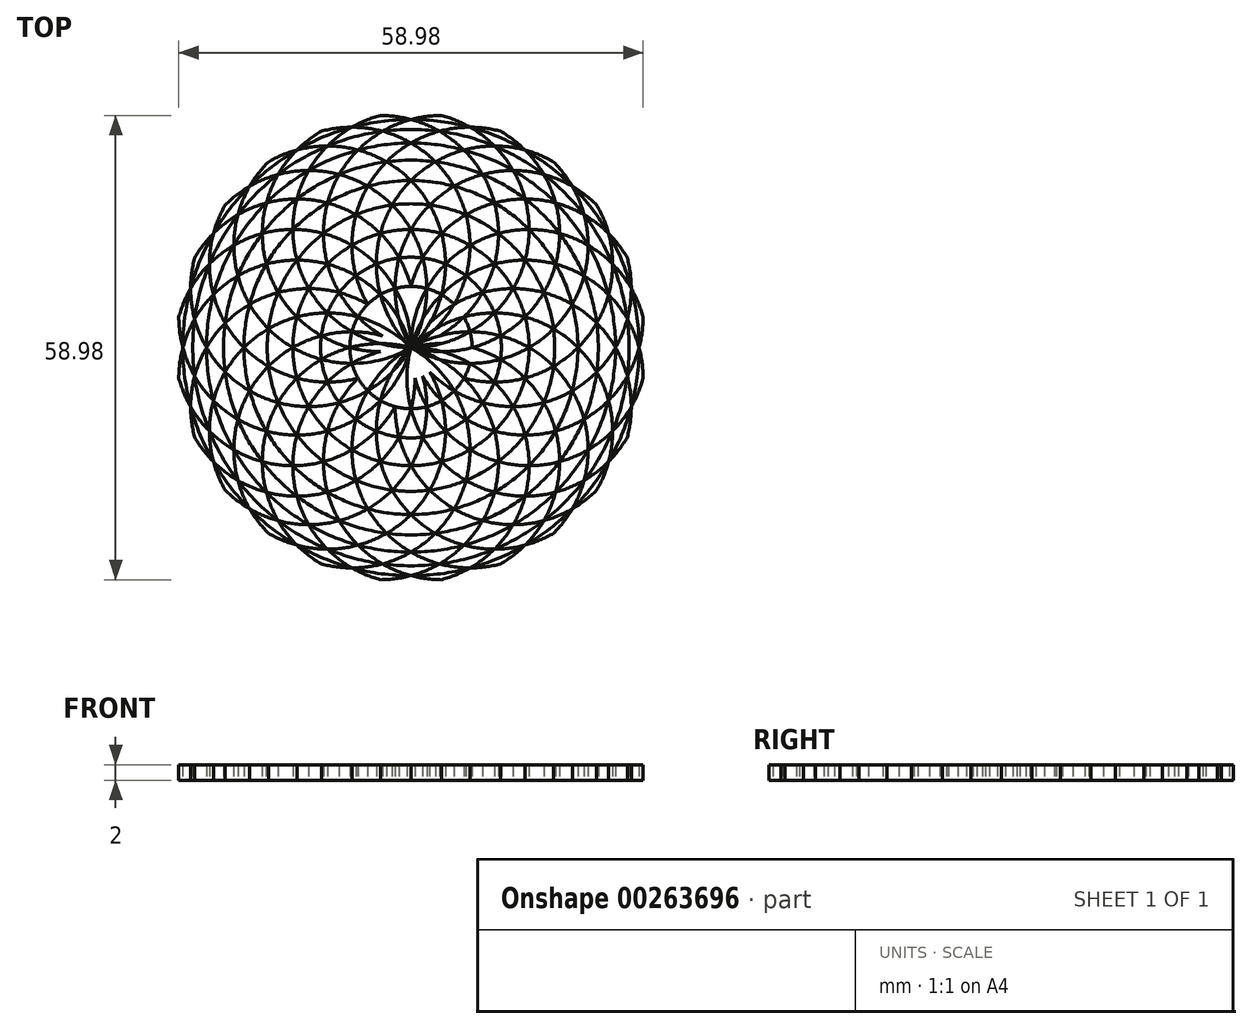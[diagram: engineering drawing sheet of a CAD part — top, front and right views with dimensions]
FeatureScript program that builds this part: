
annotation { "Feature Type Name" : "Feature", "Feature Type Description" : "" }
export const myFeature = defineFeature(function(context is Context, id is Id, definition is map)
    precondition{}
    {
        {
            var Q0;
            Q0=qCreatedBy(makeId("Top.planeOp"),FACE);
            var sketch = newSketch(context, id + "F0", { "sketchPlane" : qUnion([Q0])});
            skCircle(sketch, "E0", {"center": v(0, 0) * mm, "radius": 15 * mm});
            skLineSegment(sketch, "E1", {"start": v(-15, 0) * mm, "end": v(15, 0) * mm, "construction": true});
            skLineSegment(sketch, "E2", {"start": v(0, 15) * mm, "end": v(0, -15) * mm, "construction": true});
            skCircle(sketch, "E3", {"center": v(15, 0) * mm, "radius": 15 * mm});
            skCircle(sketch, "E4", {"center": v(7.5, 13) * mm, "radius": 15 * mm});
            skCircle(sketch, "E5", {"center": v(7.5, -13) * mm, "radius": 15 * mm});
            skCircle(sketch, "E6", {"center": v(-7.5, 13) * mm, "radius": 15 * mm});
            skCircle(sketch, "E7", {"center": v(-7.5, -13) * mm, "radius": 15 * mm});
            skCircle(sketch, "E8", {"center": v(-15, 0) * mm, "radius": 15 * mm});
            skLineSegment(sketch, "E9", {"start": v(0, 0) * mm, "end": v(22.5, 13) * mm, "construction": true});
            skCircle(sketch, "E10", {"center": v(13, 7.5) * mm, "radius": 15 * mm});
            skCircle(sketch, "E11", {"center": v(13, -7.5) * mm, "radius": 15 * mm});
            skCircle(sketch, "E12", {"center": v(0, -15) * mm, "radius": 15 * mm});
            skCircle(sketch, "E13", {"center": v(-13, -7.5) * mm, "radius": 15 * mm});
            skCircle(sketch, "E14", {"center": v(-13, 7.5) * mm, "radius": 15 * mm});
            skCircle(sketch, "E15", {"center": v(0, 15) * mm, "radius": 15 * mm});
            skLineSegment(sketch, "E16", {"start": v(7.5, 2) * mm, "end": v(20.5, 5.5) * mm, "construction": true});
            skCircle(sketch, "E17", {"center": v(14.49, 3.88) * mm, "radius": 15 * mm});
            skCircle(sketch, "E18", {"center": v(10.6, -10.6) * mm, "radius": 15 * mm});
            skCircle(sketch, "E19", {"center": v(-3.88, -14.49) * mm, "radius": 15 * mm});
            skCircle(sketch, "E20", {"center": v(-14.49, -3.88) * mm, "radius": 15 * mm});
            skCircle(sketch, "E21", {"center": v(-10.6, 10.6) * mm, "radius": 15 * mm});
            skCircle(sketch, "E22", {"center": v(3.88, 14.49) * mm, "radius": 15 * mm});
            skLineSegment(sketch, "E23", {"start": v(-2, 7.5) * mm, "end": v(-5.5, 20.5) * mm, "construction": true});
            skCircle(sketch, "E24", {"center": v(-3.88, 14.49) * mm, "radius": 15 * mm});
            skCircle(sketch, "E25", {"center": v(10.6, 10.6) * mm, "radius": 15 * mm});
            skCircle(sketch, "E26", {"center": v(14.49, -3.88) * mm, "radius": 15 * mm});
            skCircle(sketch, "E27", {"center": v(3.88, -14.49) * mm, "radius": 15 * mm});
            skCircle(sketch, "E28", {"center": v(-10.6, -10.6) * mm, "radius": 15 * mm});
            skCircle(sketch, "E29", {"center": v(-14.49, 3.88) * mm, "radius": 15 * mm});
            skCircle(sketch, "E30", {"center": v(0, 0) * mm, "radius": 18.26 * mm});
            skLineSegment(sketch, "E31", {"start": v(-6.99, 16.87) * mm, "end": v(-2.38, 18.1) * mm, "construction": true});
            skCircle(sketch, "E32", {"center": v(0, 0) * mm, "radius": 21.21 * mm});
            skLineSegment(sketch, "E33", {"start": v(0, 0) * mm, "end": v(7.5, 28) * mm, "construction": true});
            skCircle(sketch, "E34", {"center": v(0, 0) * mm, "radius": 28.98 * mm});
            skLineSegment(sketch, "E35", {"start": v(0, 0) * mm, "end": v(3.1, 23.6) * mm, "construction": true});
            skCircle(sketch, "E36", {"center": v(0, 0) * mm, "radius": 23.8 * mm});
            skLineSegment(sketch, "E37", {"start": v(0, 0) * mm, "end": v(-3.62, 27.48) * mm, "construction": true});
            skCircle(sketch, "E38", {"center": v(0, 0) * mm, "radius": 27.72 * mm});
            skLineSegment(sketch, "E39", {"start": v(0, 0) * mm, "end": v(-13, 22.5) * mm, "construction": true});
            skCircle(sketch, "E40", {"center": v(0, 0) * mm, "radius": 25.98 * mm});
            skLineSegment(sketch, "E41", {"start": v(0, 0) * mm, "end": v(-9.1, 6.99) * mm, "construction": true});
            skCircle(sketch, "E42", {"center": v(0, 0) * mm, "radius": 11.48 * mm});
            skLineSegment(sketch, "E43", {"start": v(0, 0) * mm, "end": v(-6.72, 3.88) * mm, "construction": true});
            skCircle(sketch, "E44", {"center": v(0, 0) * mm, "radius": 7.76 * mm});
            skLineSegment(sketch, "E45", {"start": v(0, 0) * mm, "end": v(-2.38, -3.1) * mm, "construction": true});
            skCircle(sketch, "E46", {"center": v(0, 0) * mm, "radius": 3.92 * mm});
            skSolve(sketch);
        }
        {
            var Q0;
            Q0=qCreatedBy(makeId("Top.planeOp"),FACE);
            cPlane(context, id + "F1", {"entities" : qUnion([Q0]), "cplaneType" : CPlaneType.OFFSET, "offset" : 0 * mm, "width" : 150 * mm, "height" : 150 * mm});
        }
        {
            var Q0;
            Q0=qCreatedBy(id+"F1.planeOp",FACE);
            var sketch = newSketch(context, id + "F2", { "sketchPlane" : qUnion([Q0])});
            skArc(sketch, "E47.0.0", {"start": v(-7.5, 2) * mm, "mid": v(-9.46, 1.88) * mm, "end": v(-11.38, 1.5) * mm});
            skArc(sketch, "E47.0.1", {"start": v(-11.38, 1.5) * mm, "mid": v(-9.62, 0.63) * mm, "end": v(-7.76, 0) * mm});
            skArc(sketch, "E48.0.1", {"start": v(-6.72, 3.88) * mm, "mid": v(-8.65, 4.27) * mm, "end": v(-10.6, 4.4) * mm});
            skArc(sketch, "E48.0.2", {"start": v(-10.6, 4.4) * mm, "mid": v(-9.13, 3.1) * mm, "end": v(-7.5, 2) * mm});
            skArc(sketch, "E49.0.1", {"start": v(-5.5, 5.5) * mm, "mid": v(-7.25, 6.36) * mm, "end": v(-9.1, 6.99) * mm});
            skArc(sketch, "E49.0.2", {"start": v(-9.1, 6.99) * mm, "mid": v(-8.02, 5.36) * mm, "end": v(-6.72, 3.88) * mm});
            skArc(sketch, "E50.0.0", {"start": v(-3.88, 6.72) * mm, "mid": v(-5.36, 8.02) * mm, "end": v(-6.99, 9.1) * mm});
            skArc(sketch, "E50.0.1", {"start": v(-6.99, 9.1) * mm, "mid": v(-6.36, 7.25) * mm, "end": v(-5.5, 5.5) * mm});
            skArc(sketch, "E51.0.1", {"start": v(-2, 7.5) * mm, "mid": v(-3.1, 9.13) * mm, "end": v(-4.4, 10.6) * mm});
            skArc(sketch, "E51.0.2", {"start": v(-4.4, 10.6) * mm, "mid": v(-4.27, 8.65) * mm, "end": v(-3.88, 6.72) * mm});
            skArc(sketch, "E52.0.1", {"start": v(0, 7.76) * mm, "mid": v(-0.63, 9.62) * mm, "end": v(-1.5, 11.38) * mm});
            skArc(sketch, "E52.0.2", {"start": v(-1.5, 11.38) * mm, "mid": v(-1.88, 9.46) * mm, "end": v(-2, 7.5) * mm});
            skArc(sketch, "E53.0.0", {"start": v(2, 7.5) * mm, "mid": v(1.88, 9.46) * mm, "end": v(1.5, 11.38) * mm});
            skArc(sketch, "E53.0.1", {"start": v(1.5, 11.38) * mm, "mid": v(0.63, 9.62) * mm, "end": v(0, 7.76) * mm});
            skArc(sketch, "E54.0.0", {"start": v(3.88, 6.72) * mm, "mid": v(4.27, 8.65) * mm, "end": v(4.4, 10.6) * mm});
            skArc(sketch, "E54.0.1", {"start": v(4.4, 10.6) * mm, "mid": v(3.1, 9.13) * mm, "end": v(2, 7.5) * mm});
            skArc(sketch, "E55.0.0", {"start": v(5.5, 5.5) * mm, "mid": v(6.36, 7.25) * mm, "end": v(6.99, 9.1) * mm});
            skArc(sketch, "E55.0.1", {"start": v(6.99, 9.1) * mm, "mid": v(5.36, 8.02) * mm, "end": v(3.88, 6.72) * mm});
            skArc(sketch, "E56.0.1", {"start": v(6.72, 3.88) * mm, "mid": v(8.02, 5.36) * mm, "end": v(9.1, 6.99) * mm});
            skArc(sketch, "E56.0.2", {"start": v(9.1, 6.99) * mm, "mid": v(7.25, 6.36) * mm, "end": v(5.5, 5.5) * mm});
            skArc(sketch, "E57.0.1", {"start": v(7.5, 2) * mm, "mid": v(9.13, 3.1) * mm, "end": v(10.6, 4.4) * mm});
            skArc(sketch, "E57.0.2", {"start": v(10.6, 4.4) * mm, "mid": v(8.65, 4.27) * mm, "end": v(6.72, 3.88) * mm});
            skArc(sketch, "E58.0.0", {"start": v(7.76, 0) * mm, "mid": v(9.62, 0.63) * mm, "end": v(11.38, 1.5) * mm});
            skArc(sketch, "E58.0.1", {"start": v(11.38, 1.5) * mm, "mid": v(9.46, 1.88) * mm, "end": v(7.5, 2) * mm});
            skArc(sketch, "E59.0.1", {"start": v(7.5, -2) * mm, "mid": v(9.46, -1.88) * mm, "end": v(11.38, -1.5) * mm});
            skArc(sketch, "E59.0.2", {"start": v(11.38, -1.5) * mm, "mid": v(9.62, -0.63) * mm, "end": v(7.76, 0) * mm});
            skArc(sketch, "E60.0.1", {"start": v(6.72, -3.88) * mm, "mid": v(8.65, -4.27) * mm, "end": v(10.6, -4.4) * mm});
            skArc(sketch, "E60.0.2", {"start": v(10.6, -4.4) * mm, "mid": v(9.13, -3.1) * mm, "end": v(7.5, -2) * mm});
            skArc(sketch, "E61.0.1", {"start": v(5.5, -5.5) * mm, "mid": v(7.25, -6.36) * mm, "end": v(9.1, -6.99) * mm});
            skArc(sketch, "E61.0.2", {"start": v(9.1, -6.99) * mm, "mid": v(8.02, -5.36) * mm, "end": v(6.72, -3.88) * mm});
            skArc(sketch, "E62.0.1", {"start": v(3.88, -6.72) * mm, "mid": v(5.36, -8.02) * mm, "end": v(6.99, -9.1) * mm});
            skArc(sketch, "E62.0.2", {"start": v(6.99, -9.1) * mm, "mid": v(6.36, -7.25) * mm, "end": v(5.5, -5.5) * mm});
            skArc(sketch, "E63.0.0", {"start": v(2, -7.5) * mm, "mid": v(3.1, -9.13) * mm, "end": v(4.4, -10.6) * mm});
            skArc(sketch, "E63.0.1", {"start": v(4.4, -10.6) * mm, "mid": v(4.27, -8.65) * mm, "end": v(3.88, -6.72) * mm});
            skArc(sketch, "E64.0.1", {"start": v(0, -7.76) * mm, "mid": v(0.63, -9.62) * mm, "end": v(1.5, -11.38) * mm});
            skArc(sketch, "E64.0.2", {"start": v(1.5, -11.38) * mm, "mid": v(1.88, -9.46) * mm, "end": v(2, -7.5) * mm});
            skArc(sketch, "E65.0.0", {"start": v(-2, -7.5) * mm, "mid": v(-1.88, -9.46) * mm, "end": v(-1.5, -11.38) * mm});
            skArc(sketch, "E65.0.1", {"start": v(-1.5, -11.38) * mm, "mid": v(-0.63, -9.62) * mm, "end": v(0, -7.76) * mm});
            skArc(sketch, "E66.0.1", {"start": v(-3.88, -6.72) * mm, "mid": v(-4.27, -8.65) * mm, "end": v(-4.4, -10.6) * mm});
            skArc(sketch, "E66.0.2", {"start": v(-4.4, -10.6) * mm, "mid": v(-3.1, -9.13) * mm, "end": v(-2, -7.5) * mm});
            skArc(sketch, "E67.0.0", {"start": v(-5.5, -5.5) * mm, "mid": v(-6.36, -7.25) * mm, "end": v(-6.99, -9.1) * mm});
            skArc(sketch, "E67.0.1", {"start": v(-6.99, -9.1) * mm, "mid": v(-5.36, -8.02) * mm, "end": v(-3.88, -6.72) * mm});
            skArc(sketch, "E68.0.1", {"start": v(-6.72, -3.88) * mm, "mid": v(-8.02, -5.36) * mm, "end": v(-9.1, -6.99) * mm});
            skArc(sketch, "E68.0.2", {"start": v(-9.1, -6.99) * mm, "mid": v(-7.25, -6.36) * mm, "end": v(-5.5, -5.5) * mm});
            skArc(sketch, "E69.0.1", {"start": v(-7.5, -2) * mm, "mid": v(-9.13, -3.1) * mm, "end": v(-10.6, -4.4) * mm});
            skArc(sketch, "E69.0.2", {"start": v(-10.6, -4.4) * mm, "mid": v(-8.65, -4.27) * mm, "end": v(-6.72, -3.88) * mm});
            skArc(sketch, "E70.0.1", {"start": v(-7.76, 0) * mm, "mid": v(-9.62, -0.63) * mm, "end": v(-11.38, -1.5) * mm});
            skArc(sketch, "E70.0.2", {"start": v(-11.38, -1.5) * mm, "mid": v(-9.46, -1.88) * mm, "end": v(-7.5, -2) * mm});
            skArc(sketch, "E71.0.1", {"start": v(-10.6, 4.4) * mm, "mid": v(-12.56, 4.27) * mm, "end": v(-14.49, 3.88) * mm});
            skArc(sketch, "E71.0.2", {"start": v(-14.49, 3.88) * mm, "mid": v(-13.01, 2.59) * mm, "end": v(-11.38, 1.5) * mm});
            skArc(sketch, "E72.0.1", {"start": v(-9.1, 6.99) * mm, "mid": v(-11.03, 7.37) * mm, "end": v(-13, 7.5) * mm});
            skArc(sketch, "E72.0.2", {"start": v(-13, 7.5) * mm, "mid": v(-11.9, 5.87) * mm, "end": v(-10.6, 4.4) * mm});
            skArc(sketch, "E73.0.1", {"start": v(-6.99, 9.1) * mm, "mid": v(-8.75, 9.98) * mm, "end": v(-10.6, 10.6) * mm});
            skArc(sketch, "E73.0.2", {"start": v(-10.6, 10.6) * mm, "mid": v(-9.98, 8.75) * mm, "end": v(-9.1, 6.99) * mm});
            skArc(sketch, "E74.0.1", {"start": v(-4.4, 10.6) * mm, "mid": v(-5.87, 11.9) * mm, "end": v(-7.5, 13) * mm});
            skArc(sketch, "E74.0.2", {"start": v(-7.5, 13) * mm, "mid": v(-7.37, 11.03) * mm, "end": v(-6.99, 9.1) * mm});
            skArc(sketch, "E75.0.1", {"start": v(-1.5, 11.38) * mm, "mid": v(-2.59, 13.01) * mm, "end": v(-3.88, 14.49) * mm});
            skArc(sketch, "E75.0.2", {"start": v(-3.88, 14.49) * mm, "mid": v(-4.27, 12.56) * mm, "end": v(-4.4, 10.6) * mm});
            skArc(sketch, "E76.0.0", {"start": v(1.5, 11.38) * mm, "mid": v(0.87, 13.24) * mm, "end": v(0, 15) * mm});
            skArc(sketch, "E76.0.1", {"start": v(0, 15) * mm, "mid": v(-0.87, 13.24) * mm, "end": v(-1.5, 11.38) * mm});
            skArc(sketch, "E77.0.1", {"start": v(4.4, 10.6) * mm, "mid": v(4.27, 12.56) * mm, "end": v(3.88, 14.49) * mm});
            skArc(sketch, "E77.0.2", {"start": v(3.88, 14.49) * mm, "mid": v(2.59, 13.01) * mm, "end": v(1.5, 11.38) * mm});
            skArc(sketch, "E78.0.1", {"start": v(6.99, 9.1) * mm, "mid": v(7.37, 11.03) * mm, "end": v(7.5, 13) * mm});
            skArc(sketch, "E78.0.2", {"start": v(7.5, 13) * mm, "mid": v(5.87, 11.9) * mm, "end": v(4.4, 10.6) * mm});
            skArc(sketch, "E79.0.1", {"start": v(9.1, 6.99) * mm, "mid": v(9.98, 8.75) * mm, "end": v(10.6, 10.6) * mm});
            skArc(sketch, "E79.0.2", {"start": v(10.6, 10.6) * mm, "mid": v(8.75, 9.98) * mm, "end": v(6.99, 9.1) * mm});
            skArc(sketch, "E80.0.0", {"start": v(10.6, 4.4) * mm, "mid": v(11.9, 5.87) * mm, "end": v(13, 7.5) * mm});
            skArc(sketch, "E80.0.1", {"start": v(13, 7.5) * mm, "mid": v(11.03, 7.37) * mm, "end": v(9.1, 6.99) * mm});
            skArc(sketch, "E81.0.1", {"start": v(11.38, 1.5) * mm, "mid": v(13.01, 2.59) * mm, "end": v(14.49, 3.88) * mm});
            skArc(sketch, "E81.0.2", {"start": v(14.49, 3.88) * mm, "mid": v(12.56, 4.27) * mm, "end": v(10.6, 4.4) * mm});
            skArc(sketch, "E82.0.0", {"start": v(11.38, -1.5) * mm, "mid": v(13.24, -0.87) * mm, "end": v(15, 0) * mm});
            skArc(sketch, "E82.0.1", {"start": v(15, 0) * mm, "mid": v(13.24, 0.87) * mm, "end": v(11.38, 1.5) * mm});
            skArc(sketch, "E83.0.1", {"start": v(10.6, -4.4) * mm, "mid": v(12.56, -4.27) * mm, "end": v(14.49, -3.88) * mm});
            skArc(sketch, "E83.0.2", {"start": v(14.49, -3.88) * mm, "mid": v(13.01, -2.59) * mm, "end": v(11.38, -1.5) * mm});
            skArc(sketch, "E84.0.1", {"start": v(9.1, -6.99) * mm, "mid": v(11.03, -7.37) * mm, "end": v(13, -7.5) * mm});
            skArc(sketch, "E84.0.2", {"start": v(13, -7.5) * mm, "mid": v(11.9, -5.87) * mm, "end": v(10.6, -4.4) * mm});
            skArc(sketch, "E85.0.1", {"start": v(6.99, -9.1) * mm, "mid": v(8.75, -9.98) * mm, "end": v(10.6, -10.6) * mm});
            skArc(sketch, "E85.0.2", {"start": v(10.6, -10.6) * mm, "mid": v(9.98, -8.75) * mm, "end": v(9.1, -6.99) * mm});
            skArc(sketch, "E86.0.0", {"start": v(4.4, -10.6) * mm, "mid": v(5.87, -11.9) * mm, "end": v(7.5, -13) * mm});
            skArc(sketch, "E86.0.1", {"start": v(7.5, -13) * mm, "mid": v(7.37, -11.03) * mm, "end": v(6.99, -9.1) * mm});
            skArc(sketch, "E87.0.1", {"start": v(1.5, -11.38) * mm, "mid": v(2.59, -13.01) * mm, "end": v(3.88, -14.49) * mm});
            skArc(sketch, "E87.0.2", {"start": v(3.88, -14.49) * mm, "mid": v(4.27, -12.56) * mm, "end": v(4.4, -10.6) * mm});
            skArc(sketch, "E88.0.1", {"start": v(-1.5, -11.38) * mm, "mid": v(-0.87, -13.24) * mm, "end": v(0, -15) * mm});
            skArc(sketch, "E88.0.2", {"start": v(0, -15) * mm, "mid": v(0.87, -13.24) * mm, "end": v(1.5, -11.38) * mm});
            skArc(sketch, "E89.0.1", {"start": v(-4.4, -10.6) * mm, "mid": v(-4.27, -12.56) * mm, "end": v(-3.88, -14.49) * mm});
            skArc(sketch, "E89.0.2", {"start": v(-3.88, -14.49) * mm, "mid": v(-2.59, -13.01) * mm, "end": v(-1.5, -11.38) * mm});
            skArc(sketch, "E90.0.1", {"start": v(-6.99, -9.1) * mm, "mid": v(-7.37, -11.03) * mm, "end": v(-7.5, -13) * mm});
            skArc(sketch, "E90.0.2", {"start": v(-7.5, -13) * mm, "mid": v(-5.87, -11.9) * mm, "end": v(-4.4, -10.6) * mm});
            skArc(sketch, "E91.0.0", {"start": v(-9.1, -6.99) * mm, "mid": v(-9.98, -8.75) * mm, "end": v(-10.6, -10.6) * mm});
            skArc(sketch, "E91.0.1", {"start": v(-10.6, -10.6) * mm, "mid": v(-8.75, -9.98) * mm, "end": v(-6.99, -9.1) * mm});
            skArc(sketch, "E92.0.1", {"start": v(-10.6, -4.4) * mm, "mid": v(-11.9, -5.87) * mm, "end": v(-13, -7.5) * mm});
            skArc(sketch, "E92.0.2", {"start": v(-13, -7.5) * mm, "mid": v(-11.03, -7.37) * mm, "end": v(-9.1, -6.99) * mm});
            skArc(sketch, "E93.0.0", {"start": v(-11.38, -1.5) * mm, "mid": v(-13.01, -2.59) * mm, "end": v(-14.49, -3.88) * mm});
            skArc(sketch, "E93.0.1", {"start": v(-14.49, -3.88) * mm, "mid": v(-12.56, -4.27) * mm, "end": v(-10.6, -4.4) * mm});
            skArc(sketch, "E94.0.1", {"start": v(-11.38, 1.5) * mm, "mid": v(-13.24, 0.87) * mm, "end": v(-15, 0) * mm});
            skArc(sketch, "E94.0.2", {"start": v(-15, 0) * mm, "mid": v(-13.24, -0.87) * mm, "end": v(-11.38, -1.5) * mm});
            skArc(sketch, "E95.0.0", {"start": v(-3.88, 6.72) * mm, "mid": v(-2.59, 5.25) * mm, "end": v(-1.5, 3.62) * mm});
            skArc(sketch, "E95.0.1", {"start": v(-1.5, 3.62) * mm, "mid": v(-1.88, 5.54) * mm, "end": v(-2, 7.5) * mm});
            skArc(sketch, "E95.0.2", {"start": v(-2, 7.5) * mm, "mid": v(-2.97, 7.17) * mm, "end": v(-3.88, 6.72) * mm});
            skArc(sketch, "E96.0.0", {"start": v(-2.38, 3.1) * mm, "mid": v(-3.25, 4.87) * mm, "end": v(-3.88, 6.72) * mm});
            skArc(sketch, "E96.0.1", {"start": v(-3.88, 6.72) * mm, "mid": v(-4.73, 6.16) * mm, "end": v(-5.5, 5.5) * mm});
            skArc(sketch, "E96.0.2", {"start": v(-5.5, 5.5) * mm, "mid": v(-3.86, 4.4) * mm, "end": v(-2.38, 3.1) * mm});
            skArc(sketch, "E97.0.0", {"start": v(-6.72, 3.88) * mm, "mid": v(-4.87, 3.25) * mm, "end": v(-3.1, 2.38) * mm});
            skArc(sketch, "E97.0.1", {"start": v(-3.1, 2.38) * mm, "mid": v(-4.4, 3.86) * mm, "end": v(-5.5, 5.5) * mm});
            skArc(sketch, "E98.0.0", {"start": v(-3.62, 1.5) * mm, "mid": v(-5.25, 2.59) * mm, "end": v(-6.72, 3.88) * mm});
            skArc(sketch, "E98.0.1", {"start": v(-6.72, 3.88) * mm, "mid": v(-7.17, 2.97) * mm, "end": v(-7.5, 2) * mm});
            skArc(sketch, "E98.0.2", {"start": v(-7.5, 2) * mm, "mid": v(-5.54, 1.88) * mm, "end": v(-3.62, 1.5) * mm});
            skArc(sketch, "E99.0.0", {"start": v(-3.88, 0.51) * mm, "mid": v(-5.74, 1.14) * mm, "end": v(-7.5, 2) * mm});
            skArc(sketch, "E99.0.1", {"start": v(-7.5, 2) * mm, "mid": v(-7.7, 1.01) * mm, "end": v(-7.76, 0) * mm});
            skArc(sketch, "E99.0.2", {"start": v(-7.76, 0) * mm, "mid": v(-5.84, 0.38) * mm, "end": v(-3.88, 0.51) * mm});
            skArc(sketch, "E100.0.0", {"start": v(-3.88, -0.51) * mm, "mid": v(-5.84, -0.38) * mm, "end": v(-7.76, 0) * mm});
            skArc(sketch, "E100.0.1", {"start": v(-7.76, 0) * mm, "mid": v(-7.7, -1.01) * mm, "end": v(-7.5, -2) * mm});
            skArc(sketch, "E100.0.2", {"start": v(-7.5, -2) * mm, "mid": v(-5.74, -1.14) * mm, "end": v(-3.88, -0.51) * mm});
            skArc(sketch, "E101.0.0", {"start": v(-3.62, -1.5) * mm, "mid": v(-5.54, -1.88) * mm, "end": v(-7.5, -2) * mm});
            skArc(sketch, "E101.0.1", {"start": v(-7.5, -2) * mm, "mid": v(-7.17, -2.97) * mm, "end": v(-6.72, -3.88) * mm});
            skArc(sketch, "E101.0.2", {"start": v(-6.72, -3.88) * mm, "mid": v(-5.25, -2.59) * mm, "end": v(-3.62, -1.5) * mm});
            skArc(sketch, "E102.0.0", {"start": v(-5.5, -5.5) * mm, "mid": v(-4.4, -3.86) * mm, "end": v(-3.1, -2.38) * mm});
            skArc(sketch, "E102.0.1", {"start": v(-3.1, -2.38) * mm, "mid": v(-4.87, -3.25) * mm, "end": v(-6.72, -3.88) * mm});
            skArc(sketch, "E102.0.2", {"start": v(-6.72, -3.88) * mm, "mid": v(-6.16, -4.73) * mm, "end": v(-5.5, -5.5) * mm});
            skArc(sketch, "E103.0.0", {"start": v(-2.38, -3.1) * mm, "mid": v(-3.86, -4.4) * mm, "end": v(-5.5, -5.5) * mm});
            skArc(sketch, "E103.0.1", {"start": v(-5.5, -5.5) * mm, "mid": v(-4.73, -6.16) * mm, "end": v(-3.88, -6.72) * mm});
            skArc(sketch, "E103.0.2", {"start": v(-3.88, -6.72) * mm, "mid": v(-3.25, -4.87) * mm, "end": v(-2.38, -3.1) * mm});
            skArc(sketch, "E104.0.0", {"start": v(-1.5, -3.62) * mm, "mid": v(-2.59, -5.25) * mm, "end": v(-3.88, -6.72) * mm});
            skArc(sketch, "E104.0.1", {"start": v(-3.88, -6.72) * mm, "mid": v(-2.97, -7.17) * mm, "end": v(-2, -7.5) * mm});
            skArc(sketch, "E104.0.2", {"start": v(-2, -7.5) * mm, "mid": v(-1.88, -5.54) * mm, "end": v(-1.5, -3.62) * mm});
            skArc(sketch, "E105.0.0", {"start": v(0, -7.76) * mm, "mid": v(-0.38, -5.84) * mm, "end": v(-0.51, -3.88) * mm});
            skArc(sketch, "E105.0.1", {"start": v(-0.51, -3.88) * mm, "mid": v(-1.14, -5.74) * mm, "end": v(-2, -7.5) * mm});
            skArc(sketch, "E105.0.2", {"start": v(-2, -7.5) * mm, "mid": v(-1.01, -7.7) * mm, "end": v(0, -7.76) * mm});
            skArc(sketch, "E106.0.0", {"start": v(0.51, -3.88) * mm, "mid": v(0.38, -5.84) * mm, "end": v(0, -7.76) * mm});
            skArc(sketch, "E106.0.1", {"start": v(0, -7.76) * mm, "mid": v(1.01, -7.7) * mm, "end": v(2, -7.5) * mm});
            skArc(sketch, "E106.0.2", {"start": v(2, -7.5) * mm, "mid": v(1.14, -5.74) * mm, "end": v(0.51, -3.88) * mm});
            skArc(sketch, "E107.0.0", {"start": v(1.5, -3.62) * mm, "mid": v(1.88, -5.54) * mm, "end": v(2, -7.5) * mm});
            skArc(sketch, "E107.0.1", {"start": v(2, -7.5) * mm, "mid": v(2.97, -7.17) * mm, "end": v(3.88, -6.72) * mm});
            skArc(sketch, "E107.0.2", {"start": v(3.88, -6.72) * mm, "mid": v(2.59, -5.25) * mm, "end": v(1.5, -3.62) * mm});
            skArc(sketch, "E108.0.0", {"start": v(2.38, -3.1) * mm, "mid": v(3.25, -4.87) * mm, "end": v(3.88, -6.72) * mm});
            skArc(sketch, "E108.0.1", {"start": v(3.88, -6.72) * mm, "mid": v(4.73, -6.16) * mm, "end": v(5.5, -5.5) * mm});
            skArc(sketch, "E108.0.2", {"start": v(5.5, -5.5) * mm, "mid": v(3.86, -4.4) * mm, "end": v(2.38, -3.1) * mm});
            skArc(sketch, "E109.0.0", {"start": v(3.1, -2.38) * mm, "mid": v(4.4, -3.86) * mm, "end": v(5.5, -5.5) * mm});
            skArc(sketch, "E109.0.1", {"start": v(5.5, -5.5) * mm, "mid": v(6.16, -4.73) * mm, "end": v(6.72, -3.88) * mm});
            skArc(sketch, "E109.0.2", {"start": v(6.72, -3.88) * mm, "mid": v(4.87, -3.25) * mm, "end": v(3.1, -2.38) * mm});
            skArc(sketch, "E110.0.0", {"start": v(7.5, -2) * mm, "mid": v(5.54, -1.88) * mm, "end": v(3.62, -1.5) * mm});
            skArc(sketch, "E110.0.1", {"start": v(3.62, -1.5) * mm, "mid": v(5.25, -2.59) * mm, "end": v(6.72, -3.88) * mm});
            skArc(sketch, "E110.0.2", {"start": v(6.72, -3.88) * mm, "mid": v(7.17, -2.97) * mm, "end": v(7.5, -2) * mm});
            skArc(sketch, "E111.0.0", {"start": v(3.88, -0.51) * mm, "mid": v(5.74, -1.14) * mm, "end": v(7.5, -2) * mm});
            skArc(sketch, "E111.0.1", {"start": v(7.5, -2) * mm, "mid": v(7.7, -1.01) * mm, "end": v(7.76, 0) * mm});
            skArc(sketch, "E111.0.2", {"start": v(7.76, 0) * mm, "mid": v(5.84, -0.38) * mm, "end": v(3.88, -0.51) * mm});
            skArc(sketch, "E112.0.0", {"start": v(7.5, 2) * mm, "mid": v(5.74, 1.14) * mm, "end": v(3.88, 0.51) * mm});
            skArc(sketch, "E112.0.1", {"start": v(3.88, 0.51) * mm, "mid": v(5.84, 0.38) * mm, "end": v(7.76, 0) * mm});
            skArc(sketch, "E112.0.2", {"start": v(7.76, 0) * mm, "mid": v(7.7, 1.01) * mm, "end": v(7.5, 2) * mm});
            skArc(sketch, "E113.0.0", {"start": v(6.72, 3.88) * mm, "mid": v(5.25, 2.59) * mm, "end": v(3.62, 1.5) * mm});
            skArc(sketch, "E113.0.1", {"start": v(3.62, 1.5) * mm, "mid": v(5.54, 1.88) * mm, "end": v(7.5, 2) * mm});
            skArc(sketch, "E113.0.2", {"start": v(7.5, 2) * mm, "mid": v(7.17, 2.97) * mm, "end": v(6.72, 3.88) * mm});
            skArc(sketch, "E114.0.0", {"start": v(3.1, 2.38) * mm, "mid": v(4.87, 3.25) * mm, "end": v(6.72, 3.88) * mm});
            skArc(sketch, "E114.0.1", {"start": v(6.72, 3.88) * mm, "mid": v(6.16, 4.73) * mm, "end": v(5.5, 5.5) * mm});
            skArc(sketch, "E114.0.2", {"start": v(5.5, 5.5) * mm, "mid": v(4.4, 3.86) * mm, "end": v(3.1, 2.38) * mm});
            skArc(sketch, "E115.0.0", {"start": v(2.38, 3.1) * mm, "mid": v(3.86, 4.4) * mm, "end": v(5.5, 5.5) * mm});
            skArc(sketch, "E115.0.1", {"start": v(5.5, 5.5) * mm, "mid": v(4.73, 6.16) * mm, "end": v(3.88, 6.72) * mm});
            skArc(sketch, "E115.0.2", {"start": v(3.88, 6.72) * mm, "mid": v(3.25, 4.87) * mm, "end": v(2.38, 3.1) * mm});
            skArc(sketch, "E116.0.0", {"start": v(1.5, 3.62) * mm, "mid": v(2.59, 5.25) * mm, "end": v(3.88, 6.72) * mm});
            skArc(sketch, "E116.0.1", {"start": v(3.88, 6.72) * mm, "mid": v(2.97, 7.17) * mm, "end": v(2, 7.5) * mm});
            skArc(sketch, "E116.0.2", {"start": v(2, 7.5) * mm, "mid": v(1.88, 5.54) * mm, "end": v(1.5, 3.62) * mm});
            skArc(sketch, "E117.0.0", {"start": v(0.51, 3.88) * mm, "mid": v(1.14, 5.74) * mm, "end": v(2, 7.5) * mm});
            skArc(sketch, "E117.0.1", {"start": v(2, 7.5) * mm, "mid": v(1.01, 7.7) * mm, "end": v(0, 7.76) * mm});
            skArc(sketch, "E117.0.2", {"start": v(0, 7.76) * mm, "mid": v(0.38, 5.84) * mm, "end": v(0.51, 3.88) * mm});
            skArc(sketch, "E118.0.0", {"start": v(-2, 7.5) * mm, "mid": v(-1.14, 5.74) * mm, "end": v(-0.51, 3.88) * mm});
            skArc(sketch, "E118.0.1", {"start": v(-0.51, 3.88) * mm, "mid": v(-0.38, 5.84) * mm, "end": v(0, 7.76) * mm});
            skArc(sketch, "E118.0.2", {"start": v(0, 7.76) * mm, "mid": v(-1.01, 7.7) * mm, "end": v(-2, 7.5) * mm});
            skArc(sketch, "E119.0.0", {"start": v(0, 0) * mm, "mid": v(0.87, 1.76) * mm, "end": v(1.5, 3.62) * mm});
            skArc(sketch, "E119.0.1", {"start": v(1.5, 3.62) * mm, "mid": v(0.63, 1.86) * mm, "end": v(0, 0) * mm});
            skArc(sketch, "E120.0.0", {"start": v(0, 0) * mm, "mid": v(1.3, 1.48) * mm, "end": v(2.38, 3.1) * mm});
            skArc(sketch, "E120.0.1", {"start": v(2.38, 3.1) * mm, "mid": v(1.1, 1.63) * mm, "end": v(0, 0) * mm});
            skArc(sketch, "E121.0.0", {"start": v(3.1, 2.38) * mm, "mid": v(1.48, 1.3) * mm, "end": v(0, 0) * mm});
            skArc(sketch, "E121.0.1", {"start": v(0, 0) * mm, "mid": v(1.63, 1.1) * mm, "end": v(3.1, 2.38) * mm});
            skArc(sketch, "E122.0.0", {"start": v(3.62, 1.5) * mm, "mid": v(1.76, 0.87) * mm, "end": v(0, 0) * mm});
            skArc(sketch, "E122.0.1", {"start": v(0, 0) * mm, "mid": v(1.86, 0.63) * mm, "end": v(3.62, 1.5) * mm});
            skArc(sketch, "E123.0.0", {"start": v(3.88, 0.51) * mm, "mid": v(1.92, 0.38) * mm, "end": v(0, 0) * mm});
            skArc(sketch, "E123.0.1", {"start": v(0, 0) * mm, "mid": v(1.96, 0.13) * mm, "end": v(3.88, 0.51) * mm});
            skArc(sketch, "E124.0.0", {"start": v(3.88, -0.51) * mm, "mid": v(1.96, -0.13) * mm, "end": v(0, 0) * mm});
            skArc(sketch, "E124.0.1", {"start": v(0, 0) * mm, "mid": v(1.92, -0.38) * mm, "end": v(3.88, -0.51) * mm});
            skArc(sketch, "E125.0.0", {"start": v(3.62, -1.5) * mm, "mid": v(1.86, -0.63) * mm, "end": v(0, 0) * mm});
            skArc(sketch, "E125.0.1", {"start": v(0, 0) * mm, "mid": v(1.76, -0.87) * mm, "end": v(3.62, -1.5) * mm});
            skArc(sketch, "E126.0.0", {"start": v(3.1, -2.38) * mm, "mid": v(1.63, -1.1) * mm, "end": v(0, 0) * mm});
            skArc(sketch, "E126.0.1", {"start": v(0, 0) * mm, "mid": v(1.48, -1.3) * mm, "end": v(3.1, -2.38) * mm});
            skArc(sketch, "E127.0.0", {"start": v(0, 0) * mm, "mid": v(1.1, -1.63) * mm, "end": v(2.38, -3.1) * mm});
            skArc(sketch, "E127.0.1", {"start": v(2.38, -3.1) * mm, "mid": v(1.3, -1.48) * mm, "end": v(0, 0) * mm});
            skArc(sketch, "E128.0.0", {"start": v(0, 0) * mm, "mid": v(0.63, -1.86) * mm, "end": v(1.5, -3.62) * mm});
            skArc(sketch, "E128.0.1", {"start": v(1.5, -3.62) * mm, "mid": v(0.87, -1.76) * mm, "end": v(0, 0) * mm});
            skArc(sketch, "E129.0.0", {"start": v(0, 0) * mm, "mid": v(0.13, -1.96) * mm, "end": v(0.51, -3.88) * mm});
            skArc(sketch, "E129.0.1", {"start": v(0.51, -3.88) * mm, "mid": v(0.38, -1.92) * mm, "end": v(0, 0) * mm});
            skArc(sketch, "E130.0.0", {"start": v(-0.51, -3.88) * mm, "mid": v(-0.13, -1.96) * mm, "end": v(0, 0) * mm});
            skArc(sketch, "E130.0.1", {"start": v(0, 0) * mm, "mid": v(-0.38, -1.92) * mm, "end": v(-0.51, -3.88) * mm});
            skArc(sketch, "E131.0.0", {"start": v(0, 0) * mm, "mid": v(-0.87, -1.76) * mm, "end": v(-1.5, -3.62) * mm});
            skArc(sketch, "E131.0.1", {"start": v(-1.5, -3.62) * mm, "mid": v(-0.63, -1.86) * mm, "end": v(0, 0) * mm});
            skArc(sketch, "E132.0.0", {"start": v(0, 0) * mm, "mid": v(-1.3, -1.48) * mm, "end": v(-2.38, -3.1) * mm});
            skArc(sketch, "E132.0.1", {"start": v(-2.38, -3.1) * mm, "mid": v(-1.1, -1.63) * mm, "end": v(0, 0) * mm});
            skArc(sketch, "E133.0.0", {"start": v(-3.1, -2.38) * mm, "mid": v(-1.48, -1.3) * mm, "end": v(0, 0) * mm});
            skArc(sketch, "E133.0.1", {"start": v(0, 0) * mm, "mid": v(-1.63, -1.1) * mm, "end": v(-3.1, -2.38) * mm});
            skArc(sketch, "E134.0.0", {"start": v(-3.62, -1.5) * mm, "mid": v(-1.76, -0.87) * mm, "end": v(0, 0) * mm});
            skArc(sketch, "E134.0.1", {"start": v(0, 0) * mm, "mid": v(-1.86, -0.63) * mm, "end": v(-3.62, -1.5) * mm});
            skArc(sketch, "E135.0.0", {"start": v(0, 0) * mm, "mid": v(-1.96, -0.13) * mm, "end": v(-3.88, -0.51) * mm});
            skArc(sketch, "E135.0.1", {"start": v(-3.88, -0.51) * mm, "mid": v(-1.92, -0.38) * mm, "end": v(0, 0) * mm});
            skArc(sketch, "E136.0.0", {"start": v(0, 0) * mm, "mid": v(-1.92, 0.38) * mm, "end": v(-3.88, 0.51) * mm});
            skArc(sketch, "E136.0.1", {"start": v(-3.88, 0.51) * mm, "mid": v(-1.96, 0.13) * mm, "end": v(0, 0) * mm});
            skArc(sketch, "E137.0.0", {"start": v(0, 0) * mm, "mid": v(-1.76, 0.87) * mm, "end": v(-3.62, 1.5) * mm});
            skArc(sketch, "E137.0.1", {"start": v(-3.62, 1.5) * mm, "mid": v(-1.86, 0.63) * mm, "end": v(0, 0) * mm});
            skArc(sketch, "E138.0.0", {"start": v(-3.1, 2.38) * mm, "mid": v(-1.63, 1.1) * mm, "end": v(0, 0) * mm});
            skArc(sketch, "E138.0.1", {"start": v(0, 0) * mm, "mid": v(-1.48, 1.3) * mm, "end": v(-3.1, 2.38) * mm});
            skArc(sketch, "E139.0.0", {"start": v(-2.38, 3.1) * mm, "mid": v(-1.3, 1.48) * mm, "end": v(0, 0) * mm});
            skArc(sketch, "E139.0.1", {"start": v(0, 0) * mm, "mid": v(-1.1, 1.63) * mm, "end": v(-2.38, 3.1) * mm});
            skArc(sketch, "E140.0.0", {"start": v(-1.5, 3.62) * mm, "mid": v(-0.87, 1.76) * mm, "end": v(0, 0) * mm});
            skArc(sketch, "E140.0.1", {"start": v(0, 0) * mm, "mid": v(-0.63, 1.86) * mm, "end": v(-1.5, 3.62) * mm});
            skArc(sketch, "E141.0.0", {"start": v(0, 0) * mm, "mid": v(-0.13, 1.96) * mm, "end": v(-0.51, 3.88) * mm});
            skArc(sketch, "E141.0.1", {"start": v(-0.51, 3.88) * mm, "mid": v(-0.38, 1.92) * mm, "end": v(0, 0) * mm});
            skArc(sketch, "E142.0.0", {"start": v(0, 0) * mm, "mid": v(0.38, 1.92) * mm, "end": v(0.51, 3.88) * mm});
            skArc(sketch, "E142.0.1", {"start": v(0.51, 3.88) * mm, "mid": v(0.13, 1.96) * mm, "end": v(0, 0) * mm});
            skCircle(sketch, "E143.0", {"center": v(0, 0) * mm, "radius": 7.76 * mm});
            skCircle(sketch, "E144.0", {"center": v(0, 0) * mm, "radius": 11.48 * mm});
            skCircle(sketch, "E145.0", {"center": v(0, 0) * mm, "radius": 15 * mm});
            skCircle(sketch, "E146.0", {"center": v(0, 0) * mm, "radius": 18.26 * mm});
            skCircle(sketch, "E147.0", {"center": v(0, 0) * mm, "radius": 21.21 * mm});
            skCircle(sketch, "E148.0", {"center": v(0, 0) * mm, "radius": 23.8 * mm});
            skCircle(sketch, "E149.0", {"center": v(0, 0) * mm, "radius": 25.98 * mm});
            skCircle(sketch, "E150.0", {"center": v(0, 0) * mm, "radius": 27.72 * mm});
            skCircle(sketch, "E151.0", {"center": v(0, 0) * mm, "radius": 28.98 * mm});
            skSolve(sketch);
        }
        {
            var Q0;
            Q0=qCreatedBy(makeId("Top.planeOp"),FACE);
            cPlane(context, id + "F3", {"entities" : qUnion([Q0]), "cplaneType" : CPlaneType.OFFSET, "offset" : 0 * mm, "width" : 150 * mm, "height" : 150 * mm});
        }
        {
            var Q0;
            Q0=qCreatedBy(id+"F3.planeOp",FACE);
            var sketch = newSketch(context, id + "F4", { "sketchPlane" : qUnion([Q0])});
            skCircle(sketch, "E152", {"center": v(0, 0) * mm, "radius": 30 * mm});
            skSolve(sketch);
        }
        {
            var Q0;
            Q0=qCreatedBy(makeId("Front.planeOp"),FACE);
            var sketch = newSketch(context, id + "F5", { "sketchPlane" : qUnion([Q0])});
            skLineSegment(sketch, "E153", {"start": v(0, 30) * mm, "end": v(0, -30) * mm, "construction": true});
            skArc(sketch, "E154", {"start": v(30, 0) * mm, "mid": v(0, 30) * mm, "end": v(-30, 0) * mm});
            skSolve(sketch);
        }
        {
            var Q0;
            {var subQ0=sQuery(id+"F0.wireOp",EDGE,"E26");var subQ1=sQuery(id+"F0.wireOp",EDGE,"E14");var subQ2=makeQuery(id+"F0.imprint","INTERSECT",VERTEX,{"derivedFrom":[subQ1,subQ0,sQuery(id+"F0.wireOp",EDGE,"E46")]});Q0=makeQuery(id+"F0.imprint","IMPRINT",FACE,{"disambiguationData":[TD([[makeQuery(id+"F0.imprint","IMPRINT",EDGE,{"disambiguationData":[TD([[subQ2,1.0]])],"derivedFrom":subQ1}),1.0]])]});}
            var Q1;
            Q1=makeQuery(id+"F2.imprint","IMPRINT",FACE,{"disambiguationData":[TD([[makeQuery(id+"F2.imprint","IMPRINT",EDGE,{"derivedFrom":sQuery(id+"F2.wireOp",EDGE,"E142.0.0")}),1.0]])]});
            var Q2;
            Q2=makeQuery(id+"F2.imprint","IMPRINT",FACE,{"disambiguationData":[TD([[makeQuery(id+"F2.imprint","IMPRINT",EDGE,{"derivedFrom":sQuery(id+"F2.wireOp",EDGE,"E141.0.0")}),1.0]])]});
            var Q3;
            {var subQ0=sQuery(id+"F0.wireOp",EDGE,"E20");var subQ1=sQuery(id+"F0.wireOp",EDGE,"E10");var subQ2=makeQuery(id+"F0.imprint","INTERSECT",VERTEX,{"derivedFrom":[subQ1,subQ0,sQuery(id+"F0.wireOp",EDGE,"E46")]});Q3=makeQuery(id+"F0.imprint","IMPRINT",FACE,{"disambiguationData":[TD([[makeQuery(id+"F0.imprint","IMPRINT",EDGE,{"disambiguationData":[TD([[subQ2,-1.0]])],"derivedFrom":subQ1}),1.0]])]});}
            var Q4;
            Q4=makeQuery(id+"F2.imprint","IMPRINT",FACE,{"disambiguationData":[TD([[makeQuery(id+"F2.imprint","IMPRINT",EDGE,{"derivedFrom":sQuery(id+"F2.wireOp",EDGE,"E139.0.0")}),1.0]])]});
            var Q5;
            Q5=makeQuery(id+"F2.imprint","IMPRINT",FACE,{"disambiguationData":[TD([[makeQuery(id+"F2.imprint","IMPRINT",EDGE,{"derivedFrom":sQuery(id+"F2.wireOp",EDGE,"E138.0.0")}),1.0]])]});
            var Q6;
            Q6=makeQuery(id+"F2.imprint","IMPRINT",FACE,{"disambiguationData":[TD([[makeQuery(id+"F2.imprint","IMPRINT",EDGE,{"derivedFrom":sQuery(id+"F2.wireOp",EDGE,"E137.0.0")}),1.0]])]});
            var Q7;
            {var subQ0=sQuery(id+"F0.wireOp",EDGE,"E19");var subQ1=sQuery(id+"F0.wireOp",EDGE,"E15");var subQ2=makeQuery(id+"F0.imprint","INTERSECT",VERTEX,{"derivedFrom":[subQ1,subQ0,sQuery(id+"F0.wireOp",EDGE,"E46")]});Q7=makeQuery(id+"F0.imprint","IMPRINT",FACE,{"disambiguationData":[TD([[makeQuery(id+"F0.imprint","IMPRINT",EDGE,{"disambiguationData":[TD([[subQ2,-1.0]])],"derivedFrom":subQ1}),1.0]])]});}
            var Q8;
            Q8=makeQuery(id+"F2.imprint","IMPRINT",FACE,{"disambiguationData":[TD([[makeQuery(id+"F2.imprint","IMPRINT",EDGE,{"derivedFrom":sQuery(id+"F2.wireOp",EDGE,"E135.0.0")}),1.0]])]});
            var Q9;
            Q9=makeQuery(id+"F2.imprint","IMPRINT",FACE,{"disambiguationData":[TD([[makeQuery(id+"F2.imprint","IMPRINT",EDGE,{"derivedFrom":sQuery(id+"F2.wireOp",EDGE,"E134.0.0")}),1.0]])]});
            var Q10;
            Q10=makeQuery(id+"F2.imprint","IMPRINT",FACE,{"disambiguationData":[TD([[makeQuery(id+"F2.imprint","IMPRINT",EDGE,{"derivedFrom":sQuery(id+"F2.wireOp",EDGE,"E133.0.0")}),1.0]])]});
            var Q11;
            {var subQ0=sQuery(id+"F0.wireOp",EDGE,"E18");var subQ1=sQuery(id+"F0.wireOp",EDGE,"E14");var subQ2=makeQuery(id+"F0.imprint","INTERSECT",VERTEX,{"derivedFrom":[subQ1,subQ0,sQuery(id+"F0.wireOp",EDGE,"E46")]});Q11=makeQuery(id+"F0.imprint","IMPRINT",FACE,{"disambiguationData":[TD([[makeQuery(id+"F0.imprint","IMPRINT",EDGE,{"disambiguationData":[TD([[subQ2,-1.0]])],"derivedFrom":subQ1}),1.0]])]});}
            var Q12;
            Q12=makeQuery(id+"F2.imprint","IMPRINT",FACE,{"disambiguationData":[TD([[makeQuery(id+"F2.imprint","IMPRINT",EDGE,{"derivedFrom":sQuery(id+"F2.wireOp",EDGE,"E131.0.0")}),1.0]])]});
            var Q13;
            Q13=makeQuery(id+"F2.imprint","IMPRINT",FACE,{"disambiguationData":[TD([[makeQuery(id+"F2.imprint","IMPRINT",EDGE,{"derivedFrom":sQuery(id+"F2.wireOp",EDGE,"E130.0.0")}),1.0]])]});
            var Q14;
            Q14=makeQuery(id+"F2.imprint","IMPRINT",FACE,{"disambiguationData":[TD([[makeQuery(id+"F2.imprint","IMPRINT",EDGE,{"derivedFrom":sQuery(id+"F2.wireOp",EDGE,"E129.0.0")}),1.0]])]});
            var Q15;
            Q15=makeQuery(id+"F2.imprint","IMPRINT",FACE,{"disambiguationData":[TD([[makeQuery(id+"F2.imprint","IMPRINT",EDGE,{"derivedFrom":sQuery(id+"F2.wireOp",EDGE,"E128.0.0")}),1.0]])]});
            var Q16;
            Q16=makeQuery(id+"F2.imprint","IMPRINT",FACE,{"disambiguationData":[TD([[makeQuery(id+"F2.imprint","IMPRINT",EDGE,{"derivedFrom":sQuery(id+"F2.wireOp",EDGE,"E127.0.0")}),1.0]])]});
            var Q17;
            Q17=makeQuery(id+"F2.imprint","IMPRINT",FACE,{"disambiguationData":[TD([[makeQuery(id+"F2.imprint","IMPRINT",EDGE,{"derivedFrom":sQuery(id+"F2.wireOp",EDGE,"E126.0.0")}),1.0]])]});
            var Q18;
            Q18=makeQuery(id+"F2.imprint","IMPRINT",FACE,{"disambiguationData":[TD([[makeQuery(id+"F2.imprint","IMPRINT",EDGE,{"derivedFrom":sQuery(id+"F2.wireOp",EDGE,"E125.0.0")}),1.0]])]});
            var Q19;
            {var subQ0=sQuery(id+"F0.wireOp",EDGE,"E22");var subQ1=sQuery(id+"F0.wireOp",EDGE,"E12");var subQ2=makeQuery(id+"F0.imprint","INTERSECT",VERTEX,{"derivedFrom":[subQ1,subQ0,sQuery(id+"F0.wireOp",EDGE,"E46")]});Q19=makeQuery(id+"F0.imprint","IMPRINT",FACE,{"disambiguationData":[TD([[makeQuery(id+"F0.imprint","IMPRINT",EDGE,{"disambiguationData":[TD([[subQ2,-1.0]])],"derivedFrom":subQ1}),1.0]])]});}
            var Q20;
            {var subQ0=sQuery(id+"F0.wireOp",EDGE,"E27");var subQ1=sQuery(id+"F0.wireOp",EDGE,"E15");var subQ2=makeQuery(id+"F0.imprint","INTERSECT",VERTEX,{"derivedFrom":[subQ1,subQ0,sQuery(id+"F0.wireOp",EDGE,"E46")]});Q20=makeQuery(id+"F0.imprint","IMPRINT",FACE,{"disambiguationData":[TD([[makeQuery(id+"F0.imprint","IMPRINT",EDGE,{"disambiguationData":[TD([[subQ2,1.0]])],"derivedFrom":subQ1}),1.0]])]});}
            var Q21;
            Q21=makeQuery(id+"F2.imprint","IMPRINT",FACE,{"disambiguationData":[TD([[makeQuery(id+"F2.imprint","IMPRINT",EDGE,{"derivedFrom":sQuery(id+"F2.wireOp",EDGE,"E122.0.0")}),1.0]])]});
            var Q22;
            Q22=makeQuery(id+"F2.imprint","IMPRINT",FACE,{"disambiguationData":[TD([[makeQuery(id+"F2.imprint","IMPRINT",EDGE,{"derivedFrom":sQuery(id+"F2.wireOp",EDGE,"E121.0.0")}),1.0]])]});
            var Q23;
            Q23=makeQuery(id+"F2.imprint","IMPRINT",FACE,{"disambiguationData":[TD([[makeQuery(id+"F2.imprint","IMPRINT",EDGE,{"derivedFrom":sQuery(id+"F2.wireOp",EDGE,"E120.0.0")}),1.0]])]});
            var Q24;
            {var subQ0=sQuery(id+"F0.wireOp",EDGE,"E21");var subQ1=sQuery(id+"F0.wireOp",EDGE,"E3");var subQ2=makeQuery(id+"F0.imprint","INTERSECT",VERTEX,{"derivedFrom":[subQ1,subQ0,sQuery(id+"F0.wireOp",EDGE,"E42")]});Q24=makeQuery(id+"F0.imprint","IMPRINT",FACE,{"disambiguationData":[TD([[makeQuery(id+"F0.imprint","IMPRINT",EDGE,{"disambiguationData":[TD([[subQ2,-1.0]])],"derivedFrom":subQ1}),1.0]])]});}
            var Q25;
            {var subQ0=sQuery(id+"F2.wireOp",EDGE,"E116.0.0");Q25=makeQuery(id+"F2.imprint","IMPRINT",FACE,{"disambiguationData":[TD([[makeQuery(id+"F2.imprint","IMPRINT",EDGE,{"derivedFrom":subQ0}),1.0]])]});}
            var Q26;
            {var subQ0=sQuery(id+"F0.wireOp",EDGE,"E44");var subQ1=sQuery(id+"F0.wireOp",EDGE,"E11");var subQ2=makeQuery(id+"F0.imprint","INTERSECT",VERTEX,{"derivedFrom":[sQuery(id+"F0.wireOp",EDGE,"E6"),subQ1,subQ0]});Q26=makeQuery(id+"F0.imprint","IMPRINT",FACE,{"disambiguationData":[TD([[makeQuery(id+"F0.imprint","IMPRINT",EDGE,{"disambiguationData":[TD([[subQ2,-1.0]])],"derivedFrom":subQ1}),-1.0]])]});}
            var Q27;
            {var subQ0=sQuery(id+"F0.wireOp",EDGE,"E44");var subQ1=sQuery(id+"F0.wireOp",EDGE,"E11");var subQ2=makeQuery(id+"F0.imprint","INTERSECT",VERTEX,{"derivedFrom":[sQuery(id+"F0.wireOp",EDGE,"E6"),subQ1,subQ0]});Q27=makeQuery(id+"F0.imprint","IMPRINT",FACE,{"disambiguationData":[TD([[makeQuery(id+"F0.imprint","IMPRINT",EDGE,{"disambiguationData":[TD([[subQ2,1.0]])],"derivedFrom":subQ1}),1.0]])]});}
            var Q28;
            {var subQ0=sQuery(id+"F0.wireOp",EDGE,"E44");var subQ1=sQuery(id+"F0.wireOp",EDGE,"E5");var subQ2=makeQuery(id+"F0.imprint","INTERSECT",VERTEX,{"derivedFrom":[subQ1,sQuery(id+"F0.wireOp",EDGE,"E15"),subQ0]});Q28=makeQuery(id+"F0.imprint","IMPRINT",FACE,{"disambiguationData":[TD([[makeQuery(id+"F0.imprint","IMPRINT",EDGE,{"disambiguationData":[TD([[subQ2,-1.0]])],"derivedFrom":subQ1}),-1.0]])]});}
            var Q29;
            {var subQ0=sQuery(id+"F2.wireOp",EDGE,"E57.0.1");Q29=makeQuery(id+"F2.imprint","IMPRINT",FACE,{"disambiguationData":[TD([[makeQuery(id+"F2.imprint","IMPRINT",EDGE,{"derivedFrom":subQ0}),1.0]])]});}
            var Q30;
            {var subQ0=sQuery(id+"F2.wireOp",EDGE,"E112.0.0");Q30=makeQuery(id+"F2.imprint","IMPRINT",FACE,{"disambiguationData":[TD([[makeQuery(id+"F2.imprint","IMPRINT",EDGE,{"derivedFrom":subQ0}),1.0]])]});}
            var Q31;
            {var subQ0=sQuery(id+"F0.wireOp",EDGE,"E22");var subQ1=sQuery(id+"F0.wireOp",EDGE,"E5");var subQ2=makeQuery(id+"F0.imprint","INTERSECT",VERTEX,{"derivedFrom":[subQ1,subQ0,sQuery(id+"F0.wireOp",EDGE,"E42")]});Q31=makeQuery(id+"F0.imprint","IMPRINT",FACE,{"disambiguationData":[TD([[makeQuery(id+"F0.imprint","IMPRINT",EDGE,{"disambiguationData":[TD([[subQ2,-1.0]])],"derivedFrom":subQ1}),1.0]])]});}
            var Q32;
            {var subQ0=sQuery(id+"F0.wireOp",EDGE,"E44");var subQ1=sQuery(id+"F0.wireOp",EDGE,"E12");var subQ2=makeQuery(id+"F0.imprint","INTERSECT",VERTEX,{"derivedFrom":[sQuery(id+"F0.wireOp",EDGE,"E4"),subQ1,subQ0]});Q32=makeQuery(id+"F0.imprint","IMPRINT",FACE,{"disambiguationData":[TD([[makeQuery(id+"F0.imprint","IMPRINT",EDGE,{"disambiguationData":[TD([[subQ2,-1.0]])],"derivedFrom":subQ1}),-1.0]])]});}
            var Q33;
            {var subQ0=sQuery(id+"F0.wireOp",EDGE,"E44");var subQ1=sQuery(id+"F0.wireOp",EDGE,"E4");var subQ2=makeQuery(id+"F0.imprint","INTERSECT",VERTEX,{"derivedFrom":[subQ1,sQuery(id+"F0.wireOp",EDGE,"E12"),subQ0]});Q33=makeQuery(id+"F0.imprint","IMPRINT",FACE,{"disambiguationData":[TD([[makeQuery(id+"F0.imprint","IMPRINT",EDGE,{"disambiguationData":[TD([[subQ2,-1.0]])],"derivedFrom":subQ1}),1.0]])]});}
            var Q34;
            {var subQ0=sQuery(id+"F0.wireOp",EDGE,"E19");var subQ1=sQuery(id+"F0.wireOp",EDGE,"E4");var subQ2=makeQuery(id+"F0.imprint","INTERSECT",VERTEX,{"derivedFrom":[subQ1,subQ0,sQuery(id+"F0.wireOp",EDGE,"E46")]});Q34=makeQuery(id+"F0.imprint","IMPRINT",FACE,{"disambiguationData":[TD([[makeQuery(id+"F0.imprint","IMPRINT",EDGE,{"disambiguationData":[TD([[subQ2,-1.0]])],"derivedFrom":subQ1}),-1.0]])]});}
            var Q35;
            {var subQ0=sQuery(id+"F2.wireOp",EDGE,"E60.0.1");Q35=makeQuery(id+"F2.imprint","IMPRINT",FACE,{"disambiguationData":[TD([[makeQuery(id+"F2.imprint","IMPRINT",EDGE,{"derivedFrom":subQ0}),1.0]])]});}
            var Q36;
            {var subQ0=sQuery(id+"F0.wireOp",EDGE,"E44");var subQ1=sQuery(id+"F0.wireOp",EDGE,"E10");var subQ2=makeQuery(id+"F0.imprint","INTERSECT",VERTEX,{"derivedFrom":[sQuery(id+"F0.wireOp",EDGE,"E7"),subQ1,subQ0]});Q36=makeQuery(id+"F0.imprint","IMPRINT",FACE,{"disambiguationData":[TD([[makeQuery(id+"F0.imprint","IMPRINT",EDGE,{"disambiguationData":[TD([[subQ2,-1.0]])],"derivedFrom":subQ1}),1.0]])]});}
            var Q37;
            {var subQ0=sQuery(id+"F2.wireOp",EDGE,"E109.0.0");Q37=makeQuery(id+"F2.imprint","IMPRINT",FACE,{"disambiguationData":[TD([[makeQuery(id+"F2.imprint","IMPRINT",EDGE,{"derivedFrom":subQ0}),1.0]])]});}
            var Q38;
            {var subQ0=sQuery(id+"F2.wireOp",EDGE,"E62.0.1");Q38=makeQuery(id+"F2.imprint","IMPRINT",FACE,{"disambiguationData":[TD([[makeQuery(id+"F2.imprint","IMPRINT",EDGE,{"derivedFrom":subQ0}),1.0]])]});}
            var Q39;
            {var subQ0=sQuery(id+"F2.wireOp",EDGE,"E108.0.0");Q39=makeQuery(id+"F2.imprint","IMPRINT",FACE,{"disambiguationData":[TD([[makeQuery(id+"F2.imprint","IMPRINT",EDGE,{"derivedFrom":subQ0}),1.0]])]});}
            var Q40;
            {var subQ0=sQuery(id+"F2.wireOp",EDGE,"E107.0.0");Q40=makeQuery(id+"F2.imprint","IMPRINT",FACE,{"disambiguationData":[TD([[makeQuery(id+"F2.imprint","IMPRINT",EDGE,{"derivedFrom":subQ0}),1.0]])]});}
            var Q41;
            {var subQ0=sQuery(id+"F2.wireOp",EDGE,"E106.0.0");Q41=makeQuery(id+"F2.imprint","IMPRINT",FACE,{"disambiguationData":[TD([[makeQuery(id+"F2.imprint","IMPRINT",EDGE,{"derivedFrom":subQ0}),1.0]])]});}
            var Q42;
            {var subQ0=sQuery(id+"F2.wireOp",EDGE,"E105.0.0");Q42=makeQuery(id+"F2.imprint","IMPRINT",FACE,{"disambiguationData":[TD([[makeQuery(id+"F2.imprint","IMPRINT",EDGE,{"derivedFrom":subQ0}),1.0]])]});}
            var Q43;
            {var subQ0=sQuery(id+"F2.wireOp",EDGE,"E65.0.0");Q43=makeQuery(id+"F2.imprint","IMPRINT",FACE,{"disambiguationData":[TD([[makeQuery(id+"F2.imprint","IMPRINT",EDGE,{"derivedFrom":subQ0}),1.0]])]});}
            var Q44;
            {var subQ0=sQuery(id+"F2.wireOp",EDGE,"E103.0.0");Q44=makeQuery(id+"F2.imprint","IMPRINT",FACE,{"disambiguationData":[TD([[makeQuery(id+"F2.imprint","IMPRINT",EDGE,{"derivedFrom":subQ0}),1.0]])]});}
            var Q45;
            {var subQ0=sQuery(id+"F2.wireOp",EDGE,"E67.0.0");Q45=makeQuery(id+"F2.imprint","IMPRINT",FACE,{"disambiguationData":[TD([[makeQuery(id+"F2.imprint","IMPRINT",EDGE,{"derivedFrom":subQ0}),1.0]])]});}
            var Q46;
            {var subQ0=sQuery(id+"F2.wireOp",EDGE,"E102.0.0");Q46=makeQuery(id+"F2.imprint","IMPRINT",FACE,{"disambiguationData":[TD([[makeQuery(id+"F2.imprint","IMPRINT",EDGE,{"derivedFrom":subQ0}),1.0]])]});}
            var Q47;
            {var subQ0=sQuery(id+"F2.wireOp",EDGE,"E68.0.1");Q47=makeQuery(id+"F2.imprint","IMPRINT",FACE,{"disambiguationData":[TD([[makeQuery(id+"F2.imprint","IMPRINT",EDGE,{"derivedFrom":subQ0}),1.0]])]});}
            var Q48;
            {var subQ0=sQuery(id+"F2.wireOp",EDGE,"E69.0.1");Q48=makeQuery(id+"F2.imprint","IMPRINT",FACE,{"disambiguationData":[TD([[makeQuery(id+"F2.imprint","IMPRINT",EDGE,{"derivedFrom":subQ0}),1.0]])]});}
            var Q49;
            {var subQ0=sQuery(id+"F2.wireOp",EDGE,"E101.0.0");Q49=makeQuery(id+"F2.imprint","IMPRINT",FACE,{"disambiguationData":[TD([[makeQuery(id+"F2.imprint","IMPRINT",EDGE,{"derivedFrom":subQ0}),1.0]])]});}
            var Q50;
            {var subQ0=sQuery(id+"F2.wireOp",EDGE,"E100.0.0");Q50=makeQuery(id+"F2.imprint","IMPRINT",FACE,{"disambiguationData":[TD([[makeQuery(id+"F2.imprint","IMPRINT",EDGE,{"derivedFrom":subQ0}),1.0]])]});}
            var Q51;
            {var subQ0=sQuery(id+"F0.wireOp",EDGE,"E19");var subQ1=sQuery(id+"F0.wireOp",EDGE,"E6");var subQ2=makeQuery(id+"F0.imprint","INTERSECT",VERTEX,{"derivedFrom":[subQ1,subQ0,sQuery(id+"F0.wireOp",EDGE,"E42")]});Q51=makeQuery(id+"F0.imprint","IMPRINT",FACE,{"disambiguationData":[TD([[makeQuery(id+"F0.imprint","IMPRINT",EDGE,{"disambiguationData":[TD([[subQ2,-1.0]])],"derivedFrom":subQ1}),1.0]])]});}
            var Q52;
            {var subQ0=sQuery(id+"F2.wireOp",EDGE,"E99.0.0");Q52=makeQuery(id+"F2.imprint","IMPRINT",FACE,{"disambiguationData":[TD([[makeQuery(id+"F2.imprint","IMPRINT",EDGE,{"derivedFrom":subQ0}),1.0]])]});}
            var Q53;
            {var subQ0=sQuery(id+"F2.wireOp",EDGE,"E48.0.1");Q53=makeQuery(id+"F2.imprint","IMPRINT",FACE,{"disambiguationData":[TD([[makeQuery(id+"F2.imprint","IMPRINT",EDGE,{"derivedFrom":subQ0}),1.0]])]});}
            var Q54;
            {var subQ0=sQuery(id+"F2.wireOp",EDGE,"E97.0.0");Q54=makeQuery(id+"F2.imprint","IMPRINT",FACE,{"disambiguationData":[TD([[makeQuery(id+"F2.imprint","IMPRINT",EDGE,{"derivedFrom":subQ0}),1.0]])]});}
            var Q55;
            {var subQ0=sQuery(id+"F2.wireOp",EDGE,"E49.0.1");Q55=makeQuery(id+"F2.imprint","IMPRINT",FACE,{"disambiguationData":[TD([[makeQuery(id+"F2.imprint","IMPRINT",EDGE,{"derivedFrom":subQ0}),1.0]])]});}
            var Q56;
            {var subQ0=sQuery(id+"F2.wireOp",EDGE,"E50.0.0");Q56=makeQuery(id+"F2.imprint","IMPRINT",FACE,{"disambiguationData":[TD([[makeQuery(id+"F2.imprint","IMPRINT",EDGE,{"derivedFrom":subQ0}),1.0]])]});}
            var Q57;
            {var subQ0=sQuery(id+"F2.wireOp",EDGE,"E96.0.0");Q57=makeQuery(id+"F2.imprint","IMPRINT",FACE,{"disambiguationData":[TD([[makeQuery(id+"F2.imprint","IMPRINT",EDGE,{"derivedFrom":subQ0}),1.0]])]});}
            var Q58;
            {var subQ0=sQuery(id+"F2.wireOp",EDGE,"E51.0.1");Q58=makeQuery(id+"F2.imprint","IMPRINT",FACE,{"disambiguationData":[TD([[makeQuery(id+"F2.imprint","IMPRINT",EDGE,{"derivedFrom":subQ0}),1.0]])]});}
            var Q59;
            {var subQ0=sQuery(id+"F2.wireOp",EDGE,"E95.0.0");Q59=makeQuery(id+"F2.imprint","IMPRINT",FACE,{"disambiguationData":[TD([[makeQuery(id+"F2.imprint","IMPRINT",EDGE,{"derivedFrom":subQ0}),1.0]])]});}
            var Q60;
            {var subQ0=sQuery(id+"F2.wireOp",EDGE,"E52.0.1");Q60=makeQuery(id+"F2.imprint","IMPRINT",FACE,{"disambiguationData":[TD([[makeQuery(id+"F2.imprint","IMPRINT",EDGE,{"derivedFrom":subQ0}),1.0]])]});}
            var Q61;
            {var subQ0=sQuery(id+"F2.wireOp",EDGE,"E118.0.0");Q61=makeQuery(id+"F2.imprint","IMPRINT",FACE,{"disambiguationData":[TD([[makeQuery(id+"F2.imprint","IMPRINT",EDGE,{"derivedFrom":subQ0}),1.0]])]});}
            var Q62;
            {var subQ0=sQuery(id+"F2.wireOp",EDGE,"E53.0.0");Q62=makeQuery(id+"F2.imprint","IMPRINT",FACE,{"disambiguationData":[TD([[makeQuery(id+"F2.imprint","IMPRINT",EDGE,{"derivedFrom":subQ0}),1.0]])]});}
            var Q63;
            {var subQ0=sQuery(id+"F2.wireOp",EDGE,"E117.0.0");Q63=makeQuery(id+"F2.imprint","IMPRINT",FACE,{"disambiguationData":[TD([[makeQuery(id+"F2.imprint","IMPRINT",EDGE,{"derivedFrom":subQ0}),1.0]])]});}
            var Q64;
            {var subQ0=sQuery(id+"F2.wireOp",EDGE,"E104.0.0");Q64=makeQuery(id+"F2.imprint","IMPRINT",FACE,{"disambiguationData":[TD([[makeQuery(id+"F2.imprint","IMPRINT",EDGE,{"derivedFrom":subQ0}),1.0]])]});}
            var Q65;
            {var subQ0=sQuery(id+"F2.wireOp",EDGE,"E66.0.1");Q65=makeQuery(id+"F2.imprint","IMPRINT",FACE,{"disambiguationData":[TD([[makeQuery(id+"F2.imprint","IMPRINT",EDGE,{"derivedFrom":subQ0}),1.0]])]});}
            var Q66;
            {var subQ0=sQuery(id+"F2.wireOp",EDGE,"E55.0.0");Q66=makeQuery(id+"F2.imprint","IMPRINT",FACE,{"disambiguationData":[TD([[makeQuery(id+"F2.imprint","IMPRINT",EDGE,{"derivedFrom":subQ0}),1.0]])]});}
            var Q67;
            {var subQ0=sQuery(id+"F2.wireOp",EDGE,"E98.0.0");Q67=makeQuery(id+"F2.imprint","IMPRINT",FACE,{"disambiguationData":[TD([[makeQuery(id+"F2.imprint","IMPRINT",EDGE,{"derivedFrom":subQ0}),1.0]])]});}
            var Q68;
            {var subQ0=sQuery(id+"F0.wireOp",EDGE,"E44");var subQ1=sQuery(id+"F0.wireOp",EDGE,"E7");var subQ2=makeQuery(id+"F0.imprint","INTERSECT",VERTEX,{"derivedFrom":[subQ1,sQuery(id+"F0.wireOp",EDGE,"E15"),subQ0]});Q68=makeQuery(id+"F0.imprint","IMPRINT",FACE,{"disambiguationData":[TD([[makeQuery(id+"F0.imprint","IMPRINT",EDGE,{"disambiguationData":[TD([[subQ2,-1.0]])],"derivedFrom":subQ1}),1.0]])]});}
            var Q69;
            {var subQ0=sQuery(id+"F0.wireOp",EDGE,"E21");var subQ1=sQuery(id+"F0.wireOp",EDGE,"E17");var subQ2=makeQuery(id+"F0.imprint","INTERSECT",VERTEX,{"derivedFrom":[sQuery(id+"F0.wireOp",EDGE,"E0"),subQ1,subQ0]});Q69=makeQuery(id+"F0.imprint","IMPRINT",FACE,{"disambiguationData":[TD([[makeQuery(id+"F0.imprint","IMPRINT",EDGE,{"disambiguationData":[TD([[subQ2,-1.0]])],"derivedFrom":subQ1}),1.0]])]});}
            var Q70;
            {var subQ0=sQuery(id+"F0.wireOp",EDGE,"E6");var subQ1=sQuery(id+"F0.wireOp",EDGE,"E3");var subQ2=makeQuery(id+"F0.imprint","INTERSECT",VERTEX,{"derivedFrom":[sQuery(id+"F0.wireOp",EDGE,"E0"),subQ1,subQ0]});Q70=makeQuery(id+"F0.imprint","IMPRINT",FACE,{"disambiguationData":[TD([[makeQuery(id+"F0.imprint","IMPRINT",EDGE,{"disambiguationData":[TD([[subQ2,-1.0]])],"derivedFrom":subQ1}),1.0]])]});}
            var Q71;
            {var subQ0=sQuery(id+"F0.wireOp",EDGE,"E26");var subQ1=sQuery(id+"F0.wireOp",EDGE,"E24");var subQ2=makeQuery(id+"F0.imprint","INTERSECT",VERTEX,{"derivedFrom":[sQuery(id+"F0.wireOp",EDGE,"E0"),subQ1,subQ0]});Q71=makeQuery(id+"F0.imprint","IMPRINT",FACE,{"disambiguationData":[TD([[makeQuery(id+"F0.imprint","IMPRINT",EDGE,{"disambiguationData":[TD([[subQ2,1.0]])],"derivedFrom":subQ1}),1.0]])]});}
            var Q72;
            {var subQ0=sQuery(id+"F0.wireOp",EDGE,"E15");var subQ1=sQuery(id+"F0.wireOp",EDGE,"E11");var subQ2=makeQuery(id+"F0.imprint","INTERSECT",VERTEX,{"derivedFrom":[sQuery(id+"F0.wireOp",EDGE,"E0"),subQ1,subQ0]});Q72=makeQuery(id+"F0.imprint","IMPRINT",FACE,{"disambiguationData":[TD([[makeQuery(id+"F0.imprint","IMPRINT",EDGE,{"disambiguationData":[TD([[subQ2,-1.0]])],"derivedFrom":subQ1}),1.0]])]});}
            var Q73;
            {var subQ0=sQuery(id+"F0.wireOp",EDGE,"E22");var subQ1=sQuery(id+"F0.wireOp",EDGE,"E18");var subQ2=makeQuery(id+"F0.imprint","INTERSECT",VERTEX,{"derivedFrom":[sQuery(id+"F0.wireOp",EDGE,"E0"),subQ1,subQ0]});Q73=makeQuery(id+"F0.imprint","IMPRINT",FACE,{"disambiguationData":[TD([[makeQuery(id+"F0.imprint","IMPRINT",EDGE,{"disambiguationData":[TD([[subQ2,-1.0]])],"derivedFrom":subQ1}),1.0]])]});}
            var Q74;
            {var subQ0=sQuery(id+"F0.wireOp",EDGE,"E5");var subQ1=sQuery(id+"F0.wireOp",EDGE,"E4");var subQ2=makeQuery(id+"F0.imprint","INTERSECT",VERTEX,{"derivedFrom":[sQuery(id+"F0.wireOp",EDGE,"E0"),subQ1,subQ0]});Q74=makeQuery(id+"F0.imprint","IMPRINT",FACE,{"disambiguationData":[TD([[makeQuery(id+"F0.imprint","IMPRINT",EDGE,{"disambiguationData":[TD([[subQ2,1.0]])],"derivedFrom":subQ1}),1.0]])]});}
            var Q75;
            {var subQ0=sQuery(id+"F0.wireOp",EDGE,"E27");var subQ1=sQuery(id+"F0.wireOp",EDGE,"E25");var subQ2=makeQuery(id+"F0.imprint","INTERSECT",VERTEX,{"derivedFrom":[sQuery(id+"F0.wireOp",EDGE,"E0"),subQ1,subQ0]});Q75=makeQuery(id+"F0.imprint","IMPRINT",FACE,{"disambiguationData":[TD([[makeQuery(id+"F0.imprint","IMPRINT",EDGE,{"disambiguationData":[TD([[subQ2,1.0]])],"derivedFrom":subQ1}),1.0]])]});}
            var Q76;
            {var subQ0=sQuery(id+"F0.wireOp",EDGE,"E12");var subQ1=sQuery(id+"F0.wireOp",EDGE,"E10");var subQ2=makeQuery(id+"F0.imprint","INTERSECT",VERTEX,{"derivedFrom":[sQuery(id+"F0.wireOp",EDGE,"E0"),subQ1,subQ0]});Q76=makeQuery(id+"F0.imprint","IMPRINT",FACE,{"disambiguationData":[TD([[makeQuery(id+"F0.imprint","IMPRINT",EDGE,{"disambiguationData":[TD([[subQ2,1.0]])],"derivedFrom":subQ1}),1.0]])]});}
            var Q77;
            {var subQ0=sQuery(id+"F0.wireOp",EDGE,"E19");var subQ1=sQuery(id+"F0.wireOp",EDGE,"E17");var subQ2=makeQuery(id+"F0.imprint","INTERSECT",VERTEX,{"derivedFrom":[sQuery(id+"F0.wireOp",EDGE,"E0"),subQ1,subQ0]});Q77=makeQuery(id+"F0.imprint","IMPRINT",FACE,{"disambiguationData":[TD([[makeQuery(id+"F0.imprint","IMPRINT",EDGE,{"disambiguationData":[TD([[subQ2,1.0]])],"derivedFrom":subQ1}),1.0]])]});}
            var Q78;
            {var subQ0=sQuery(id+"F0.wireOp",EDGE,"E29");var subQ1=sQuery(id+"F0.wireOp",EDGE,"E27");var subQ2=makeQuery(id+"F0.imprint","INTERSECT",VERTEX,{"derivedFrom":[sQuery(id+"F0.wireOp",EDGE,"E0"),subQ1,subQ0]});Q78=makeQuery(id+"F0.imprint","IMPRINT",FACE,{"disambiguationData":[TD([[makeQuery(id+"F0.imprint","IMPRINT",EDGE,{"disambiguationData":[TD([[subQ2,1.0]])],"derivedFrom":subQ1}),1.0]])]});}
            var Q79;
            {var subQ0=sQuery(id+"F0.wireOp",EDGE,"E7");var subQ1=sQuery(id+"F0.wireOp",EDGE,"E6");var subQ2=makeQuery(id+"F0.imprint","INTERSECT",VERTEX,{"derivedFrom":[sQuery(id+"F0.wireOp",EDGE,"E0"),subQ1,subQ0]});Q79=makeQuery(id+"F0.imprint","IMPRINT",FACE,{"disambiguationData":[TD([[makeQuery(id+"F0.imprint","IMPRINT",EDGE,{"disambiguationData":[TD([[subQ2,-1.0]])],"derivedFrom":subQ1}),1.0]])]});}
            var Q80;
            {var subQ0=sQuery(id+"F0.wireOp",EDGE,"E28");var subQ1=sQuery(id+"F0.wireOp",EDGE,"E24");var subQ2=makeQuery(id+"F0.imprint","INTERSECT",VERTEX,{"derivedFrom":[sQuery(id+"F0.wireOp",EDGE,"E0"),subQ1,subQ0]});Q80=makeQuery(id+"F0.imprint","IMPRINT",FACE,{"disambiguationData":[TD([[makeQuery(id+"F0.imprint","IMPRINT",EDGE,{"disambiguationData":[TD([[subQ2,-1.0]])],"derivedFrom":subQ1}),1.0]])]});}
            var Q81;
            {var subQ0=sQuery(id+"F0.wireOp",EDGE,"E15");var subQ1=sQuery(id+"F0.wireOp",EDGE,"E13");var subQ2=makeQuery(id+"F0.imprint","INTERSECT",VERTEX,{"derivedFrom":[sQuery(id+"F0.wireOp",EDGE,"E0"),subQ1,subQ0]});Q81=makeQuery(id+"F0.imprint","IMPRINT",FACE,{"disambiguationData":[TD([[makeQuery(id+"F0.imprint","IMPRINT",EDGE,{"disambiguationData":[TD([[subQ2,1.0]])],"derivedFrom":subQ1}),1.0]])]});}
            var Q82;
            {var subQ0=sQuery(id+"F0.wireOp",EDGE,"E22");var subQ1=sQuery(id+"F0.wireOp",EDGE,"E20");var subQ2=makeQuery(id+"F0.imprint","INTERSECT",VERTEX,{"derivedFrom":[sQuery(id+"F0.wireOp",EDGE,"E0"),subQ1,subQ0]});Q82=makeQuery(id+"F0.imprint","IMPRINT",FACE,{"disambiguationData":[TD([[makeQuery(id+"F0.imprint","IMPRINT",EDGE,{"disambiguationData":[TD([[subQ2,1.0]])],"derivedFrom":subQ1}),1.0]])]});}
            var Q83;
            {var subQ0=sQuery(id+"F0.wireOp",EDGE,"E8");var subQ1=sQuery(id+"F0.wireOp",EDGE,"E4");var subQ2=makeQuery(id+"F0.imprint","INTERSECT",VERTEX,{"derivedFrom":[sQuery(id+"F0.wireOp",EDGE,"E0"),subQ1,subQ0]});Q83=makeQuery(id+"F0.imprint","IMPRINT",FACE,{"disambiguationData":[TD([[makeQuery(id+"F0.imprint","IMPRINT",EDGE,{"disambiguationData":[TD([[subQ2,-1.0]])],"derivedFrom":subQ1}),1.0]])]});}
            var Q84;
            {var subQ0=sQuery(id+"F0.wireOp",EDGE,"E29");var subQ1=sQuery(id+"F0.wireOp",EDGE,"E25");var subQ2=makeQuery(id+"F0.imprint","INTERSECT",VERTEX,{"derivedFrom":[sQuery(id+"F0.wireOp",EDGE,"E0"),subQ1,subQ0]});Q84=makeQuery(id+"F0.imprint","IMPRINT",FACE,{"disambiguationData":[TD([[makeQuery(id+"F0.imprint","IMPRINT",EDGE,{"disambiguationData":[TD([[subQ2,-1.0]])],"derivedFrom":subQ1}),1.0]])]});}
            var Q85;
            {var subQ0=sQuery(id+"F0.wireOp",EDGE,"E14");var subQ1=sQuery(id+"F0.wireOp",EDGE,"E10");var subQ2=makeQuery(id+"F0.imprint","INTERSECT",VERTEX,{"derivedFrom":[sQuery(id+"F0.wireOp",EDGE,"E0"),subQ1,subQ0]});Q85=makeQuery(id+"F0.imprint","IMPRINT",FACE,{"disambiguationData":[TD([[makeQuery(id+"F0.imprint","IMPRINT",EDGE,{"disambiguationData":[TD([[subQ2,-1.0]])],"derivedFrom":subQ1}),1.0]])]});}
            var Q86;
            {var subQ0=sQuery(id+"F2.wireOp",EDGE,"E63.0.0");Q86=makeQuery(id+"F2.imprint","IMPRINT",FACE,{"disambiguationData":[TD([[makeQuery(id+"F2.imprint","IMPRINT",EDGE,{"derivedFrom":subQ0}),1.0]])]});}
            var Q87;
            {var subQ0=sQuery(id+"F2.wireOp",EDGE,"E64.0.1");Q87=makeQuery(id+"F2.imprint","IMPRINT",FACE,{"disambiguationData":[TD([[makeQuery(id+"F2.imprint","IMPRINT",EDGE,{"derivedFrom":subQ0}),1.0]])]});}
            var Q88;
            {var subQ0=sQuery(id+"F0.wireOp",EDGE,"E21");var subQ1=sQuery(id+"F0.wireOp",EDGE,"E19");var subQ2=makeQuery(id+"F0.imprint","INTERSECT",VERTEX,{"derivedFrom":[sQuery(id+"F0.wireOp",EDGE,"E0"),subQ1,subQ0]});Q88=makeQuery(id+"F0.imprint","IMPRINT",FACE,{"disambiguationData":[TD([[makeQuery(id+"F0.imprint","IMPRINT",EDGE,{"disambiguationData":[TD([[subQ2,1.0]])],"derivedFrom":subQ1}),1.0]])]});}
            var Q89;
            {var subQ0=sQuery(id+"F0.wireOp",EDGE,"E14");var subQ1=sQuery(id+"F0.wireOp",EDGE,"E12");var subQ2=makeQuery(id+"F0.imprint","INTERSECT",VERTEX,{"derivedFrom":[sQuery(id+"F0.wireOp",EDGE,"E0"),subQ1,subQ0]});Q89=makeQuery(id+"F0.imprint","IMPRINT",FACE,{"disambiguationData":[TD([[makeQuery(id+"F0.imprint","IMPRINT",EDGE,{"disambiguationData":[TD([[subQ2,1.0]])],"derivedFrom":subQ1}),1.0]])]});}
            var Q90;
            {var subQ0=sQuery(id+"F0.wireOp",EDGE,"E8");var subQ1=sQuery(id+"F0.wireOp",EDGE,"E5");var subQ2=makeQuery(id+"F0.imprint","INTERSECT",VERTEX,{"derivedFrom":[sQuery(id+"F0.wireOp",EDGE,"E0"),subQ1,subQ0]});Q90=makeQuery(id+"F0.imprint","IMPRINT",FACE,{"disambiguationData":[TD([[makeQuery(id+"F0.imprint","IMPRINT",EDGE,{"disambiguationData":[TD([[subQ2,1.0]])],"derivedFrom":subQ1}),1.0]])]});}
            var Q91;
            {var subQ0=sQuery(id+"F0.wireOp",EDGE,"E20");var subQ1=sQuery(id+"F0.wireOp",EDGE,"E18");var subQ2=makeQuery(id+"F0.imprint","INTERSECT",VERTEX,{"derivedFrom":[sQuery(id+"F0.wireOp",EDGE,"E0"),subQ1,subQ0]});Q91=makeQuery(id+"F0.imprint","IMPRINT",FACE,{"disambiguationData":[TD([[makeQuery(id+"F0.imprint","IMPRINT",EDGE,{"disambiguationData":[TD([[subQ2,1.0]])],"derivedFrom":subQ1}),1.0]])]});}
            var Q92;
            {var subQ0=sQuery(id+"F0.wireOp",EDGE,"E13");var subQ1=sQuery(id+"F0.wireOp",EDGE,"E11");var subQ2=makeQuery(id+"F0.imprint","INTERSECT",VERTEX,{"derivedFrom":[sQuery(id+"F0.wireOp",EDGE,"E0"),subQ1,subQ0]});Q92=makeQuery(id+"F0.imprint","IMPRINT",FACE,{"disambiguationData":[TD([[makeQuery(id+"F0.imprint","IMPRINT",EDGE,{"disambiguationData":[TD([[subQ2,1.0]])],"derivedFrom":subQ1}),1.0]])]});}
            var Q93;
            {var subQ0=sQuery(id+"F0.wireOp",EDGE,"E28");var subQ1=sQuery(id+"F0.wireOp",EDGE,"E26");var subQ2=makeQuery(id+"F0.imprint","INTERSECT",VERTEX,{"derivedFrom":[sQuery(id+"F0.wireOp",EDGE,"E0"),subQ1,subQ0]});Q93=makeQuery(id+"F0.imprint","IMPRINT",FACE,{"disambiguationData":[TD([[makeQuery(id+"F0.imprint","IMPRINT",EDGE,{"disambiguationData":[TD([[subQ2,1.0]])],"derivedFrom":subQ1}),1.0]])]});}
            var Q94;
            {var subQ0=sQuery(id+"F0.wireOp",EDGE,"E7");var subQ1=sQuery(id+"F0.wireOp",EDGE,"E3");var subQ2=makeQuery(id+"F0.imprint","INTERSECT",VERTEX,{"derivedFrom":[sQuery(id+"F0.wireOp",EDGE,"E0"),subQ1,subQ0]});Q94=makeQuery(id+"F0.imprint","IMPRINT",FACE,{"disambiguationData":[TD([[makeQuery(id+"F0.imprint","IMPRINT",EDGE,{"disambiguationData":[TD([[subQ2,1.0]])],"derivedFrom":subQ1}),1.0]])]});}
            var Q95;
            {var subQ0=sQuery(id+"F0.wireOp",EDGE,"E21");var subQ1=sQuery(id+"F0.wireOp",EDGE,"E0");var subQ2=makeQuery(id+"F0.imprint","INTERSECT",VERTEX,{"derivedFrom":[subQ1,sQuery(id+"F0.wireOp",EDGE,"E17"),subQ0]});Q95=makeQuery(id+"F0.imprint","IMPRINT",FACE,{"disambiguationData":[TD([[makeQuery(id+"F0.imprint","IMPRINT",EDGE,{"disambiguationData":[TD([[subQ2,-1.0]])],"derivedFrom":subQ1}),-1.0]])]});}
            var Q96;
            {var subQ0=sQuery(id+"F0.wireOp",EDGE,"E6");var subQ1=sQuery(id+"F0.wireOp",EDGE,"E0");var subQ2=makeQuery(id+"F0.imprint","INTERSECT",VERTEX,{"derivedFrom":[subQ1,sQuery(id+"F0.wireOp",EDGE,"E3"),subQ0]});Q96=makeQuery(id+"F0.imprint","IMPRINT",FACE,{"disambiguationData":[TD([[makeQuery(id+"F0.imprint","IMPRINT",EDGE,{"disambiguationData":[TD([[subQ2,-1.0]])],"derivedFrom":subQ1}),-1.0]])]});}
            var Q97;
            {var subQ0=sQuery(id+"F0.wireOp",EDGE,"E24");var subQ1=sQuery(id+"F0.wireOp",EDGE,"E0");var subQ2=makeQuery(id+"F0.imprint","INTERSECT",VERTEX,{"derivedFrom":[subQ1,subQ0,sQuery(id+"F0.wireOp",EDGE,"E26")]});Q97=makeQuery(id+"F0.imprint","IMPRINT",FACE,{"disambiguationData":[TD([[makeQuery(id+"F0.imprint","IMPRINT",EDGE,{"disambiguationData":[TD([[subQ2,-1.0]])],"derivedFrom":subQ1}),-1.0]])]});}
            var Q98;
            {var subQ0=sQuery(id+"F0.wireOp",EDGE,"E18");var subQ1=sQuery(id+"F0.wireOp",EDGE,"E0");var subQ2=makeQuery(id+"F0.imprint","INTERSECT",VERTEX,{"derivedFrom":[subQ1,subQ0,sQuery(id+"F0.wireOp",EDGE,"E22")]});Q98=makeQuery(id+"F0.imprint","IMPRINT",FACE,{"disambiguationData":[TD([[makeQuery(id+"F0.imprint","IMPRINT",EDGE,{"disambiguationData":[TD([[subQ2,1.0]])],"derivedFrom":subQ1}),-1.0]])]});}
            var Q99;
            {var subQ0=sQuery(id+"F0.wireOp",EDGE,"E5");var subQ1=sQuery(id+"F0.wireOp",EDGE,"E0");var subQ2=makeQuery(id+"F0.imprint","INTERSECT",VERTEX,{"derivedFrom":[subQ1,sQuery(id+"F0.wireOp",EDGE,"E4"),subQ0]});Q99=makeQuery(id+"F0.imprint","IMPRINT",FACE,{"disambiguationData":[TD([[makeQuery(id+"F0.imprint","IMPRINT",EDGE,{"disambiguationData":[TD([[subQ2,1.0]])],"derivedFrom":subQ1}),-1.0]])]});}
            var Q100;
            {var subQ0=sQuery(id+"F0.wireOp",EDGE,"E22");var subQ1=sQuery(id+"F0.wireOp",EDGE,"E0");var subQ2=makeQuery(id+"F0.imprint","INTERSECT",VERTEX,{"derivedFrom":[subQ1,sQuery(id+"F0.wireOp",EDGE,"E18"),subQ0]});Q100=makeQuery(id+"F0.imprint","IMPRINT",FACE,{"disambiguationData":[TD([[makeQuery(id+"F0.imprint","IMPRINT",EDGE,{"disambiguationData":[TD([[subQ2,-1.0]])],"derivedFrom":subQ1}),-1.0]])]});}
            var Q101;
            {var subQ0=sQuery(id+"F0.wireOp",EDGE,"E15");var subQ1=sQuery(id+"F0.wireOp",EDGE,"E0");var subQ2=makeQuery(id+"F0.imprint","INTERSECT",VERTEX,{"derivedFrom":[subQ1,sQuery(id+"F0.wireOp",EDGE,"E11"),subQ0]});Q101=makeQuery(id+"F0.imprint","IMPRINT",FACE,{"disambiguationData":[TD([[makeQuery(id+"F0.imprint","IMPRINT",EDGE,{"disambiguationData":[TD([[subQ2,-1.0]])],"derivedFrom":subQ1}),-1.0]])]});}
            var Q102;
            {var subQ0=sQuery(id+"F0.wireOp",EDGE,"E17");var subQ1=sQuery(id+"F0.wireOp",EDGE,"E0");var subQ2=makeQuery(id+"F0.imprint","INTERSECT",VERTEX,{"derivedFrom":[subQ1,subQ0,sQuery(id+"F0.wireOp",EDGE,"E19")]});Q102=makeQuery(id+"F0.imprint","IMPRINT",FACE,{"disambiguationData":[TD([[makeQuery(id+"F0.imprint","IMPRINT",EDGE,{"disambiguationData":[TD([[subQ2,-1.0]])],"derivedFrom":subQ1}),-1.0]])]});}
            var Q103;
            {var subQ0=sQuery(id+"F0.wireOp",EDGE,"E3");var subQ1=sQuery(id+"F0.wireOp",EDGE,"E0");var subQ2=makeQuery(id+"F0.imprint","INTERSECT",VERTEX,{"derivedFrom":[subQ1,subQ0,sQuery(id+"F0.wireOp",EDGE,"E7")]});Q103=makeQuery(id+"F0.imprint","IMPRINT",FACE,{"disambiguationData":[TD([[makeQuery(id+"F0.imprint","IMPRINT",EDGE,{"disambiguationData":[TD([[subQ2,-1.0]])],"derivedFrom":subQ1}),-1.0]])]});}
            var Q104;
            {var subQ0=sQuery(id+"F0.wireOp",EDGE,"E26");var subQ1=sQuery(id+"F0.wireOp",EDGE,"E0");var subQ2=makeQuery(id+"F0.imprint","INTERSECT",VERTEX,{"derivedFrom":[subQ1,subQ0,sQuery(id+"F0.wireOp",EDGE,"E28")]});Q104=makeQuery(id+"F0.imprint","IMPRINT",FACE,{"disambiguationData":[TD([[makeQuery(id+"F0.imprint","IMPRINT",EDGE,{"disambiguationData":[TD([[subQ2,-1.0]])],"derivedFrom":subQ1}),-1.0]])]});}
            var Q105;
            {var subQ0=sQuery(id+"F0.wireOp",EDGE,"E11");var subQ1=sQuery(id+"F0.wireOp",EDGE,"E0");var subQ2=makeQuery(id+"F0.imprint","INTERSECT",VERTEX,{"derivedFrom":[subQ1,subQ0,sQuery(id+"F0.wireOp",EDGE,"E13")]});Q105=makeQuery(id+"F0.imprint","IMPRINT",FACE,{"disambiguationData":[TD([[makeQuery(id+"F0.imprint","IMPRINT",EDGE,{"disambiguationData":[TD([[subQ2,-1.0]])],"derivedFrom":subQ1}),-1.0]])]});}
            var Q106;
            {var subQ0=sQuery(id+"F0.wireOp",EDGE,"E18");var subQ1=sQuery(id+"F0.wireOp",EDGE,"E0");var subQ2=makeQuery(id+"F0.imprint","INTERSECT",VERTEX,{"derivedFrom":[subQ1,subQ0,sQuery(id+"F0.wireOp",EDGE,"E20")]});Q106=makeQuery(id+"F0.imprint","IMPRINT",FACE,{"disambiguationData":[TD([[makeQuery(id+"F0.imprint","IMPRINT",EDGE,{"disambiguationData":[TD([[subQ2,-1.0]])],"derivedFrom":subQ1}),-1.0]])]});}
            var Q107;
            {var subQ0=sQuery(id+"F0.wireOp",EDGE,"E5");var subQ1=sQuery(id+"F0.wireOp",EDGE,"E0");var subQ2=makeQuery(id+"F0.imprint","INTERSECT",VERTEX,{"derivedFrom":[subQ1,subQ0,sQuery(id+"F0.wireOp",EDGE,"E8")]});Q107=makeQuery(id+"F0.imprint","IMPRINT",FACE,{"disambiguationData":[TD([[makeQuery(id+"F0.imprint","IMPRINT",EDGE,{"disambiguationData":[TD([[subQ2,-1.0]])],"derivedFrom":subQ1}),-1.0]])]});}
            var Q108;
            {var subQ0=sQuery(id+"F0.wireOp",EDGE,"E27");var subQ1=sQuery(id+"F0.wireOp",EDGE,"E0");var subQ2=makeQuery(id+"F0.imprint","INTERSECT",VERTEX,{"derivedFrom":[subQ1,subQ0,sQuery(id+"F0.wireOp",EDGE,"E29")]});Q108=makeQuery(id+"F0.imprint","IMPRINT",FACE,{"disambiguationData":[TD([[makeQuery(id+"F0.imprint","IMPRINT",EDGE,{"disambiguationData":[TD([[subQ2,-1.0]])],"derivedFrom":subQ1}),-1.0]])]});}
            var Q109;
            {var subQ0=sQuery(id+"F0.wireOp",EDGE,"E12");var subQ1=sQuery(id+"F0.wireOp",EDGE,"E0");var subQ2=makeQuery(id+"F0.imprint","INTERSECT",VERTEX,{"derivedFrom":[subQ1,subQ0,sQuery(id+"F0.wireOp",EDGE,"E14")]});Q109=makeQuery(id+"F0.imprint","IMPRINT",FACE,{"disambiguationData":[TD([[makeQuery(id+"F0.imprint","IMPRINT",EDGE,{"disambiguationData":[TD([[subQ2,-1.0]])],"derivedFrom":subQ1}),-1.0]])]});}
            var Q110;
            {var subQ0=sQuery(id+"F0.wireOp",EDGE,"E19");var subQ1=sQuery(id+"F0.wireOp",EDGE,"E0");var subQ2=makeQuery(id+"F0.imprint","INTERSECT",VERTEX,{"derivedFrom":[subQ1,subQ0,sQuery(id+"F0.wireOp",EDGE,"E21")]});Q110=makeQuery(id+"F0.imprint","IMPRINT",FACE,{"disambiguationData":[TD([[makeQuery(id+"F0.imprint","IMPRINT",EDGE,{"disambiguationData":[TD([[subQ2,-1.0]])],"derivedFrom":subQ1}),-1.0]])]});}
            var Q111;
            {var subQ0=sQuery(id+"F0.wireOp",EDGE,"E7");var subQ1=sQuery(id+"F0.wireOp",EDGE,"E0");var subQ2=makeQuery(id+"F0.imprint","INTERSECT",VERTEX,{"derivedFrom":[subQ1,sQuery(id+"F0.wireOp",EDGE,"E6"),subQ0]});Q111=makeQuery(id+"F0.imprint","IMPRINT",FACE,{"disambiguationData":[TD([[makeQuery(id+"F0.imprint","IMPRINT",EDGE,{"disambiguationData":[TD([[subQ2,-1.0]])],"derivedFrom":subQ1}),-1.0]])]});}
            var Q112;
            {var subQ0=sQuery(id+"F0.wireOp",EDGE,"E13");var subQ1=sQuery(id+"F0.wireOp",EDGE,"E0");var subQ2=makeQuery(id+"F0.imprint","INTERSECT",VERTEX,{"derivedFrom":[subQ1,subQ0,sQuery(id+"F0.wireOp",EDGE,"E15")]});Q112=makeQuery(id+"F0.imprint","IMPRINT",FACE,{"disambiguationData":[TD([[makeQuery(id+"F0.imprint","IMPRINT",EDGE,{"disambiguationData":[TD([[subQ2,-1.0]])],"derivedFrom":subQ1}),-1.0]])]});}
            var Q113;
            {var subQ0=sQuery(id+"F0.wireOp",EDGE,"E28");var subQ1=sQuery(id+"F0.wireOp",EDGE,"E0");var subQ2=makeQuery(id+"F0.imprint","INTERSECT",VERTEX,{"derivedFrom":[subQ1,sQuery(id+"F0.wireOp",EDGE,"E24"),subQ0]});Q113=makeQuery(id+"F0.imprint","IMPRINT",FACE,{"disambiguationData":[TD([[makeQuery(id+"F0.imprint","IMPRINT",EDGE,{"disambiguationData":[TD([[subQ2,-1.0]])],"derivedFrom":subQ1}),-1.0]])]});}
            var Q114;
            {var subQ0=sQuery(id+"F0.wireOp",EDGE,"E20");var subQ1=sQuery(id+"F0.wireOp",EDGE,"E0");var subQ2=makeQuery(id+"F0.imprint","INTERSECT",VERTEX,{"derivedFrom":[subQ1,subQ0,sQuery(id+"F0.wireOp",EDGE,"E22")]});Q114=makeQuery(id+"F0.imprint","IMPRINT",FACE,{"disambiguationData":[TD([[makeQuery(id+"F0.imprint","IMPRINT",EDGE,{"disambiguationData":[TD([[subQ2,-1.0]])],"derivedFrom":subQ1}),-1.0]])]});}
            var Q115;
            {var subQ0=sQuery(id+"F0.wireOp",EDGE,"E8");var subQ1=sQuery(id+"F0.wireOp",EDGE,"E0");var subQ2=makeQuery(id+"F0.imprint","INTERSECT",VERTEX,{"derivedFrom":[subQ1,sQuery(id+"F0.wireOp",EDGE,"E4"),subQ0]});Q115=makeQuery(id+"F0.imprint","IMPRINT",FACE,{"disambiguationData":[TD([[makeQuery(id+"F0.imprint","IMPRINT",EDGE,{"disambiguationData":[TD([[subQ2,-1.0]])],"derivedFrom":subQ1}),-1.0]])]});}
            var Q116;
            {var subQ0=sQuery(id+"F0.wireOp",EDGE,"E29");var subQ1=sQuery(id+"F0.wireOp",EDGE,"E0");var subQ2=makeQuery(id+"F0.imprint","INTERSECT",VERTEX,{"derivedFrom":[subQ1,sQuery(id+"F0.wireOp",EDGE,"E25"),subQ0]});Q116=makeQuery(id+"F0.imprint","IMPRINT",FACE,{"disambiguationData":[TD([[makeQuery(id+"F0.imprint","IMPRINT",EDGE,{"disambiguationData":[TD([[subQ2,-1.0]])],"derivedFrom":subQ1}),-1.0]])]});}
            var Q117;
            {var subQ0=sQuery(id+"F0.wireOp",EDGE,"E14");var subQ1=sQuery(id+"F0.wireOp",EDGE,"E0");var subQ2=makeQuery(id+"F0.imprint","INTERSECT",VERTEX,{"derivedFrom":[subQ1,sQuery(id+"F0.wireOp",EDGE,"E10"),subQ0]});Q117=makeQuery(id+"F0.imprint","IMPRINT",FACE,{"disambiguationData":[TD([[makeQuery(id+"F0.imprint","IMPRINT",EDGE,{"disambiguationData":[TD([[subQ2,-1.0]])],"derivedFrom":subQ1}),-1.0]])]});}
            var Q118;
            {var subQ0=sQuery(id+"F0.wireOp",EDGE,"E10");var subQ1=sQuery(id+"F0.wireOp",EDGE,"E0");var subQ2=makeQuery(id+"F0.imprint","INTERSECT",VERTEX,{"derivedFrom":[subQ1,subQ0,sQuery(id+"F0.wireOp",EDGE,"E12")]});Q118=makeQuery(id+"F0.imprint","IMPRINT",FACE,{"disambiguationData":[TD([[makeQuery(id+"F0.imprint","IMPRINT",EDGE,{"disambiguationData":[TD([[subQ2,-1.0]])],"derivedFrom":subQ1}),-1.0]])]});}
            var Q119;
            {var subQ0=sQuery(id+"F0.wireOp",EDGE,"E18");var subQ1=sQuery(id+"F0.wireOp",EDGE,"E6");var subQ2=makeQuery(id+"F0.imprint","INTERSECT",VERTEX,{"derivedFrom":[subQ1,subQ0,sQuery(id+"F0.wireOp",EDGE,"E46")]});Q119=makeQuery(id+"F0.imprint","IMPRINT",FACE,{"disambiguationData":[TD([[makeQuery(id+"F0.imprint","IMPRINT",EDGE,{"disambiguationData":[TD([[subQ2,-1.0]])],"derivedFrom":subQ1}),-1.0]])]});}
            var Q120;
            {var subQ0=sQuery(id+"F0.wireOp",EDGE,"E30");var subQ1=sQuery(id+"F0.wireOp",EDGE,"E6");var subQ2=makeQuery(id+"F0.imprint","INTERSECT",VERTEX,{"derivedFrom":[subQ1,sQuery(id+"F0.wireOp",EDGE,"E17"),subQ0]});Q120=makeQuery(id+"F0.imprint","IMPRINT",FACE,{"disambiguationData":[TD([[makeQuery(id+"F0.imprint","IMPRINT",EDGE,{"disambiguationData":[TD([[subQ2,-1.0]])],"derivedFrom":subQ1}),1.0]])]});}
            var Q121;
            {var subQ0=sQuery(id+"F0.wireOp",EDGE,"E30");var subQ1=sQuery(id+"F0.wireOp",EDGE,"E17");var subQ2=makeQuery(id+"F0.imprint","INTERSECT",VERTEX,{"derivedFrom":[sQuery(id+"F0.wireOp",EDGE,"E6"),subQ1,subQ0]});Q121=makeQuery(id+"F0.imprint","IMPRINT",FACE,{"disambiguationData":[TD([[makeQuery(id+"F0.imprint","IMPRINT",EDGE,{"disambiguationData":[TD([[subQ2,1.0]])],"derivedFrom":subQ1}),1.0]])]});}
            var Q122;
            {var subQ0=sQuery(id+"F0.wireOp",EDGE,"E15");var subQ1=sQuery(id+"F0.wireOp",EDGE,"E3");var subQ2=makeQuery(id+"F0.imprint","INTERSECT",VERTEX,{"derivedFrom":[subQ1,subQ0,sQuery(id+"F0.wireOp",EDGE,"E32")]});Q122=makeQuery(id+"F0.imprint","IMPRINT",FACE,{"disambiguationData":[TD([[makeQuery(id+"F0.imprint","IMPRINT",EDGE,{"disambiguationData":[TD([[subQ2,-1.0]])],"derivedFrom":subQ1}),1.0]])]});}
            var Q123;
            {var subQ0=sQuery(id+"F0.wireOp",EDGE,"E30");var subQ1=sQuery(id+"F0.wireOp",EDGE,"E22");var subQ2=makeQuery(id+"F0.imprint","INTERSECT",VERTEX,{"derivedFrom":[sQuery(id+"F0.wireOp",EDGE,"E11"),subQ1,subQ0]});Q123=makeQuery(id+"F0.imprint","IMPRINT",FACE,{"disambiguationData":[TD([[makeQuery(id+"F0.imprint","IMPRINT",EDGE,{"disambiguationData":[TD([[subQ2,-1.0]])],"derivedFrom":subQ1}),1.0]])]});}
            var Q124;
            {var subQ0=sQuery(id+"F0.wireOp",EDGE,"E30");var subQ1=sQuery(id+"F0.wireOp",EDGE,"E4");var subQ2=makeQuery(id+"F0.imprint","INTERSECT",VERTEX,{"derivedFrom":[subQ1,sQuery(id+"F0.wireOp",EDGE,"E18"),subQ0]});Q124=makeQuery(id+"F0.imprint","IMPRINT",FACE,{"disambiguationData":[TD([[makeQuery(id+"F0.imprint","IMPRINT",EDGE,{"disambiguationData":[TD([[subQ2,-1.0]])],"derivedFrom":subQ1}),1.0]])]});}
            var Q125;
            {var subQ0=sQuery(id+"F0.wireOp",EDGE,"E30");var subQ1=sQuery(id+"F0.wireOp",EDGE,"E18");var subQ2=makeQuery(id+"F0.imprint","INTERSECT",VERTEX,{"derivedFrom":[sQuery(id+"F0.wireOp",EDGE,"E4"),subQ1,subQ0]});Q125=makeQuery(id+"F0.imprint","IMPRINT",FACE,{"disambiguationData":[TD([[makeQuery(id+"F0.imprint","IMPRINT",EDGE,{"disambiguationData":[TD([[subQ2,1.0]])],"derivedFrom":subQ1}),1.0]])]});}
            var Q126;
            {var subQ0=sQuery(id+"F0.wireOp",EDGE,"E10");var subQ1=sQuery(id+"F0.wireOp",EDGE,"E5");var subQ2=makeQuery(id+"F0.imprint","INTERSECT",VERTEX,{"derivedFrom":[subQ1,subQ0,sQuery(id+"F0.wireOp",EDGE,"E32")]});Q126=makeQuery(id+"F0.imprint","IMPRINT",FACE,{"disambiguationData":[TD([[makeQuery(id+"F0.imprint","IMPRINT",EDGE,{"disambiguationData":[TD([[subQ2,-1.0]])],"derivedFrom":subQ1}),1.0]])]});}
            var Q127;
            {var subQ0=sQuery(id+"F0.wireOp",EDGE,"E30");var subQ1=sQuery(id+"F0.wireOp",EDGE,"E17");var subQ2=makeQuery(id+"F0.imprint","INTERSECT",VERTEX,{"derivedFrom":[sQuery(id+"F0.wireOp",EDGE,"E12"),subQ1,subQ0]});Q127=makeQuery(id+"F0.imprint","IMPRINT",FACE,{"disambiguationData":[TD([[makeQuery(id+"F0.imprint","IMPRINT",EDGE,{"disambiguationData":[TD([[subQ2,-1.0]])],"derivedFrom":subQ1}),1.0]])]});}
            var Q128;
            {var subQ0=sQuery(id+"F0.wireOp",EDGE,"E30");var subQ1=sQuery(id+"F0.wireOp",EDGE,"E3");var subQ2=makeQuery(id+"F0.imprint","INTERSECT",VERTEX,{"derivedFrom":[subQ1,sQuery(id+"F0.wireOp",EDGE,"E19"),subQ0]});Q128=makeQuery(id+"F0.imprint","IMPRINT",FACE,{"disambiguationData":[TD([[makeQuery(id+"F0.imprint","IMPRINT",EDGE,{"disambiguationData":[TD([[subQ2,-1.0]])],"derivedFrom":subQ1}),1.0]])]});}
            var Q129;
            {var subQ0=sQuery(id+"F0.wireOp",EDGE,"E30");var subQ1=sQuery(id+"F0.wireOp",EDGE,"E19");var subQ2=makeQuery(id+"F0.imprint","INTERSECT",VERTEX,{"derivedFrom":[sQuery(id+"F0.wireOp",EDGE,"E3"),subQ1,subQ0]});Q129=makeQuery(id+"F0.imprint","IMPRINT",FACE,{"disambiguationData":[TD([[makeQuery(id+"F0.imprint","IMPRINT",EDGE,{"disambiguationData":[TD([[subQ2,1.0]])],"derivedFrom":subQ1}),1.0]])]});}
            var Q130;
            {var subQ0=sQuery(id+"F0.wireOp",EDGE,"E11");var subQ1=sQuery(id+"F0.wireOp",EDGE,"E7");var subQ2=makeQuery(id+"F0.imprint","INTERSECT",VERTEX,{"derivedFrom":[subQ1,subQ0,sQuery(id+"F0.wireOp",EDGE,"E32")]});Q130=makeQuery(id+"F0.imprint","IMPRINT",FACE,{"disambiguationData":[TD([[makeQuery(id+"F0.imprint","IMPRINT",EDGE,{"disambiguationData":[TD([[subQ2,-1.0]])],"derivedFrom":subQ1}),1.0]])]});}
            var Q131;
            {var subQ0=sQuery(id+"F0.wireOp",EDGE,"E30");var subQ1=sQuery(id+"F0.wireOp",EDGE,"E18");var subQ2=makeQuery(id+"F0.imprint","INTERSECT",VERTEX,{"derivedFrom":[sQuery(id+"F0.wireOp",EDGE,"E13"),subQ1,subQ0]});Q131=makeQuery(id+"F0.imprint","IMPRINT",FACE,{"disambiguationData":[TD([[makeQuery(id+"F0.imprint","IMPRINT",EDGE,{"disambiguationData":[TD([[subQ2,-1.0]])],"derivedFrom":subQ1}),1.0]])]});}
            var Q132;
            {var subQ0=sQuery(id+"F0.wireOp",EDGE,"E30");var subQ1=sQuery(id+"F0.wireOp",EDGE,"E5");var subQ2=makeQuery(id+"F0.imprint","INTERSECT",VERTEX,{"derivedFrom":[subQ1,sQuery(id+"F0.wireOp",EDGE,"E20"),subQ0]});Q132=makeQuery(id+"F0.imprint","IMPRINT",FACE,{"disambiguationData":[TD([[makeQuery(id+"F0.imprint","IMPRINT",EDGE,{"disambiguationData":[TD([[subQ2,-1.0]])],"derivedFrom":subQ1}),1.0]])]});}
            var Q133;
            {var subQ0=sQuery(id+"F0.wireOp",EDGE,"E30");var subQ1=sQuery(id+"F0.wireOp",EDGE,"E20");var subQ2=makeQuery(id+"F0.imprint","INTERSECT",VERTEX,{"derivedFrom":[sQuery(id+"F0.wireOp",EDGE,"E5"),subQ1,subQ0]});Q133=makeQuery(id+"F0.imprint","IMPRINT",FACE,{"disambiguationData":[TD([[makeQuery(id+"F0.imprint","IMPRINT",EDGE,{"disambiguationData":[TD([[subQ2,1.0]])],"derivedFrom":subQ1}),1.0]])]});}
            var Q134;
            {var subQ0=sQuery(id+"F0.wireOp",EDGE,"E12");var subQ1=sQuery(id+"F0.wireOp",EDGE,"E8");var subQ2=makeQuery(id+"F0.imprint","INTERSECT",VERTEX,{"derivedFrom":[subQ1,subQ0,sQuery(id+"F0.wireOp",EDGE,"E32")]});Q134=makeQuery(id+"F0.imprint","IMPRINT",FACE,{"disambiguationData":[TD([[makeQuery(id+"F0.imprint","IMPRINT",EDGE,{"disambiguationData":[TD([[subQ2,-1.0]])],"derivedFrom":subQ1}),1.0]])]});}
            var Q135;
            {var subQ0=sQuery(id+"F0.wireOp",EDGE,"E30");var subQ1=sQuery(id+"F0.wireOp",EDGE,"E19");var subQ2=makeQuery(id+"F0.imprint","INTERSECT",VERTEX,{"derivedFrom":[sQuery(id+"F0.wireOp",EDGE,"E14"),subQ1,subQ0]});Q135=makeQuery(id+"F0.imprint","IMPRINT",FACE,{"disambiguationData":[TD([[makeQuery(id+"F0.imprint","IMPRINT",EDGE,{"disambiguationData":[TD([[subQ2,-1.0]])],"derivedFrom":subQ1}),1.0]])]});}
            var Q136;
            {var subQ0=sQuery(id+"F0.wireOp",EDGE,"E30");var subQ1=sQuery(id+"F0.wireOp",EDGE,"E7");var subQ2=makeQuery(id+"F0.imprint","INTERSECT",VERTEX,{"derivedFrom":[subQ1,sQuery(id+"F0.wireOp",EDGE,"E21"),subQ0]});Q136=makeQuery(id+"F0.imprint","IMPRINT",FACE,{"disambiguationData":[TD([[makeQuery(id+"F0.imprint","IMPRINT",EDGE,{"disambiguationData":[TD([[subQ2,-1.0]])],"derivedFrom":subQ1}),1.0]])]});}
            var Q137;
            {var subQ0=sQuery(id+"F0.wireOp",EDGE,"E30");var subQ1=sQuery(id+"F0.wireOp",EDGE,"E21");var subQ2=makeQuery(id+"F0.imprint","INTERSECT",VERTEX,{"derivedFrom":[sQuery(id+"F0.wireOp",EDGE,"E7"),subQ1,subQ0]});Q137=makeQuery(id+"F0.imprint","IMPRINT",FACE,{"disambiguationData":[TD([[makeQuery(id+"F0.imprint","IMPRINT",EDGE,{"disambiguationData":[TD([[subQ2,1.0]])],"derivedFrom":subQ1}),1.0]])]});}
            var Q138;
            {var subQ0=sQuery(id+"F0.wireOp",EDGE,"E13");var subQ1=sQuery(id+"F0.wireOp",EDGE,"E6");var subQ2=makeQuery(id+"F0.imprint","INTERSECT",VERTEX,{"derivedFrom":[subQ1,subQ0,sQuery(id+"F0.wireOp",EDGE,"E32")]});Q138=makeQuery(id+"F0.imprint","IMPRINT",FACE,{"disambiguationData":[TD([[makeQuery(id+"F0.imprint","IMPRINT",EDGE,{"disambiguationData":[TD([[subQ2,-1.0]])],"derivedFrom":subQ1}),1.0]])]});}
            var Q139;
            {var subQ0=sQuery(id+"F0.wireOp",EDGE,"E30");var subQ1=sQuery(id+"F0.wireOp",EDGE,"E20");var subQ2=makeQuery(id+"F0.imprint","INTERSECT",VERTEX,{"derivedFrom":[sQuery(id+"F0.wireOp",EDGE,"E15"),subQ1,subQ0]});Q139=makeQuery(id+"F0.imprint","IMPRINT",FACE,{"disambiguationData":[TD([[makeQuery(id+"F0.imprint","IMPRINT",EDGE,{"disambiguationData":[TD([[subQ2,-1.0]])],"derivedFrom":subQ1}),1.0]])]});}
            var Q140;
            {var subQ0=sQuery(id+"F0.wireOp",EDGE,"E30");var subQ1=sQuery(id+"F0.wireOp",EDGE,"E8");var subQ2=makeQuery(id+"F0.imprint","INTERSECT",VERTEX,{"derivedFrom":[subQ1,sQuery(id+"F0.wireOp",EDGE,"E22"),subQ0]});Q140=makeQuery(id+"F0.imprint","IMPRINT",FACE,{"disambiguationData":[TD([[makeQuery(id+"F0.imprint","IMPRINT",EDGE,{"disambiguationData":[TD([[subQ2,-1.0]])],"derivedFrom":subQ1}),1.0]])]});}
            var Q141;
            {var subQ0=sQuery(id+"F0.wireOp",EDGE,"E30");var subQ1=sQuery(id+"F0.wireOp",EDGE,"E22");var subQ2=makeQuery(id+"F0.imprint","INTERSECT",VERTEX,{"derivedFrom":[sQuery(id+"F0.wireOp",EDGE,"E8"),subQ1,subQ0]});Q141=makeQuery(id+"F0.imprint","IMPRINT",FACE,{"disambiguationData":[TD([[makeQuery(id+"F0.imprint","IMPRINT",EDGE,{"disambiguationData":[TD([[subQ2,1.0]])],"derivedFrom":subQ1}),1.0]])]});}
            var Q142;
            {var subQ0=sQuery(id+"F0.wireOp",EDGE,"E14");var subQ1=sQuery(id+"F0.wireOp",EDGE,"E4");var subQ2=makeQuery(id+"F0.imprint","INTERSECT",VERTEX,{"derivedFrom":[subQ1,subQ0,sQuery(id+"F0.wireOp",EDGE,"E32")]});Q142=makeQuery(id+"F0.imprint","IMPRINT",FACE,{"disambiguationData":[TD([[makeQuery(id+"F0.imprint","IMPRINT",EDGE,{"disambiguationData":[TD([[subQ2,-1.0]])],"derivedFrom":subQ1}),1.0]])]});}
            var Q143;
            {var subQ0=sQuery(id+"F0.wireOp",EDGE,"E30");var subQ1=sQuery(id+"F0.wireOp",EDGE,"E21");var subQ2=makeQuery(id+"F0.imprint","INTERSECT",VERTEX,{"derivedFrom":[sQuery(id+"F0.wireOp",EDGE,"E10"),subQ1,subQ0]});Q143=makeQuery(id+"F0.imprint","IMPRINT",FACE,{"disambiguationData":[TD([[makeQuery(id+"F0.imprint","IMPRINT",EDGE,{"disambiguationData":[TD([[subQ2,-1.0]])],"derivedFrom":subQ1}),1.0]])]});}
            var Q144;
            {var subQ0=sQuery(id+"F0.wireOp",EDGE,"E32");var subQ1=sQuery(id+"F0.wireOp",EDGE,"E6");var subQ2=makeQuery(id+"F0.imprint","INTERSECT",VERTEX,{"derivedFrom":[subQ1,sQuery(id+"F0.wireOp",EDGE,"E10"),subQ0]});Q144=makeQuery(id+"F0.imprint","IMPRINT",FACE,{"disambiguationData":[TD([[makeQuery(id+"F0.imprint","IMPRINT",EDGE,{"disambiguationData":[TD([[subQ2,-1.0]])],"derivedFrom":subQ1}),1.0]])]});}
            var Q145;
            {var subQ0=sQuery(id+"F0.wireOp",EDGE,"E32");var subQ1=sQuery(id+"F0.wireOp",EDGE,"E10");var subQ2=makeQuery(id+"F0.imprint","INTERSECT",VERTEX,{"derivedFrom":[sQuery(id+"F0.wireOp",EDGE,"E6"),subQ1,subQ0]});Q145=makeQuery(id+"F0.imprint","IMPRINT",FACE,{"disambiguationData":[TD([[makeQuery(id+"F0.imprint","IMPRINT",EDGE,{"disambiguationData":[TD([[subQ2,1.0]])],"derivedFrom":subQ1}),1.0]])]});}
            var Q146;
            {var subQ0=sQuery(id+"F0.wireOp",EDGE,"E32");var subQ1=sQuery(id+"F0.wireOp",EDGE,"E15");var subQ2=makeQuery(id+"F0.imprint","INTERSECT",VERTEX,{"derivedFrom":[sQuery(id+"F0.wireOp",EDGE,"E3"),subQ1,subQ0]});Q146=makeQuery(id+"F0.imprint","IMPRINT",FACE,{"disambiguationData":[TD([[makeQuery(id+"F0.imprint","IMPRINT",EDGE,{"disambiguationData":[TD([[subQ2,-1.0]])],"derivedFrom":subQ1}),1.0]])]});}
            var Q147;
            {var subQ0=sQuery(id+"F0.wireOp",EDGE,"E22");var subQ1=sQuery(id+"F0.wireOp",EDGE,"E3");var subQ2=makeQuery(id+"F0.imprint","INTERSECT",VERTEX,{"derivedFrom":[subQ1,subQ0,sQuery(id+"F0.wireOp",EDGE,"E36")]});Q147=makeQuery(id+"F0.imprint","IMPRINT",FACE,{"disambiguationData":[TD([[makeQuery(id+"F0.imprint","IMPRINT",EDGE,{"disambiguationData":[TD([[subQ2,-1.0]])],"derivedFrom":subQ1}),1.0]])]});}
            var Q148;
            {var subQ0=sQuery(id+"F0.wireOp",EDGE,"E32");var subQ1=sQuery(id+"F0.wireOp",EDGE,"E4");var subQ2=makeQuery(id+"F0.imprint","INTERSECT",VERTEX,{"derivedFrom":[subQ1,sQuery(id+"F0.wireOp",EDGE,"E11"),subQ0]});Q148=makeQuery(id+"F0.imprint","IMPRINT",FACE,{"disambiguationData":[TD([[makeQuery(id+"F0.imprint","IMPRINT",EDGE,{"disambiguationData":[TD([[subQ2,-1.0]])],"derivedFrom":subQ1}),1.0]])]});}
            var Q149;
            {var subQ0=sQuery(id+"F0.wireOp",EDGE,"E32");var subQ1=sQuery(id+"F0.wireOp",EDGE,"E11");var subQ2=makeQuery(id+"F0.imprint","INTERSECT",VERTEX,{"derivedFrom":[sQuery(id+"F0.wireOp",EDGE,"E4"),subQ1,subQ0]});Q149=makeQuery(id+"F0.imprint","IMPRINT",FACE,{"disambiguationData":[TD([[makeQuery(id+"F0.imprint","IMPRINT",EDGE,{"disambiguationData":[TD([[subQ2,1.0]])],"derivedFrom":subQ1}),1.0]])]});}
            var Q150;
            {var subQ0=sQuery(id+"F0.wireOp",EDGE,"E32");var subQ1=sQuery(id+"F0.wireOp",EDGE,"E10");var subQ2=makeQuery(id+"F0.imprint","INTERSECT",VERTEX,{"derivedFrom":[sQuery(id+"F0.wireOp",EDGE,"E5"),subQ1,subQ0]});Q150=makeQuery(id+"F0.imprint","IMPRINT",FACE,{"disambiguationData":[TD([[makeQuery(id+"F0.imprint","IMPRINT",EDGE,{"disambiguationData":[TD([[subQ2,-1.0]])],"derivedFrom":subQ1}),1.0]])]});}
            var Q151;
            {var subQ0=sQuery(id+"F0.wireOp",EDGE,"E17");var subQ1=sQuery(id+"F0.wireOp",EDGE,"E5");var subQ2=makeQuery(id+"F0.imprint","INTERSECT",VERTEX,{"derivedFrom":[subQ1,subQ0,sQuery(id+"F0.wireOp",EDGE,"E36")]});Q151=makeQuery(id+"F0.imprint","IMPRINT",FACE,{"disambiguationData":[TD([[makeQuery(id+"F0.imprint","IMPRINT",EDGE,{"disambiguationData":[TD([[subQ2,-1.0]])],"derivedFrom":subQ1}),1.0]])]});}
            var Q152;
            {var subQ0=sQuery(id+"F0.wireOp",EDGE,"E32");var subQ1=sQuery(id+"F0.wireOp",EDGE,"E3");var subQ2=makeQuery(id+"F0.imprint","INTERSECT",VERTEX,{"derivedFrom":[subQ1,sQuery(id+"F0.wireOp",EDGE,"E12"),subQ0]});Q152=makeQuery(id+"F0.imprint","IMPRINT",FACE,{"disambiguationData":[TD([[makeQuery(id+"F0.imprint","IMPRINT",EDGE,{"disambiguationData":[TD([[subQ2,-1.0]])],"derivedFrom":subQ1}),1.0]])]});}
            var Q153;
            {var subQ0=sQuery(id+"F0.wireOp",EDGE,"E32");var subQ1=sQuery(id+"F0.wireOp",EDGE,"E12");var subQ2=makeQuery(id+"F0.imprint","INTERSECT",VERTEX,{"derivedFrom":[sQuery(id+"F0.wireOp",EDGE,"E3"),subQ1,subQ0]});Q153=makeQuery(id+"F0.imprint","IMPRINT",FACE,{"disambiguationData":[TD([[makeQuery(id+"F0.imprint","IMPRINT",EDGE,{"disambiguationData":[TD([[subQ2,1.0]])],"derivedFrom":subQ1}),1.0]])]});}
            var Q154;
            {var subQ0=sQuery(id+"F0.wireOp",EDGE,"E32");var subQ1=sQuery(id+"F0.wireOp",EDGE,"E11");var subQ2=makeQuery(id+"F0.imprint","INTERSECT",VERTEX,{"derivedFrom":[sQuery(id+"F0.wireOp",EDGE,"E7"),subQ1,subQ0]});Q154=makeQuery(id+"F0.imprint","IMPRINT",FACE,{"disambiguationData":[TD([[makeQuery(id+"F0.imprint","IMPRINT",EDGE,{"disambiguationData":[TD([[subQ2,-1.0]])],"derivedFrom":subQ1}),1.0]])]});}
            var Q155;
            {var subQ0=sQuery(id+"F0.wireOp",EDGE,"E18");var subQ1=sQuery(id+"F0.wireOp",EDGE,"E7");var subQ2=makeQuery(id+"F0.imprint","INTERSECT",VERTEX,{"derivedFrom":[subQ1,subQ0,sQuery(id+"F0.wireOp",EDGE,"E36")]});Q155=makeQuery(id+"F0.imprint","IMPRINT",FACE,{"disambiguationData":[TD([[makeQuery(id+"F0.imprint","IMPRINT",EDGE,{"disambiguationData":[TD([[subQ2,-1.0]])],"derivedFrom":subQ1}),1.0]])]});}
            var Q156;
            {var subQ0=sQuery(id+"F0.wireOp",EDGE,"E32");var subQ1=sQuery(id+"F0.wireOp",EDGE,"E5");var subQ2=makeQuery(id+"F0.imprint","INTERSECT",VERTEX,{"derivedFrom":[subQ1,sQuery(id+"F0.wireOp",EDGE,"E13"),subQ0]});Q156=makeQuery(id+"F0.imprint","IMPRINT",FACE,{"disambiguationData":[TD([[makeQuery(id+"F0.imprint","IMPRINT",EDGE,{"disambiguationData":[TD([[subQ2,-1.0]])],"derivedFrom":subQ1}),1.0]])]});}
            var Q157;
            {var subQ0=sQuery(id+"F0.wireOp",EDGE,"E32");var subQ1=sQuery(id+"F0.wireOp",EDGE,"E13");var subQ2=makeQuery(id+"F0.imprint","INTERSECT",VERTEX,{"derivedFrom":[sQuery(id+"F0.wireOp",EDGE,"E5"),subQ1,subQ0]});Q157=makeQuery(id+"F0.imprint","IMPRINT",FACE,{"disambiguationData":[TD([[makeQuery(id+"F0.imprint","IMPRINT",EDGE,{"disambiguationData":[TD([[subQ2,1.0]])],"derivedFrom":subQ1}),1.0]])]});}
            var Q158;
            {var subQ0=sQuery(id+"F0.wireOp",EDGE,"E32");var subQ1=sQuery(id+"F0.wireOp",EDGE,"E12");var subQ2=makeQuery(id+"F0.imprint","INTERSECT",VERTEX,{"derivedFrom":[sQuery(id+"F0.wireOp",EDGE,"E8"),subQ1,subQ0]});Q158=makeQuery(id+"F0.imprint","IMPRINT",FACE,{"disambiguationData":[TD([[makeQuery(id+"F0.imprint","IMPRINT",EDGE,{"disambiguationData":[TD([[subQ2,-1.0]])],"derivedFrom":subQ1}),1.0]])]});}
            var Q159;
            {var subQ0=sQuery(id+"F0.wireOp",EDGE,"E19");var subQ1=sQuery(id+"F0.wireOp",EDGE,"E8");var subQ2=makeQuery(id+"F0.imprint","INTERSECT",VERTEX,{"derivedFrom":[subQ1,subQ0,sQuery(id+"F0.wireOp",EDGE,"E36")]});Q159=makeQuery(id+"F0.imprint","IMPRINT",FACE,{"disambiguationData":[TD([[makeQuery(id+"F0.imprint","IMPRINT",EDGE,{"disambiguationData":[TD([[subQ2,-1.0]])],"derivedFrom":subQ1}),1.0]])]});}
            var Q160;
            {var subQ0=sQuery(id+"F0.wireOp",EDGE,"E32");var subQ1=sQuery(id+"F0.wireOp",EDGE,"E7");var subQ2=makeQuery(id+"F0.imprint","INTERSECT",VERTEX,{"derivedFrom":[subQ1,sQuery(id+"F0.wireOp",EDGE,"E14"),subQ0]});Q160=makeQuery(id+"F0.imprint","IMPRINT",FACE,{"disambiguationData":[TD([[makeQuery(id+"F0.imprint","IMPRINT",EDGE,{"disambiguationData":[TD([[subQ2,-1.0]])],"derivedFrom":subQ1}),1.0]])]});}
            var Q161;
            {var subQ0=sQuery(id+"F0.wireOp",EDGE,"E32");var subQ1=sQuery(id+"F0.wireOp",EDGE,"E14");var subQ2=makeQuery(id+"F0.imprint","INTERSECT",VERTEX,{"derivedFrom":[sQuery(id+"F0.wireOp",EDGE,"E7"),subQ1,subQ0]});Q161=makeQuery(id+"F0.imprint","IMPRINT",FACE,{"disambiguationData":[TD([[makeQuery(id+"F0.imprint","IMPRINT",EDGE,{"disambiguationData":[TD([[subQ2,1.0]])],"derivedFrom":subQ1}),1.0]])]});}
            var Q162;
            {var subQ0=sQuery(id+"F0.wireOp",EDGE,"E32");var subQ1=sQuery(id+"F0.wireOp",EDGE,"E13");var subQ2=makeQuery(id+"F0.imprint","INTERSECT",VERTEX,{"derivedFrom":[sQuery(id+"F0.wireOp",EDGE,"E6"),subQ1,subQ0]});Q162=makeQuery(id+"F0.imprint","IMPRINT",FACE,{"disambiguationData":[TD([[makeQuery(id+"F0.imprint","IMPRINT",EDGE,{"disambiguationData":[TD([[subQ2,-1.0]])],"derivedFrom":subQ1}),1.0]])]});}
            var Q163;
            {var subQ0=sQuery(id+"F0.wireOp",EDGE,"E20");var subQ1=sQuery(id+"F0.wireOp",EDGE,"E6");var subQ2=makeQuery(id+"F0.imprint","INTERSECT",VERTEX,{"derivedFrom":[subQ1,subQ0,sQuery(id+"F0.wireOp",EDGE,"E36")]});Q163=makeQuery(id+"F0.imprint","IMPRINT",FACE,{"disambiguationData":[TD([[makeQuery(id+"F0.imprint","IMPRINT",EDGE,{"disambiguationData":[TD([[subQ2,-1.0]])],"derivedFrom":subQ1}),1.0]])]});}
            var Q164;
            {var subQ0=sQuery(id+"F0.wireOp",EDGE,"E32");var subQ1=sQuery(id+"F0.wireOp",EDGE,"E8");var subQ2=makeQuery(id+"F0.imprint","INTERSECT",VERTEX,{"derivedFrom":[subQ1,sQuery(id+"F0.wireOp",EDGE,"E15"),subQ0]});Q164=makeQuery(id+"F0.imprint","IMPRINT",FACE,{"disambiguationData":[TD([[makeQuery(id+"F0.imprint","IMPRINT",EDGE,{"disambiguationData":[TD([[subQ2,-1.0]])],"derivedFrom":subQ1}),1.0]])]});}
            var Q165;
            {var subQ0=sQuery(id+"F0.wireOp",EDGE,"E32");var subQ1=sQuery(id+"F0.wireOp",EDGE,"E15");var subQ2=makeQuery(id+"F0.imprint","INTERSECT",VERTEX,{"derivedFrom":[sQuery(id+"F0.wireOp",EDGE,"E8"),subQ1,subQ0]});Q165=makeQuery(id+"F0.imprint","IMPRINT",FACE,{"disambiguationData":[TD([[makeQuery(id+"F0.imprint","IMPRINT",EDGE,{"disambiguationData":[TD([[subQ2,1.0]])],"derivedFrom":subQ1}),1.0]])]});}
            var Q166;
            {var subQ0=sQuery(id+"F0.wireOp",EDGE,"E32");var subQ1=sQuery(id+"F0.wireOp",EDGE,"E14");var subQ2=makeQuery(id+"F0.imprint","INTERSECT",VERTEX,{"derivedFrom":[sQuery(id+"F0.wireOp",EDGE,"E4"),subQ1,subQ0]});Q166=makeQuery(id+"F0.imprint","IMPRINT",FACE,{"disambiguationData":[TD([[makeQuery(id+"F0.imprint","IMPRINT",EDGE,{"disambiguationData":[TD([[subQ2,-1.0]])],"derivedFrom":subQ1}),1.0]])]});}
            var Q167;
            {var subQ0=sQuery(id+"F0.wireOp",EDGE,"E21");var subQ1=sQuery(id+"F0.wireOp",EDGE,"E4");var subQ2=makeQuery(id+"F0.imprint","INTERSECT",VERTEX,{"derivedFrom":[subQ1,subQ0,sQuery(id+"F0.wireOp",EDGE,"E36")]});Q167=makeQuery(id+"F0.imprint","IMPRINT",FACE,{"disambiguationData":[TD([[makeQuery(id+"F0.imprint","IMPRINT",EDGE,{"disambiguationData":[TD([[subQ2,-1.0]])],"derivedFrom":subQ1}),1.0]])]});}
            var Q168;
            {var subQ0=sQuery(id+"F0.wireOp",EDGE,"E15");var subQ1=sQuery(id+"F0.wireOp",EDGE,"E10");var subQ2=makeQuery(id+"F0.imprint","INTERSECT",VERTEX,{"derivedFrom":[subQ1,subQ0,sQuery(id+"F0.wireOp",EDGE,"E40")]});Q168=makeQuery(id+"F0.imprint","IMPRINT",FACE,{"disambiguationData":[TD([[makeQuery(id+"F0.imprint","IMPRINT",EDGE,{"disambiguationData":[TD([[subQ2,-1.0]])],"derivedFrom":subQ1}),1.0]])]});}
            var Q169;
            {var subQ0=sQuery(id+"F0.wireOp",EDGE,"E6");var subQ1=sQuery(id+"F0.wireOp",EDGE,"E4");var subQ2=makeQuery(id+"F0.imprint","INTERSECT",VERTEX,{"derivedFrom":[subQ1,subQ0,sQuery(id+"F0.wireOp",EDGE,"E40")]});Q169=makeQuery(id+"F0.imprint","IMPRINT",FACE,{"disambiguationData":[TD([[makeQuery(id+"F0.imprint","IMPRINT",EDGE,{"disambiguationData":[TD([[subQ2,-1.0]])],"derivedFrom":subQ1}),1.0]])]});}
            var Q170;
            {var subQ0=sQuery(id+"F0.wireOp",EDGE,"E36");var subQ1=sQuery(id+"F0.wireOp",EDGE,"E24");var subQ2=makeQuery(id+"F0.imprint","INTERSECT",VERTEX,{"derivedFrom":[sQuery(id+"F0.wireOp",EDGE,"E10"),subQ1,subQ0]});Q170=makeQuery(id+"F0.imprint","IMPRINT",FACE,{"disambiguationData":[TD([[makeQuery(id+"F0.imprint","IMPRINT",EDGE,{"disambiguationData":[TD([[subQ2,-1.0]])],"derivedFrom":subQ1}),1.0]])]});}
            var Q171;
            {var subQ0=sQuery(id+"F0.wireOp",EDGE,"E36");var subQ1=sQuery(id+"F0.wireOp",EDGE,"E17");var subQ2=makeQuery(id+"F0.imprint","INTERSECT",VERTEX,{"derivedFrom":[sQuery(id+"F0.wireOp",EDGE,"E15"),subQ1,subQ0]});Q171=makeQuery(id+"F0.imprint","IMPRINT",FACE,{"disambiguationData":[TD([[makeQuery(id+"F0.imprint","IMPRINT",EDGE,{"disambiguationData":[TD([[subQ2,1.0]])],"derivedFrom":subQ1}),1.0]])]});}
            var Q172;
            {var subQ0=sQuery(id+"F0.wireOp",EDGE,"E4");var subQ1=sQuery(id+"F0.wireOp",EDGE,"E3");var subQ2=makeQuery(id+"F0.imprint","INTERSECT",VERTEX,{"derivedFrom":[subQ1,subQ0,sQuery(id+"F0.wireOp",EDGE,"E40")]});Q172=makeQuery(id+"F0.imprint","IMPRINT",FACE,{"disambiguationData":[TD([[makeQuery(id+"F0.imprint","IMPRINT",EDGE,{"disambiguationData":[TD([[subQ2,-1.0]])],"derivedFrom":subQ1}),1.0]])]});}
            var Q173;
            {var subQ0=sQuery(id+"F0.wireOp",EDGE,"E36");var subQ1=sQuery(id+"F0.wireOp",EDGE,"E25");var subQ2=makeQuery(id+"F0.imprint","INTERSECT",VERTEX,{"derivedFrom":[sQuery(id+"F0.wireOp",EDGE,"E11"),subQ1,subQ0]});Q173=makeQuery(id+"F0.imprint","IMPRINT",FACE,{"disambiguationData":[TD([[makeQuery(id+"F0.imprint","IMPRINT",EDGE,{"disambiguationData":[TD([[subQ2,-1.0]])],"derivedFrom":subQ1}),1.0]])]});}
            var Q174;
            {var subQ0=sQuery(id+"F0.wireOp",EDGE,"E36");var subQ1=sQuery(id+"F0.wireOp",EDGE,"E10");var subQ2=makeQuery(id+"F0.imprint","INTERSECT",VERTEX,{"derivedFrom":[subQ1,sQuery(id+"F0.wireOp",EDGE,"E18"),subQ0]});Q174=makeQuery(id+"F0.imprint","IMPRINT",FACE,{"disambiguationData":[TD([[makeQuery(id+"F0.imprint","IMPRINT",EDGE,{"disambiguationData":[TD([[subQ2,-1.0]])],"derivedFrom":subQ1}),1.0]])]});}
            var Q175;
            {var subQ0=sQuery(id+"F0.wireOp",EDGE,"E36");var subQ1=sQuery(id+"F0.wireOp",EDGE,"E17");var subQ2=makeQuery(id+"F0.imprint","INTERSECT",VERTEX,{"derivedFrom":[sQuery(id+"F0.wireOp",EDGE,"E5"),subQ1,subQ0]});Q175=makeQuery(id+"F0.imprint","IMPRINT",FACE,{"disambiguationData":[TD([[makeQuery(id+"F0.imprint","IMPRINT",EDGE,{"disambiguationData":[TD([[subQ2,-1.0]])],"derivedFrom":subQ1}),1.0]])]});}
            var Q176;
            {var subQ0=sQuery(id+"F0.wireOp",EDGE,"E36");var subQ1=sQuery(id+"F0.wireOp",EDGE,"E3");var subQ2=makeQuery(id+"F0.imprint","INTERSECT",VERTEX,{"derivedFrom":[subQ1,sQuery(id+"F0.wireOp",EDGE,"E27"),subQ0]});Q176=makeQuery(id+"F0.imprint","IMPRINT",FACE,{"disambiguationData":[TD([[makeQuery(id+"F0.imprint","IMPRINT",EDGE,{"disambiguationData":[TD([[subQ2,-1.0]])],"derivedFrom":subQ1}),1.0]])]});}
            var Q177;
            {var subQ0=sQuery(id+"F0.wireOp",EDGE,"E36");var subQ1=sQuery(id+"F0.wireOp",EDGE,"E26");var subQ2=makeQuery(id+"F0.imprint","INTERSECT",VERTEX,{"derivedFrom":[sQuery(id+"F0.wireOp",EDGE,"E12"),subQ1,subQ0]});Q177=makeQuery(id+"F0.imprint","IMPRINT",FACE,{"disambiguationData":[TD([[makeQuery(id+"F0.imprint","IMPRINT",EDGE,{"disambiguationData":[TD([[subQ2,-1.0]])],"derivedFrom":subQ1}),1.0]])]});}
            var Q178;
            {var subQ0=sQuery(id+"F0.wireOp",EDGE,"E36");var subQ1=sQuery(id+"F0.wireOp",EDGE,"E11");var subQ2=makeQuery(id+"F0.imprint","INTERSECT",VERTEX,{"derivedFrom":[subQ1,sQuery(id+"F0.wireOp",EDGE,"E19"),subQ0]});Q178=makeQuery(id+"F0.imprint","IMPRINT",FACE,{"disambiguationData":[TD([[makeQuery(id+"F0.imprint","IMPRINT",EDGE,{"disambiguationData":[TD([[subQ2,-1.0]])],"derivedFrom":subQ1}),1.0]])]});}
            var Q179;
            {var subQ0=sQuery(id+"F0.wireOp",EDGE,"E36");var subQ1=sQuery(id+"F0.wireOp",EDGE,"E18");var subQ2=makeQuery(id+"F0.imprint","INTERSECT",VERTEX,{"derivedFrom":[sQuery(id+"F0.wireOp",EDGE,"E7"),subQ1,subQ0]});Q179=makeQuery(id+"F0.imprint","IMPRINT",FACE,{"disambiguationData":[TD([[makeQuery(id+"F0.imprint","IMPRINT",EDGE,{"disambiguationData":[TD([[subQ2,-1.0]])],"derivedFrom":subQ1}),1.0]])]});}
            var Q180;
            {var subQ0=sQuery(id+"F0.wireOp",EDGE,"E36");var subQ1=sQuery(id+"F0.wireOp",EDGE,"E5");var subQ2=makeQuery(id+"F0.imprint","INTERSECT",VERTEX,{"derivedFrom":[subQ1,sQuery(id+"F0.wireOp",EDGE,"E28"),subQ0]});Q180=makeQuery(id+"F0.imprint","IMPRINT",FACE,{"disambiguationData":[TD([[makeQuery(id+"F0.imprint","IMPRINT",EDGE,{"disambiguationData":[TD([[subQ2,-1.0]])],"derivedFrom":subQ1}),1.0]])]});}
            var Q181;
            {var subQ0=sQuery(id+"F0.wireOp",EDGE,"E36");var subQ1=sQuery(id+"F0.wireOp",EDGE,"E27");var subQ2=makeQuery(id+"F0.imprint","INTERSECT",VERTEX,{"derivedFrom":[sQuery(id+"F0.wireOp",EDGE,"E13"),subQ1,subQ0]});Q181=makeQuery(id+"F0.imprint","IMPRINT",FACE,{"disambiguationData":[TD([[makeQuery(id+"F0.imprint","IMPRINT",EDGE,{"disambiguationData":[TD([[subQ2,-1.0]])],"derivedFrom":subQ1}),1.0]])]});}
            var Q182;
            {var subQ0=sQuery(id+"F0.wireOp",EDGE,"E36");var subQ1=sQuery(id+"F0.wireOp",EDGE,"E12");var subQ2=makeQuery(id+"F0.imprint","INTERSECT",VERTEX,{"derivedFrom":[subQ1,sQuery(id+"F0.wireOp",EDGE,"E20"),subQ0]});Q182=makeQuery(id+"F0.imprint","IMPRINT",FACE,{"disambiguationData":[TD([[makeQuery(id+"F0.imprint","IMPRINT",EDGE,{"disambiguationData":[TD([[subQ2,-1.0]])],"derivedFrom":subQ1}),1.0]])]});}
            var Q183;
            {var subQ0=sQuery(id+"F0.wireOp",EDGE,"E36");var subQ1=sQuery(id+"F0.wireOp",EDGE,"E19");var subQ2=makeQuery(id+"F0.imprint","INTERSECT",VERTEX,{"derivedFrom":[sQuery(id+"F0.wireOp",EDGE,"E8"),subQ1,subQ0]});Q183=makeQuery(id+"F0.imprint","IMPRINT",FACE,{"disambiguationData":[TD([[makeQuery(id+"F0.imprint","IMPRINT",EDGE,{"disambiguationData":[TD([[subQ2,-1.0]])],"derivedFrom":subQ1}),1.0]])]});}
            var Q184;
            {var subQ0=sQuery(id+"F0.wireOp",EDGE,"E36");var subQ1=sQuery(id+"F0.wireOp",EDGE,"E7");var subQ2=makeQuery(id+"F0.imprint","INTERSECT",VERTEX,{"derivedFrom":[subQ1,sQuery(id+"F0.wireOp",EDGE,"E29"),subQ0]});Q184=makeQuery(id+"F0.imprint","IMPRINT",FACE,{"disambiguationData":[TD([[makeQuery(id+"F0.imprint","IMPRINT",EDGE,{"disambiguationData":[TD([[subQ2,-1.0]])],"derivedFrom":subQ1}),1.0]])]});}
            var Q185;
            {var subQ0=sQuery(id+"F0.wireOp",EDGE,"E36");var subQ1=sQuery(id+"F0.wireOp",EDGE,"E28");var subQ2=makeQuery(id+"F0.imprint","INTERSECT",VERTEX,{"derivedFrom":[sQuery(id+"F0.wireOp",EDGE,"E14"),subQ1,subQ0]});Q185=makeQuery(id+"F0.imprint","IMPRINT",FACE,{"disambiguationData":[TD([[makeQuery(id+"F0.imprint","IMPRINT",EDGE,{"disambiguationData":[TD([[subQ2,-1.0]])],"derivedFrom":subQ1}),1.0]])]});}
            var Q186;
            {var subQ0=sQuery(id+"F0.wireOp",EDGE,"E36");var subQ1=sQuery(id+"F0.wireOp",EDGE,"E13");var subQ2=makeQuery(id+"F0.imprint","INTERSECT",VERTEX,{"derivedFrom":[subQ1,sQuery(id+"F0.wireOp",EDGE,"E21"),subQ0]});Q186=makeQuery(id+"F0.imprint","IMPRINT",FACE,{"disambiguationData":[TD([[makeQuery(id+"F0.imprint","IMPRINT",EDGE,{"disambiguationData":[TD([[subQ2,-1.0]])],"derivedFrom":subQ1}),1.0]])]});}
            var Q187;
            {var subQ0=sQuery(id+"F0.wireOp",EDGE,"E36");var subQ1=sQuery(id+"F0.wireOp",EDGE,"E20");var subQ2=makeQuery(id+"F0.imprint","INTERSECT",VERTEX,{"derivedFrom":[sQuery(id+"F0.wireOp",EDGE,"E6"),subQ1,subQ0]});Q187=makeQuery(id+"F0.imprint","IMPRINT",FACE,{"disambiguationData":[TD([[makeQuery(id+"F0.imprint","IMPRINT",EDGE,{"disambiguationData":[TD([[subQ2,-1.0]])],"derivedFrom":subQ1}),1.0]])]});}
            var Q188;
            {var subQ0=sQuery(id+"F0.wireOp",EDGE,"E8");var subQ1=sQuery(id+"F0.wireOp",EDGE,"E6");var subQ2=makeQuery(id+"F0.imprint","INTERSECT",VERTEX,{"derivedFrom":[subQ1,subQ0,sQuery(id+"F0.wireOp",EDGE,"E40")]});Q188=makeQuery(id+"F0.imprint","IMPRINT",FACE,{"disambiguationData":[TD([[makeQuery(id+"F0.imprint","IMPRINT",EDGE,{"disambiguationData":[TD([[subQ2,-1.0]])],"derivedFrom":subQ1}),1.0]])]});}
            var Q189;
            {var subQ0=sQuery(id+"F0.wireOp",EDGE,"E36");var subQ1=sQuery(id+"F0.wireOp",EDGE,"E24");var subQ2=makeQuery(id+"F0.imprint","INTERSECT",VERTEX,{"derivedFrom":[sQuery(id+"F0.wireOp",EDGE,"E8"),subQ1,subQ0]});Q189=makeQuery(id+"F0.imprint","IMPRINT",FACE,{"disambiguationData":[TD([[makeQuery(id+"F0.imprint","IMPRINT",EDGE,{"disambiguationData":[TD([[subQ2,1.0]])],"derivedFrom":subQ1}),1.0]])]});}
            var Q190;
            {var subQ0=sQuery(id+"F0.wireOp",EDGE,"E36");var subQ1=sQuery(id+"F0.wireOp",EDGE,"E14");var subQ2=makeQuery(id+"F0.imprint","INTERSECT",VERTEX,{"derivedFrom":[subQ1,sQuery(id+"F0.wireOp",EDGE,"E22"),subQ0]});Q190=makeQuery(id+"F0.imprint","IMPRINT",FACE,{"disambiguationData":[TD([[makeQuery(id+"F0.imprint","IMPRINT",EDGE,{"disambiguationData":[TD([[subQ2,-1.0]])],"derivedFrom":subQ1}),1.0]])]});}
            var Q191;
            {var subQ0=sQuery(id+"F0.wireOp",EDGE,"E36");var subQ1=sQuery(id+"F0.wireOp",EDGE,"E21");var subQ2=makeQuery(id+"F0.imprint","INTERSECT",VERTEX,{"derivedFrom":[sQuery(id+"F0.wireOp",EDGE,"E4"),subQ1,subQ0]});Q191=makeQuery(id+"F0.imprint","IMPRINT",FACE,{"disambiguationData":[TD([[makeQuery(id+"F0.imprint","IMPRINT",EDGE,{"disambiguationData":[TD([[subQ2,-1.0]])],"derivedFrom":subQ1}),1.0]])]});}
            var Q192;
            {var subQ0=sQuery(id+"F0.wireOp",EDGE,"E40");var subQ1=sQuery(id+"F0.wireOp",EDGE,"E6");var subQ2=makeQuery(id+"F0.imprint","INTERSECT",VERTEX,{"derivedFrom":[sQuery(id+"F0.wireOp",EDGE,"E4"),subQ1,subQ0]});Q192=makeQuery(id+"F0.imprint","IMPRINT",FACE,{"disambiguationData":[TD([[makeQuery(id+"F0.imprint","IMPRINT",EDGE,{"disambiguationData":[TD([[subQ2,-1.0]])],"derivedFrom":subQ1}),1.0]])]});}
            var Q193;
            {var subQ0=sQuery(id+"F0.wireOp",EDGE,"E24");var subQ1=sQuery(id+"F0.wireOp",EDGE,"E4");var subQ2=makeQuery(id+"F0.imprint","INTERSECT",VERTEX,{"derivedFrom":[subQ1,subQ0,sQuery(id+"F0.wireOp",EDGE,"E38")]});Q193=makeQuery(id+"F0.imprint","IMPRINT",FACE,{"disambiguationData":[TD([[makeQuery(id+"F0.imprint","IMPRINT",EDGE,{"disambiguationData":[TD([[subQ2,-1.0]])],"derivedFrom":subQ1}),1.0]])]});}
            var Q194;
            {var subQ0=sQuery(id+"F0.wireOp",EDGE,"E40");var subQ1=sQuery(id+"F0.wireOp",EDGE,"E15");var subQ2=makeQuery(id+"F0.imprint","INTERSECT",VERTEX,{"derivedFrom":[sQuery(id+"F0.wireOp",EDGE,"E10"),subQ1,subQ0]});Q194=makeQuery(id+"F0.imprint","IMPRINT",FACE,{"disambiguationData":[TD([[makeQuery(id+"F0.imprint","IMPRINT",EDGE,{"disambiguationData":[TD([[subQ2,-1.0]])],"derivedFrom":subQ1}),1.0]])]});}
            var Q195;
            {var subQ0=sQuery(id+"F0.wireOp",EDGE,"E22");var subQ1=sQuery(id+"F0.wireOp",EDGE,"E10");var subQ2=makeQuery(id+"F0.imprint","INTERSECT",VERTEX,{"derivedFrom":[subQ1,subQ0,sQuery(id+"F0.wireOp",EDGE,"E38")]});Q195=makeQuery(id+"F0.imprint","IMPRINT",FACE,{"disambiguationData":[TD([[makeQuery(id+"F0.imprint","IMPRINT",EDGE,{"disambiguationData":[TD([[subQ2,-1.0]])],"derivedFrom":subQ1}),1.0]])]});}
            var Q196;
            {var subQ0=sQuery(id+"F0.wireOp",EDGE,"E40");var subQ1=sQuery(id+"F0.wireOp",EDGE,"E4");var subQ2=makeQuery(id+"F0.imprint","INTERSECT",VERTEX,{"derivedFrom":[sQuery(id+"F0.wireOp",EDGE,"E3"),subQ1,subQ0]});Q196=makeQuery(id+"F0.imprint","IMPRINT",FACE,{"disambiguationData":[TD([[makeQuery(id+"F0.imprint","IMPRINT",EDGE,{"disambiguationData":[TD([[subQ2,-1.0]])],"derivedFrom":subQ1}),1.0]])]});}
            var Q197;
            {var subQ0=sQuery(id+"F0.wireOp",EDGE,"E25");var subQ1=sQuery(id+"F0.wireOp",EDGE,"E3");var subQ2=makeQuery(id+"F0.imprint","INTERSECT",VERTEX,{"derivedFrom":[subQ1,subQ0,sQuery(id+"F0.wireOp",EDGE,"E38")]});Q197=makeQuery(id+"F0.imprint","IMPRINT",FACE,{"disambiguationData":[TD([[makeQuery(id+"F0.imprint","IMPRINT",EDGE,{"disambiguationData":[TD([[subQ2,-1.0]])],"derivedFrom":subQ1}),1.0]])]});}
            var Q198;
            {var subQ0=sQuery(id+"F0.wireOp",EDGE,"E40");var subQ1=sQuery(id+"F0.wireOp",EDGE,"E10");var subQ2=makeQuery(id+"F0.imprint","INTERSECT",VERTEX,{"derivedFrom":[subQ1,sQuery(id+"F0.wireOp",EDGE,"E11"),subQ0]});Q198=makeQuery(id+"F0.imprint","IMPRINT",FACE,{"disambiguationData":[TD([[makeQuery(id+"F0.imprint","IMPRINT",EDGE,{"disambiguationData":[TD([[subQ2,-1.0]])],"derivedFrom":subQ1}),1.0]])]});}
            var Q199;
            {var subQ0=sQuery(id+"F0.wireOp",EDGE,"E40");var subQ1=sQuery(id+"F0.wireOp",EDGE,"E11");var subQ2=makeQuery(id+"F0.imprint","INTERSECT",VERTEX,{"derivedFrom":[sQuery(id+"F0.wireOp",EDGE,"E10"),subQ1,subQ0]});Q199=makeQuery(id+"F0.imprint","IMPRINT",FACE,{"disambiguationData":[TD([[makeQuery(id+"F0.imprint","IMPRINT",EDGE,{"disambiguationData":[TD([[subQ2,1.0]])],"derivedFrom":subQ1}),1.0]])]});}
            var Q200;
            {var subQ0=sQuery(id+"F0.wireOp",EDGE,"E40");var subQ1=sQuery(id+"F0.wireOp",EDGE,"E3");var subQ2=makeQuery(id+"F0.imprint","INTERSECT",VERTEX,{"derivedFrom":[subQ1,sQuery(id+"F0.wireOp",EDGE,"E5"),subQ0]});Q200=makeQuery(id+"F0.imprint","IMPRINT",FACE,{"disambiguationData":[TD([[makeQuery(id+"F0.imprint","IMPRINT",EDGE,{"disambiguationData":[TD([[subQ2,-1.0]])],"derivedFrom":subQ1}),1.0]])]});}
            var Q201;
            {var subQ0=sQuery(id+"F0.wireOp",EDGE,"E40");var subQ1=sQuery(id+"F0.wireOp",EDGE,"E5");var subQ2=makeQuery(id+"F0.imprint","INTERSECT",VERTEX,{"derivedFrom":[sQuery(id+"F0.wireOp",EDGE,"E3"),subQ1,subQ0]});Q201=makeQuery(id+"F0.imprint","IMPRINT",FACE,{"disambiguationData":[TD([[makeQuery(id+"F0.imprint","IMPRINT",EDGE,{"disambiguationData":[TD([[subQ2,1.0]])],"derivedFrom":subQ1}),1.0]])]});}
            var Q202;
            {var subQ0=sQuery(id+"F0.wireOp",EDGE,"E40");var subQ1=sQuery(id+"F0.wireOp",EDGE,"E11");var subQ2=makeQuery(id+"F0.imprint","INTERSECT",VERTEX,{"derivedFrom":[subQ1,sQuery(id+"F0.wireOp",EDGE,"E12"),subQ0]});Q202=makeQuery(id+"F0.imprint","IMPRINT",FACE,{"disambiguationData":[TD([[makeQuery(id+"F0.imprint","IMPRINT",EDGE,{"disambiguationData":[TD([[subQ2,-1.0]])],"derivedFrom":subQ1}),1.0]])]});}
            var Q203;
            {var subQ0=sQuery(id+"F0.wireOp",EDGE,"E40");var subQ1=sQuery(id+"F0.wireOp",EDGE,"E12");var subQ2=makeQuery(id+"F0.imprint","INTERSECT",VERTEX,{"derivedFrom":[sQuery(id+"F0.wireOp",EDGE,"E11"),subQ1,subQ0]});Q203=makeQuery(id+"F0.imprint","IMPRINT",FACE,{"disambiguationData":[TD([[makeQuery(id+"F0.imprint","IMPRINT",EDGE,{"disambiguationData":[TD([[subQ2,1.0]])],"derivedFrom":subQ1}),1.0]])]});}
            var Q204;
            {var subQ0=sQuery(id+"F0.wireOp",EDGE,"E40");var subQ1=sQuery(id+"F0.wireOp",EDGE,"E5");var subQ2=makeQuery(id+"F0.imprint","INTERSECT",VERTEX,{"derivedFrom":[subQ1,sQuery(id+"F0.wireOp",EDGE,"E7"),subQ0]});Q204=makeQuery(id+"F0.imprint","IMPRINT",FACE,{"disambiguationData":[TD([[makeQuery(id+"F0.imprint","IMPRINT",EDGE,{"disambiguationData":[TD([[subQ2,-1.0]])],"derivedFrom":subQ1}),1.0]])]});}
            var Q205;
            {var subQ0=sQuery(id+"F0.wireOp",EDGE,"E40");var subQ1=sQuery(id+"F0.wireOp",EDGE,"E7");var subQ2=makeQuery(id+"F0.imprint","INTERSECT",VERTEX,{"derivedFrom":[sQuery(id+"F0.wireOp",EDGE,"E5"),subQ1,subQ0]});Q205=makeQuery(id+"F0.imprint","IMPRINT",FACE,{"disambiguationData":[TD([[makeQuery(id+"F0.imprint","IMPRINT",EDGE,{"disambiguationData":[TD([[subQ2,1.0]])],"derivedFrom":subQ1}),1.0]])]});}
            var Q206;
            {var subQ0=sQuery(id+"F0.wireOp",EDGE,"E40");var subQ1=sQuery(id+"F0.wireOp",EDGE,"E12");var subQ2=makeQuery(id+"F0.imprint","INTERSECT",VERTEX,{"derivedFrom":[subQ1,sQuery(id+"F0.wireOp",EDGE,"E13"),subQ0]});Q206=makeQuery(id+"F0.imprint","IMPRINT",FACE,{"disambiguationData":[TD([[makeQuery(id+"F0.imprint","IMPRINT",EDGE,{"disambiguationData":[TD([[subQ2,-1.0]])],"derivedFrom":subQ1}),1.0]])]});}
            var Q207;
            {var subQ0=sQuery(id+"F0.wireOp",EDGE,"E40");var subQ1=sQuery(id+"F0.wireOp",EDGE,"E13");var subQ2=makeQuery(id+"F0.imprint","INTERSECT",VERTEX,{"derivedFrom":[sQuery(id+"F0.wireOp",EDGE,"E12"),subQ1,subQ0]});Q207=makeQuery(id+"F0.imprint","IMPRINT",FACE,{"disambiguationData":[TD([[makeQuery(id+"F0.imprint","IMPRINT",EDGE,{"disambiguationData":[TD([[subQ2,1.0]])],"derivedFrom":subQ1}),1.0]])]});}
            var Q208;
            {var subQ0=sQuery(id+"F0.wireOp",EDGE,"E40");var subQ1=sQuery(id+"F0.wireOp",EDGE,"E7");var subQ2=makeQuery(id+"F0.imprint","INTERSECT",VERTEX,{"derivedFrom":[subQ1,sQuery(id+"F0.wireOp",EDGE,"E8"),subQ0]});Q208=makeQuery(id+"F0.imprint","IMPRINT",FACE,{"disambiguationData":[TD([[makeQuery(id+"F0.imprint","IMPRINT",EDGE,{"disambiguationData":[TD([[subQ2,-1.0]])],"derivedFrom":subQ1}),1.0]])]});}
            var Q209;
            {var subQ0=sQuery(id+"F0.wireOp",EDGE,"E40");var subQ1=sQuery(id+"F0.wireOp",EDGE,"E8");var subQ2=makeQuery(id+"F0.imprint","INTERSECT",VERTEX,{"derivedFrom":[sQuery(id+"F0.wireOp",EDGE,"E7"),subQ1,subQ0]});Q209=makeQuery(id+"F0.imprint","IMPRINT",FACE,{"disambiguationData":[TD([[makeQuery(id+"F0.imprint","IMPRINT",EDGE,{"disambiguationData":[TD([[subQ2,1.0]])],"derivedFrom":subQ1}),1.0]])]});}
            var Q210;
            {var subQ0=sQuery(id+"F0.wireOp",EDGE,"E40");var subQ1=sQuery(id+"F0.wireOp",EDGE,"E13");var subQ2=makeQuery(id+"F0.imprint","INTERSECT",VERTEX,{"derivedFrom":[subQ1,sQuery(id+"F0.wireOp",EDGE,"E14"),subQ0]});Q210=makeQuery(id+"F0.imprint","IMPRINT",FACE,{"disambiguationData":[TD([[makeQuery(id+"F0.imprint","IMPRINT",EDGE,{"disambiguationData":[TD([[subQ2,-1.0]])],"derivedFrom":subQ1}),1.0]])]});}
            var Q211;
            {var subQ0=sQuery(id+"F0.wireOp",EDGE,"E40");var subQ1=sQuery(id+"F0.wireOp",EDGE,"E14");var subQ2=makeQuery(id+"F0.imprint","INTERSECT",VERTEX,{"derivedFrom":[sQuery(id+"F0.wireOp",EDGE,"E13"),subQ1,subQ0]});Q211=makeQuery(id+"F0.imprint","IMPRINT",FACE,{"disambiguationData":[TD([[makeQuery(id+"F0.imprint","IMPRINT",EDGE,{"disambiguationData":[TD([[subQ2,1.0]])],"derivedFrom":subQ1}),1.0]])]});}
            var Q212;
            {var subQ0=sQuery(id+"F0.wireOp",EDGE,"E40");var subQ1=sQuery(id+"F0.wireOp",EDGE,"E8");var subQ2=makeQuery(id+"F0.imprint","INTERSECT",VERTEX,{"derivedFrom":[sQuery(id+"F0.wireOp",EDGE,"E6"),subQ1,subQ0]});Q212=makeQuery(id+"F0.imprint","IMPRINT",FACE,{"disambiguationData":[TD([[makeQuery(id+"F0.imprint","IMPRINT",EDGE,{"disambiguationData":[TD([[subQ2,-1.0]])],"derivedFrom":subQ1}),1.0]])]});}
            var Q213;
            {var subQ0=sQuery(id+"F0.wireOp",EDGE,"E29");var subQ1=sQuery(id+"F0.wireOp",EDGE,"E6");var subQ2=makeQuery(id+"F0.imprint","INTERSECT",VERTEX,{"derivedFrom":[subQ1,subQ0,sQuery(id+"F0.wireOp",EDGE,"E38")]});Q213=makeQuery(id+"F0.imprint","IMPRINT",FACE,{"disambiguationData":[TD([[makeQuery(id+"F0.imprint","IMPRINT",EDGE,{"disambiguationData":[TD([[subQ2,-1.0]])],"derivedFrom":subQ1}),1.0]])]});}
            var Q214;
            {var subQ0=sQuery(id+"F0.wireOp",EDGE,"E40");var subQ1=sQuery(id+"F0.wireOp",EDGE,"E14");var subQ2=makeQuery(id+"F0.imprint","INTERSECT",VERTEX,{"derivedFrom":[subQ1,sQuery(id+"F0.wireOp",EDGE,"E15"),subQ0]});Q214=makeQuery(id+"F0.imprint","IMPRINT",FACE,{"disambiguationData":[TD([[makeQuery(id+"F0.imprint","IMPRINT",EDGE,{"disambiguationData":[TD([[subQ2,-1.0]])],"derivedFrom":subQ1}),1.0]])]});}
            var Q215;
            {var subQ0=sQuery(id+"F0.wireOp",EDGE,"E40");var subQ1=sQuery(id+"F0.wireOp",EDGE,"E15");var subQ2=makeQuery(id+"F0.imprint","INTERSECT",VERTEX,{"derivedFrom":[sQuery(id+"F0.wireOp",EDGE,"E14"),subQ1,subQ0]});Q215=makeQuery(id+"F0.imprint","IMPRINT",FACE,{"disambiguationData":[TD([[makeQuery(id+"F0.imprint","IMPRINT",EDGE,{"disambiguationData":[TD([[subQ2,1.0]])],"derivedFrom":subQ1}),1.0]])]});}
            var Q216;
            {var subQ0=sQuery(id+"F0.wireOp",EDGE,"E38");var subQ1=sQuery(id+"F0.wireOp",EDGE,"E22");var subQ2=makeQuery(id+"F0.imprint","INTERSECT",VERTEX,{"derivedFrom":[sQuery(id+"F0.wireOp",EDGE,"E6"),subQ1,subQ0]});Q216=makeQuery(id+"F0.imprint","IMPRINT",FACE,{"disambiguationData":[TD([[makeQuery(id+"F0.imprint","IMPRINT",EDGE,{"disambiguationData":[TD([[subQ2,1.0]])],"derivedFrom":subQ1}),1.0]])]});}
            var Q217;
            {var subQ0=sQuery(id+"F0.wireOp",EDGE,"E15");var subQ1=sQuery(id+"F0.wireOp",EDGE,"E4");var subQ2=makeQuery(id+"F0.imprint","INTERSECT",VERTEX,{"derivedFrom":[subQ1,subQ0,sQuery(id+"F0.wireOp",EDGE,"E34")]});Q217=makeQuery(id+"F0.imprint","IMPRINT",FACE,{"disambiguationData":[TD([[makeQuery(id+"F0.imprint","IMPRINT",EDGE,{"disambiguationData":[TD([[subQ2,-1.0]])],"derivedFrom":subQ1}),1.0]])]});}
            var Q218;
            {var subQ0=sQuery(id+"F0.wireOp",EDGE,"E38");var subQ1=sQuery(id+"F0.wireOp",EDGE,"E22");var subQ2=makeQuery(id+"F0.imprint","INTERSECT",VERTEX,{"derivedFrom":[sQuery(id+"F0.wireOp",EDGE,"E10"),subQ1,subQ0]});Q218=makeQuery(id+"F0.imprint","IMPRINT",FACE,{"disambiguationData":[TD([[makeQuery(id+"F0.imprint","IMPRINT",EDGE,{"disambiguationData":[TD([[subQ2,-1.0]])],"derivedFrom":subQ1}),1.0]])]});}
            var Q219;
            {var subQ0=sQuery(id+"F0.wireOp",EDGE,"E38");var subQ1=sQuery(id+"F0.wireOp",EDGE,"E4");var subQ2=makeQuery(id+"F0.imprint","INTERSECT",VERTEX,{"derivedFrom":[subQ1,sQuery(id+"F0.wireOp",EDGE,"E17"),subQ0]});Q219=makeQuery(id+"F0.imprint","IMPRINT",FACE,{"disambiguationData":[TD([[makeQuery(id+"F0.imprint","IMPRINT",EDGE,{"disambiguationData":[TD([[subQ2,-1.0]])],"derivedFrom":subQ1}),1.0]])]});}
            var Q220;
            {var subQ0=sQuery(id+"F0.wireOp",EDGE,"E38");var subQ1=sQuery(id+"F0.wireOp",EDGE,"E17");var subQ2=makeQuery(id+"F0.imprint","INTERSECT",VERTEX,{"derivedFrom":[sQuery(id+"F0.wireOp",EDGE,"E4"),subQ1,subQ0]});Q220=makeQuery(id+"F0.imprint","IMPRINT",FACE,{"disambiguationData":[TD([[makeQuery(id+"F0.imprint","IMPRINT",EDGE,{"disambiguationData":[TD([[subQ2,1.0]])],"derivedFrom":subQ1}),1.0]])]});}
            var Q221;
            {var subQ0=sQuery(id+"F0.wireOp",EDGE,"E10");var subQ1=sQuery(id+"F0.wireOp",EDGE,"E3");var subQ2=makeQuery(id+"F0.imprint","INTERSECT",VERTEX,{"derivedFrom":[subQ1,subQ0,sQuery(id+"F0.wireOp",EDGE,"E34")]});Q221=makeQuery(id+"F0.imprint","IMPRINT",FACE,{"disambiguationData":[TD([[makeQuery(id+"F0.imprint","IMPRINT",EDGE,{"disambiguationData":[TD([[subQ2,-1.0]])],"derivedFrom":subQ1}),1.0]])]});}
            var Q222;
            {var subQ0=sQuery(id+"F0.wireOp",EDGE,"E38");var subQ1=sQuery(id+"F0.wireOp",EDGE,"E17");var subQ2=makeQuery(id+"F0.imprint","INTERSECT",VERTEX,{"derivedFrom":[sQuery(id+"F0.wireOp",EDGE,"E11"),subQ1,subQ0]});Q222=makeQuery(id+"F0.imprint","IMPRINT",FACE,{"disambiguationData":[TD([[makeQuery(id+"F0.imprint","IMPRINT",EDGE,{"disambiguationData":[TD([[subQ2,-1.0]])],"derivedFrom":subQ1}),1.0]])]});}
            var Q223;
            {var subQ0=sQuery(id+"F0.wireOp",EDGE,"E38");var subQ1=sQuery(id+"F0.wireOp",EDGE,"E3");var subQ2=makeQuery(id+"F0.imprint","INTERSECT",VERTEX,{"derivedFrom":[subQ1,sQuery(id+"F0.wireOp",EDGE,"E18"),subQ0]});Q223=makeQuery(id+"F0.imprint","IMPRINT",FACE,{"disambiguationData":[TD([[makeQuery(id+"F0.imprint","IMPRINT",EDGE,{"disambiguationData":[TD([[subQ2,-1.0]])],"derivedFrom":subQ1}),1.0]])]});}
            var Q224;
            {var subQ0=sQuery(id+"F0.wireOp",EDGE,"E38");var subQ1=sQuery(id+"F0.wireOp",EDGE,"E18");var subQ2=makeQuery(id+"F0.imprint","INTERSECT",VERTEX,{"derivedFrom":[sQuery(id+"F0.wireOp",EDGE,"E3"),subQ1,subQ0]});Q224=makeQuery(id+"F0.imprint","IMPRINT",FACE,{"disambiguationData":[TD([[makeQuery(id+"F0.imprint","IMPRINT",EDGE,{"disambiguationData":[TD([[subQ2,1.0]])],"derivedFrom":subQ1}),1.0]])]});}
            var Q225;
            {var subQ0=sQuery(id+"F0.wireOp",EDGE,"E11");var subQ1=sQuery(id+"F0.wireOp",EDGE,"E5");var subQ2=makeQuery(id+"F0.imprint","INTERSECT",VERTEX,{"derivedFrom":[subQ1,subQ0,sQuery(id+"F0.wireOp",EDGE,"E34")]});Q225=makeQuery(id+"F0.imprint","IMPRINT",FACE,{"disambiguationData":[TD([[makeQuery(id+"F0.imprint","IMPRINT",EDGE,{"disambiguationData":[TD([[subQ2,-1.0]])],"derivedFrom":subQ1}),1.0]])]});}
            var Q226;
            {var subQ0=sQuery(id+"F0.wireOp",EDGE,"E38");var subQ1=sQuery(id+"F0.wireOp",EDGE,"E18");var subQ2=makeQuery(id+"F0.imprint","INTERSECT",VERTEX,{"derivedFrom":[sQuery(id+"F0.wireOp",EDGE,"E12"),subQ1,subQ0]});Q226=makeQuery(id+"F0.imprint","IMPRINT",FACE,{"disambiguationData":[TD([[makeQuery(id+"F0.imprint","IMPRINT",EDGE,{"disambiguationData":[TD([[subQ2,-1.0]])],"derivedFrom":subQ1}),1.0]])]});}
            var Q227;
            {var subQ0=sQuery(id+"F0.wireOp",EDGE,"E38");var subQ1=sQuery(id+"F0.wireOp",EDGE,"E5");var subQ2=makeQuery(id+"F0.imprint","INTERSECT",VERTEX,{"derivedFrom":[subQ1,sQuery(id+"F0.wireOp",EDGE,"E19"),subQ0]});Q227=makeQuery(id+"F0.imprint","IMPRINT",FACE,{"disambiguationData":[TD([[makeQuery(id+"F0.imprint","IMPRINT",EDGE,{"disambiguationData":[TD([[subQ2,-1.0]])],"derivedFrom":subQ1}),1.0]])]});}
            var Q228;
            {var subQ0=sQuery(id+"F0.wireOp",EDGE,"E38");var subQ1=sQuery(id+"F0.wireOp",EDGE,"E19");var subQ2=makeQuery(id+"F0.imprint","INTERSECT",VERTEX,{"derivedFrom":[sQuery(id+"F0.wireOp",EDGE,"E5"),subQ1,subQ0]});Q228=makeQuery(id+"F0.imprint","IMPRINT",FACE,{"disambiguationData":[TD([[makeQuery(id+"F0.imprint","IMPRINT",EDGE,{"disambiguationData":[TD([[subQ2,1.0]])],"derivedFrom":subQ1}),1.0]])]});}
            var Q229;
            {var subQ0=sQuery(id+"F0.wireOp",EDGE,"E12");var subQ1=sQuery(id+"F0.wireOp",EDGE,"E7");var subQ2=makeQuery(id+"F0.imprint","INTERSECT",VERTEX,{"derivedFrom":[subQ1,subQ0,sQuery(id+"F0.wireOp",EDGE,"E34")]});Q229=makeQuery(id+"F0.imprint","IMPRINT",FACE,{"disambiguationData":[TD([[makeQuery(id+"F0.imprint","IMPRINT",EDGE,{"disambiguationData":[TD([[subQ2,-1.0]])],"derivedFrom":subQ1}),1.0]])]});}
            var Q230;
            {var subQ0=sQuery(id+"F0.wireOp",EDGE,"E38");var subQ1=sQuery(id+"F0.wireOp",EDGE,"E19");var subQ2=makeQuery(id+"F0.imprint","INTERSECT",VERTEX,{"derivedFrom":[sQuery(id+"F0.wireOp",EDGE,"E13"),subQ1,subQ0]});Q230=makeQuery(id+"F0.imprint","IMPRINT",FACE,{"disambiguationData":[TD([[makeQuery(id+"F0.imprint","IMPRINT",EDGE,{"disambiguationData":[TD([[subQ2,-1.0]])],"derivedFrom":subQ1}),1.0]])]});}
            var Q231;
            {var subQ0=sQuery(id+"F0.wireOp",EDGE,"E38");var subQ1=sQuery(id+"F0.wireOp",EDGE,"E7");var subQ2=makeQuery(id+"F0.imprint","INTERSECT",VERTEX,{"derivedFrom":[subQ1,sQuery(id+"F0.wireOp",EDGE,"E20"),subQ0]});Q231=makeQuery(id+"F0.imprint","IMPRINT",FACE,{"disambiguationData":[TD([[makeQuery(id+"F0.imprint","IMPRINT",EDGE,{"disambiguationData":[TD([[subQ2,-1.0]])],"derivedFrom":subQ1}),1.0]])]});}
            var Q232;
            {var subQ0=sQuery(id+"F0.wireOp",EDGE,"E38");var subQ1=sQuery(id+"F0.wireOp",EDGE,"E20");var subQ2=makeQuery(id+"F0.imprint","INTERSECT",VERTEX,{"derivedFrom":[sQuery(id+"F0.wireOp",EDGE,"E7"),subQ1,subQ0]});Q232=makeQuery(id+"F0.imprint","IMPRINT",FACE,{"disambiguationData":[TD([[makeQuery(id+"F0.imprint","IMPRINT",EDGE,{"disambiguationData":[TD([[subQ2,1.0]])],"derivedFrom":subQ1}),1.0]])]});}
            var Q233;
            {var subQ0=sQuery(id+"F0.wireOp",EDGE,"E13");var subQ1=sQuery(id+"F0.wireOp",EDGE,"E8");var subQ2=makeQuery(id+"F0.imprint","INTERSECT",VERTEX,{"derivedFrom":[subQ1,subQ0,sQuery(id+"F0.wireOp",EDGE,"E34")]});Q233=makeQuery(id+"F0.imprint","IMPRINT",FACE,{"disambiguationData":[TD([[makeQuery(id+"F0.imprint","IMPRINT",EDGE,{"disambiguationData":[TD([[subQ2,-1.0]])],"derivedFrom":subQ1}),1.0]])]});}
            var Q234;
            {var subQ0=sQuery(id+"F0.wireOp",EDGE,"E38");var subQ1=sQuery(id+"F0.wireOp",EDGE,"E20");var subQ2=makeQuery(id+"F0.imprint","INTERSECT",VERTEX,{"derivedFrom":[sQuery(id+"F0.wireOp",EDGE,"E14"),subQ1,subQ0]});Q234=makeQuery(id+"F0.imprint","IMPRINT",FACE,{"disambiguationData":[TD([[makeQuery(id+"F0.imprint","IMPRINT",EDGE,{"disambiguationData":[TD([[subQ2,-1.0]])],"derivedFrom":subQ1}),1.0]])]});}
            var Q235;
            {var subQ0=sQuery(id+"F0.wireOp",EDGE,"E38");var subQ1=sQuery(id+"F0.wireOp",EDGE,"E8");var subQ2=makeQuery(id+"F0.imprint","INTERSECT",VERTEX,{"derivedFrom":[subQ1,sQuery(id+"F0.wireOp",EDGE,"E21"),subQ0]});Q235=makeQuery(id+"F0.imprint","IMPRINT",FACE,{"disambiguationData":[TD([[makeQuery(id+"F0.imprint","IMPRINT",EDGE,{"disambiguationData":[TD([[subQ2,-1.0]])],"derivedFrom":subQ1}),1.0]])]});}
            var Q236;
            {var subQ0=sQuery(id+"F0.wireOp",EDGE,"E38");var subQ1=sQuery(id+"F0.wireOp",EDGE,"E21");var subQ2=makeQuery(id+"F0.imprint","INTERSECT",VERTEX,{"derivedFrom":[sQuery(id+"F0.wireOp",EDGE,"E8"),subQ1,subQ0]});Q236=makeQuery(id+"F0.imprint","IMPRINT",FACE,{"disambiguationData":[TD([[makeQuery(id+"F0.imprint","IMPRINT",EDGE,{"disambiguationData":[TD([[subQ2,1.0]])],"derivedFrom":subQ1}),1.0]])]});}
            var Q237;
            {var subQ0=sQuery(id+"F0.wireOp",EDGE,"E14");var subQ1=sQuery(id+"F0.wireOp",EDGE,"E6");var subQ2=makeQuery(id+"F0.imprint","INTERSECT",VERTEX,{"derivedFrom":[subQ1,subQ0,sQuery(id+"F0.wireOp",EDGE,"E34")]});Q237=makeQuery(id+"F0.imprint","IMPRINT",FACE,{"disambiguationData":[TD([[makeQuery(id+"F0.imprint","IMPRINT",EDGE,{"disambiguationData":[TD([[subQ2,-1.0]])],"derivedFrom":subQ1}),1.0]])]});}
            var Q238;
            {var subQ0=sQuery(id+"F0.wireOp",EDGE,"E38");var subQ1=sQuery(id+"F0.wireOp",EDGE,"E21");var subQ2=makeQuery(id+"F0.imprint","INTERSECT",VERTEX,{"derivedFrom":[sQuery(id+"F0.wireOp",EDGE,"E15"),subQ1,subQ0]});Q238=makeQuery(id+"F0.imprint","IMPRINT",FACE,{"disambiguationData":[TD([[makeQuery(id+"F0.imprint","IMPRINT",EDGE,{"disambiguationData":[TD([[subQ2,-1.0]])],"derivedFrom":subQ1}),1.0]])]});}
            var Q239;
            {var subQ0=sQuery(id+"F0.wireOp",EDGE,"E38");var subQ1=sQuery(id+"F0.wireOp",EDGE,"E6");var subQ2=makeQuery(id+"F0.imprint","INTERSECT",VERTEX,{"derivedFrom":[subQ1,sQuery(id+"F0.wireOp",EDGE,"E22"),subQ0]});Q239=makeQuery(id+"F0.imprint","IMPRINT",FACE,{"disambiguationData":[TD([[makeQuery(id+"F0.imprint","IMPRINT",EDGE,{"disambiguationData":[TD([[subQ2,-1.0]])],"derivedFrom":subQ1}),1.0]])]});}
            var Q240;
            {var subQ0=sQuery(id+"F0.wireOp",EDGE,"E22");var subQ1=sQuery(id+"F0.wireOp",EDGE,"E15");var subQ2=makeQuery(id+"F0.imprint","INTERSECT",VERTEX,{"derivedFrom":[subQ1,subQ0]});Q240=makeQuery(id+"F0.imprint","IMPRINT",FACE,{"disambiguationData":[TD([[makeQuery(id+"F0.imprint","IMPRINT",EDGE,{"disambiguationData":[TD([[subQ2,1.0]])],"derivedFrom":subQ1}),1.0]])]});}
            var Q241;
            {var subQ0=sQuery(id+"F0.wireOp",EDGE,"E22");var subQ1=sQuery(id+"F0.wireOp",EDGE,"E4");var subQ2=makeQuery(id+"F0.imprint","INTERSECT",VERTEX,{"derivedFrom":[subQ1,subQ0]});Q241=makeQuery(id+"F0.imprint","IMPRINT",FACE,{"disambiguationData":[TD([[makeQuery(id+"F0.imprint","IMPRINT",EDGE,{"disambiguationData":[TD([[subQ2,-1.0]])],"derivedFrom":subQ1}),1.0]])]});}
            var Q242;
            {var subQ0=sQuery(id+"F0.wireOp",EDGE,"E25");var subQ1=sQuery(id+"F0.wireOp",EDGE,"E4");var subQ2=makeQuery(id+"F0.imprint","INTERSECT",VERTEX,{"derivedFrom":[subQ1,subQ0]});Q242=makeQuery(id+"F0.imprint","IMPRINT",FACE,{"disambiguationData":[TD([[makeQuery(id+"F0.imprint","IMPRINT",EDGE,{"disambiguationData":[TD([[subQ2,1.0]])],"derivedFrom":subQ1}),1.0]])]});}
            var Q243;
            {var subQ0=sQuery(id+"F0.wireOp",EDGE,"E25");var subQ1=sQuery(id+"F0.wireOp",EDGE,"E10");var subQ2=makeQuery(id+"F0.imprint","INTERSECT",VERTEX,{"derivedFrom":[subQ1,subQ0]});Q243=makeQuery(id+"F0.imprint","IMPRINT",FACE,{"disambiguationData":[TD([[makeQuery(id+"F0.imprint","IMPRINT",EDGE,{"disambiguationData":[TD([[subQ2,-1.0]])],"derivedFrom":subQ1}),1.0]])]});}
            var Q244;
            {var subQ0=sQuery(id+"F0.wireOp",EDGE,"E17");var subQ1=sQuery(id+"F0.wireOp",EDGE,"E10");var subQ2=makeQuery(id+"F0.imprint","INTERSECT",VERTEX,{"derivedFrom":[subQ1,subQ0]});Q244=makeQuery(id+"F0.imprint","IMPRINT",FACE,{"disambiguationData":[TD([[makeQuery(id+"F0.imprint","IMPRINT",EDGE,{"disambiguationData":[TD([[subQ2,1.0]])],"derivedFrom":subQ1}),1.0]])]});}
            var Q245;
            {var subQ0=sQuery(id+"F0.wireOp",EDGE,"E17");var subQ1=sQuery(id+"F0.wireOp",EDGE,"E3");var subQ2=makeQuery(id+"F0.imprint","INTERSECT",VERTEX,{"derivedFrom":[subQ1,subQ0]});Q245=makeQuery(id+"F0.imprint","IMPRINT",FACE,{"disambiguationData":[TD([[makeQuery(id+"F0.imprint","IMPRINT",EDGE,{"disambiguationData":[TD([[subQ2,-1.0]])],"derivedFrom":subQ1}),1.0]])]});}
            var Q246;
            {var subQ0=sQuery(id+"F0.wireOp",EDGE,"E26");var subQ1=sQuery(id+"F0.wireOp",EDGE,"E3");var subQ2=makeQuery(id+"F0.imprint","INTERSECT",VERTEX,{"derivedFrom":[subQ1,subQ0]});Q246=makeQuery(id+"F0.imprint","IMPRINT",FACE,{"disambiguationData":[TD([[makeQuery(id+"F0.imprint","IMPRINT",EDGE,{"disambiguationData":[TD([[subQ2,1.0]])],"derivedFrom":subQ1}),1.0]])]});}
            var Q247;
            {var subQ0=sQuery(id+"F0.wireOp",EDGE,"E26");var subQ1=sQuery(id+"F0.wireOp",EDGE,"E11");var subQ2=makeQuery(id+"F0.imprint","INTERSECT",VERTEX,{"derivedFrom":[subQ1,subQ0]});Q247=makeQuery(id+"F0.imprint","IMPRINT",FACE,{"disambiguationData":[TD([[makeQuery(id+"F0.imprint","IMPRINT",EDGE,{"disambiguationData":[TD([[subQ2,-1.0]])],"derivedFrom":subQ1}),1.0]])]});}
            var Q248;
            {var subQ0=sQuery(id+"F0.wireOp",EDGE,"E18");var subQ1=sQuery(id+"F0.wireOp",EDGE,"E11");var subQ2=makeQuery(id+"F0.imprint","INTERSECT",VERTEX,{"derivedFrom":[subQ1,subQ0]});Q248=makeQuery(id+"F0.imprint","IMPRINT",FACE,{"disambiguationData":[TD([[makeQuery(id+"F0.imprint","IMPRINT",EDGE,{"disambiguationData":[TD([[subQ2,1.0]])],"derivedFrom":subQ1}),1.0]])]});}
            var Q249;
            {var subQ0=sQuery(id+"F0.wireOp",EDGE,"E18");var subQ1=sQuery(id+"F0.wireOp",EDGE,"E5");var subQ2=makeQuery(id+"F0.imprint","INTERSECT",VERTEX,{"derivedFrom":[subQ1,subQ0]});Q249=makeQuery(id+"F0.imprint","IMPRINT",FACE,{"disambiguationData":[TD([[makeQuery(id+"F0.imprint","IMPRINT",EDGE,{"disambiguationData":[TD([[subQ2,-1.0]])],"derivedFrom":subQ1}),1.0]])]});}
            var Q250;
            {var subQ0=sQuery(id+"F0.wireOp",EDGE,"E27");var subQ1=sQuery(id+"F0.wireOp",EDGE,"E5");var subQ2=makeQuery(id+"F0.imprint","INTERSECT",VERTEX,{"derivedFrom":[subQ1,subQ0]});Q250=makeQuery(id+"F0.imprint","IMPRINT",FACE,{"disambiguationData":[TD([[makeQuery(id+"F0.imprint","IMPRINT",EDGE,{"disambiguationData":[TD([[subQ2,1.0]])],"derivedFrom":subQ1}),1.0]])]});}
            var Q251;
            {var subQ0=sQuery(id+"F0.wireOp",EDGE,"E27");var subQ1=sQuery(id+"F0.wireOp",EDGE,"E12");var subQ2=makeQuery(id+"F0.imprint","INTERSECT",VERTEX,{"derivedFrom":[subQ1,subQ0]});Q251=makeQuery(id+"F0.imprint","IMPRINT",FACE,{"disambiguationData":[TD([[makeQuery(id+"F0.imprint","IMPRINT",EDGE,{"disambiguationData":[TD([[subQ2,-1.0]])],"derivedFrom":subQ1}),1.0]])]});}
            var Q252;
            {var subQ0=sQuery(id+"F0.wireOp",EDGE,"E19");var subQ1=sQuery(id+"F0.wireOp",EDGE,"E12");var subQ2=makeQuery(id+"F0.imprint","INTERSECT",VERTEX,{"derivedFrom":[subQ1,subQ0]});Q252=makeQuery(id+"F0.imprint","IMPRINT",FACE,{"disambiguationData":[TD([[makeQuery(id+"F0.imprint","IMPRINT",EDGE,{"disambiguationData":[TD([[subQ2,1.0]])],"derivedFrom":subQ1}),1.0]])]});}
            var Q253;
            {var subQ0=sQuery(id+"F0.wireOp",EDGE,"E19");var subQ1=sQuery(id+"F0.wireOp",EDGE,"E7");var subQ2=makeQuery(id+"F0.imprint","INTERSECT",VERTEX,{"derivedFrom":[subQ1,subQ0]});Q253=makeQuery(id+"F0.imprint","IMPRINT",FACE,{"disambiguationData":[TD([[makeQuery(id+"F0.imprint","IMPRINT",EDGE,{"disambiguationData":[TD([[subQ2,-1.0]])],"derivedFrom":subQ1}),1.0]])]});}
            var Q254;
            {var subQ0=sQuery(id+"F0.wireOp",EDGE,"E28");var subQ1=sQuery(id+"F0.wireOp",EDGE,"E7");var subQ2=makeQuery(id+"F0.imprint","INTERSECT",VERTEX,{"derivedFrom":[subQ1,subQ0]});Q254=makeQuery(id+"F0.imprint","IMPRINT",FACE,{"disambiguationData":[TD([[makeQuery(id+"F0.imprint","IMPRINT",EDGE,{"disambiguationData":[TD([[subQ2,1.0]])],"derivedFrom":subQ1}),1.0]])]});}
            var Q255;
            {var subQ0=sQuery(id+"F0.wireOp",EDGE,"E28");var subQ1=sQuery(id+"F0.wireOp",EDGE,"E13");var subQ2=makeQuery(id+"F0.imprint","INTERSECT",VERTEX,{"derivedFrom":[subQ1,subQ0]});Q255=makeQuery(id+"F0.imprint","IMPRINT",FACE,{"disambiguationData":[TD([[makeQuery(id+"F0.imprint","IMPRINT",EDGE,{"disambiguationData":[TD([[subQ2,-1.0]])],"derivedFrom":subQ1}),1.0]])]});}
            var Q256;
            {var subQ0=sQuery(id+"F0.wireOp",EDGE,"E20");var subQ1=sQuery(id+"F0.wireOp",EDGE,"E13");var subQ2=makeQuery(id+"F0.imprint","INTERSECT",VERTEX,{"derivedFrom":[subQ1,subQ0]});Q256=makeQuery(id+"F0.imprint","IMPRINT",FACE,{"disambiguationData":[TD([[makeQuery(id+"F0.imprint","IMPRINT",EDGE,{"disambiguationData":[TD([[subQ2,1.0]])],"derivedFrom":subQ1}),1.0]])]});}
            var Q257;
            {var subQ0=sQuery(id+"F0.wireOp",EDGE,"E20");var subQ1=sQuery(id+"F0.wireOp",EDGE,"E8");var subQ2=makeQuery(id+"F0.imprint","INTERSECT",VERTEX,{"derivedFrom":[subQ1,subQ0]});Q257=makeQuery(id+"F0.imprint","IMPRINT",FACE,{"disambiguationData":[TD([[makeQuery(id+"F0.imprint","IMPRINT",EDGE,{"disambiguationData":[TD([[subQ2,-1.0]])],"derivedFrom":subQ1}),1.0]])]});}
            var Q258;
            {var subQ0=sQuery(id+"F0.wireOp",EDGE,"E29");var subQ1=sQuery(id+"F0.wireOp",EDGE,"E8");var subQ2=makeQuery(id+"F0.imprint","INTERSECT",VERTEX,{"derivedFrom":[subQ1,subQ0]});Q258=makeQuery(id+"F0.imprint","IMPRINT",FACE,{"disambiguationData":[TD([[makeQuery(id+"F0.imprint","IMPRINT",EDGE,{"disambiguationData":[TD([[subQ2,1.0]])],"derivedFrom":subQ1}),1.0]])]});}
            var Q259;
            {var subQ0=sQuery(id+"F0.wireOp",EDGE,"E21");var subQ1=sQuery(id+"F0.wireOp",EDGE,"E14");var subQ2=makeQuery(id+"F0.imprint","INTERSECT",VERTEX,{"derivedFrom":[subQ1,subQ0]});Q259=makeQuery(id+"F0.imprint","IMPRINT",FACE,{"disambiguationData":[TD([[makeQuery(id+"F0.imprint","IMPRINT",EDGE,{"disambiguationData":[TD([[subQ2,1.0]])],"derivedFrom":subQ1}),1.0]])]});}
            var Q260;
            {var subQ0=sQuery(id+"F0.wireOp",EDGE,"E21");var subQ1=sQuery(id+"F0.wireOp",EDGE,"E6");var subQ2=makeQuery(id+"F0.imprint","INTERSECT",VERTEX,{"derivedFrom":[subQ1,subQ0]});Q260=makeQuery(id+"F0.imprint","IMPRINT",FACE,{"disambiguationData":[TD([[makeQuery(id+"F0.imprint","IMPRINT",EDGE,{"disambiguationData":[TD([[subQ2,-1.0]])],"derivedFrom":subQ1}),1.0]])]});}
            var Q261;
            {var subQ0=sQuery(id+"F0.wireOp",EDGE,"E24");var subQ1=sQuery(id+"F0.wireOp",EDGE,"E6");var subQ2=makeQuery(id+"F0.imprint","INTERSECT",VERTEX,{"derivedFrom":[subQ1,subQ0]});Q261=makeQuery(id+"F0.imprint","IMPRINT",FACE,{"disambiguationData":[TD([[makeQuery(id+"F0.imprint","IMPRINT",EDGE,{"disambiguationData":[TD([[subQ2,1.0]])],"derivedFrom":subQ1}),1.0]])]});}
            var Q262;
            {var subQ0=sQuery(id+"F0.wireOp",EDGE,"E24");var subQ1=sQuery(id+"F0.wireOp",EDGE,"E15");var subQ2=makeQuery(id+"F0.imprint","INTERSECT",VERTEX,{"derivedFrom":[subQ1,subQ0]});Q262=makeQuery(id+"F0.imprint","IMPRINT",FACE,{"disambiguationData":[TD([[makeQuery(id+"F0.imprint","IMPRINT",EDGE,{"disambiguationData":[TD([[subQ2,-1.0]])],"derivedFrom":subQ1}),1.0]])]});}
            var Q263;
            {var subQ0=sQuery(id+"F0.wireOp",EDGE,"E29");var subQ1=sQuery(id+"F0.wireOp",EDGE,"E14");var subQ2=makeQuery(id+"F0.imprint","INTERSECT",VERTEX,{"derivedFrom":[subQ1,subQ0]});Q263=makeQuery(id+"F0.imprint","IMPRINT",FACE,{"disambiguationData":[TD([[makeQuery(id+"F0.imprint","IMPRINT",EDGE,{"disambiguationData":[TD([[subQ2,-1.0]])],"derivedFrom":subQ1}),1.0]])]});}
            extrude(context, id + "F6", {"entities" : qUnion([Q0, Q1, Q2, Q3, Q4, Q5, Q6, Q7, Q8, Q9, Q10, Q11, Q12, Q13, Q14, Q15, Q16, Q17, Q18, Q19, Q20, Q21, Q22, Q23, Q24, Q25, Q26, Q27, Q28, Q29, Q30, Q31, Q32, Q33, Q34, Q35, Q36, Q37, Q38, Q39, Q40, Q41, Q42, Q43, Q44, Q45, Q46, Q47, Q48, Q49, Q50, Q51, Q52, Q53, Q54, Q55, Q56, Q57, Q58, Q59, Q60, Q61, Q62, Q63, Q64, Q65, Q66, Q67, Q68, Q69, Q70, Q71, Q72, Q73, Q74, Q75, Q76, Q77, Q78, Q79, Q80, Q81, Q82, Q83, Q84, Q85, Q86, Q87, Q88, Q89, Q90, Q91, Q92, Q93, Q94, Q95, Q96, Q97, Q98, Q99, Q100, Q101, Q102, Q103, Q104, Q105, Q106, Q107, Q108, Q109, Q110, Q111, Q112, Q113, Q114, Q115, Q116, Q117, Q118, Q119, Q120, Q121, Q122, Q123, Q124, Q125, Q126, Q127, Q128, Q129, Q130, Q131, Q132, Q133, Q134, Q135, Q136, Q137, Q138, Q139, Q140, Q141, Q142, Q143, Q144, Q145, Q146, Q147, Q148, Q149, Q150, Q151, Q152, Q153, Q154, Q155, Q156, Q157, Q158, Q159, Q160, Q161, Q162, Q163, Q164, Q165, Q166, Q167, Q168, Q169, Q170, Q171, Q172, Q173, Q174, Q175, Q176, Q177, Q178, Q179, Q180, Q181, Q182, Q183, Q184, Q185, Q186, Q187, Q188, Q189, Q190, Q191, Q192, Q193, Q194, Q195, Q196, Q197, Q198, Q199, Q200, Q201, Q202, Q203, Q204, Q205, Q206, Q207, Q208, Q209, Q210, Q211, Q212, Q213, Q214, Q215, Q216, Q217, Q218, Q219, Q220, Q221, Q222, Q223, Q224, Q225, Q226, Q227, Q228, Q229, Q230, Q231, Q232, Q233, Q234, Q235, Q236, Q237, Q238, Q239, Q240, Q241, Q242, Q243, Q244, Q245, Q246, Q247, Q248, Q249, Q250, Q251, Q252, Q253, Q254, Q255, Q256, Q257, Q258, Q259, Q260, Q261, Q262, Q263]), "depth" : 2 * mm});
        }
    });
